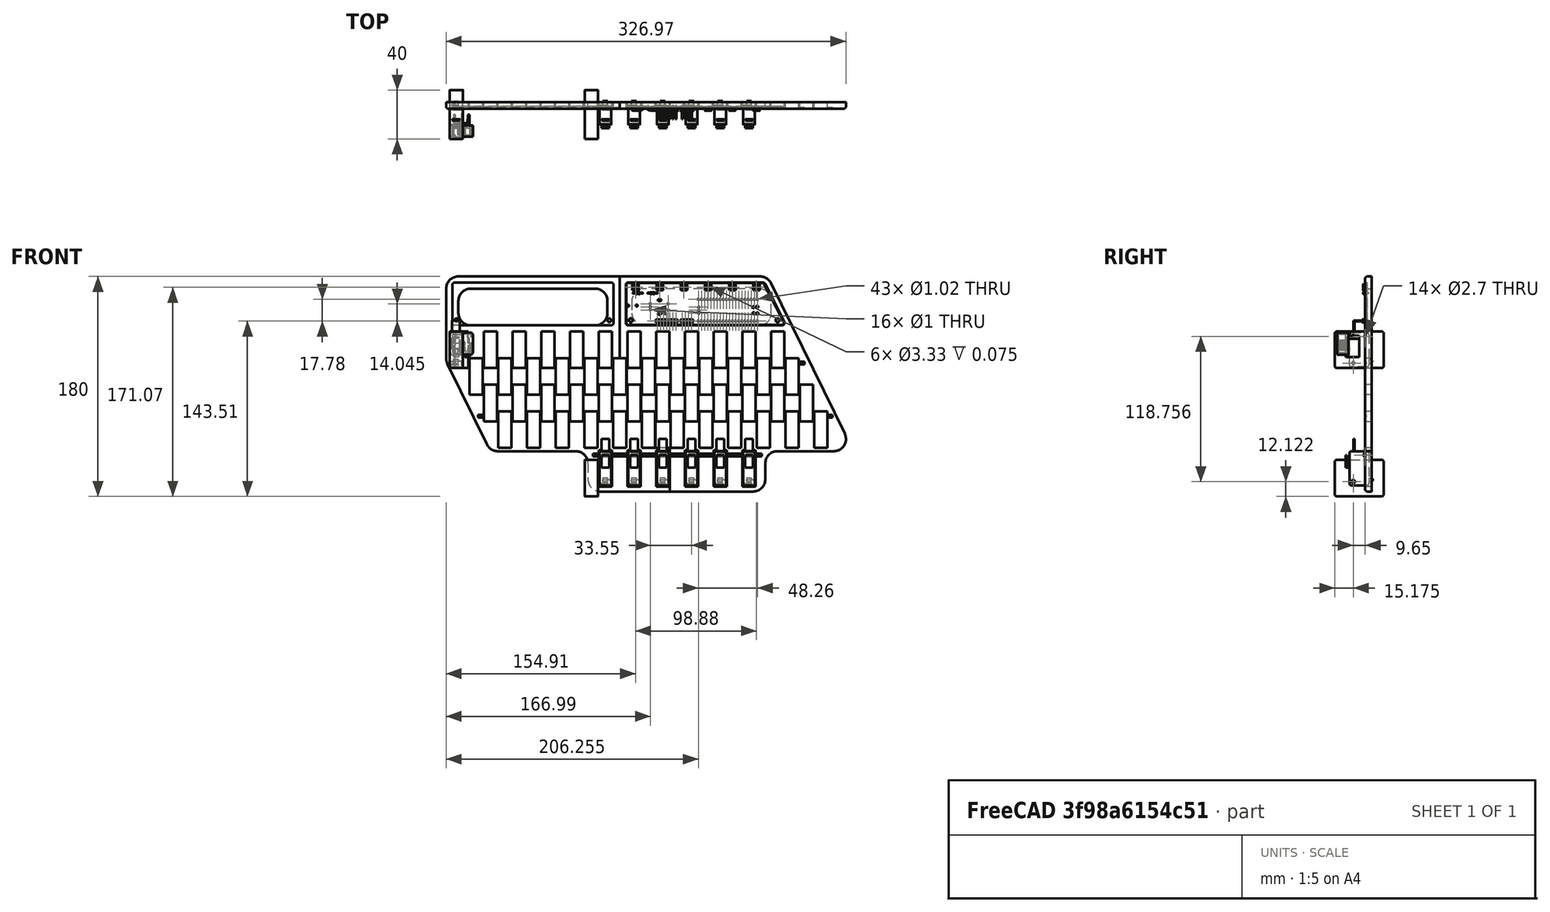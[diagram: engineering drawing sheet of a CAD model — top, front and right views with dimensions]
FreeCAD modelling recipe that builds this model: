
FCSTD DOCUMENT  (FreeCAD 0.20R29603 (Git))
Label: newKeyboard
License: All rights reserved
LicenseURL: http://en.wikipedia.org/wiki/All_rights_reserved
objects: Sketcher::SketchObject×88, PartDesign::Pad×83, PartDesign::Body×34, Part::FeaturePython×20, PartDesign::Fillet×12, Part::Cut×12, App::DocumentObjectGroup×8, PartDesign::FeatureBase×4, PartDesign::Revolution×2, PartDesign::Pocket×2, Mesh::Feature×1, PartDesign::ShapeBinder×1, Part::Extrusion×1, Part::Feature×1
note: 342 computed .brp shape members not serialized (recipe doc carries the construction recipe); baked Part::Feature solids carry a one-line shape summary decoded from their .brp

FEATURE [Sketcher::SketchObject] Sketch
  FullyConstrained = true
  MapMode = 5
  Support = -> [XY_Plane]
  sketch-geometry (12):
    g0: Circle CenterX=10.8779 CenterY=-4.825 CenterZ=0 NormalX=0 NormalY=0 NormalZ=1 AngleXU=0 Radius=1.35
    g1: Circle CenterX=-10.8779 CenterY=4.825 CenterZ=0 NormalX=0 NormalY=0 NormalZ=1 AngleXU=0 Radius=1.35
    g2: ArcOfCircle CenterX=-12.25 CenterY=6.25 CenterZ=0 NormalX=0 NormalY=0 NormalZ=1 AngleXU=0 Radius=1.75 StartAngle=1.5708 EndAngle=3.14159
    g3: LineSegment StartX=-12.25 StartY=8 StartZ=0 EndX=12.25 EndY=8 EndZ=0
    g4: ArcOfCircle CenterX=12.25 CenterY=6.25 CenterZ=0 NormalX=0 NormalY=0 NormalZ=1 AngleXU=0 Radius=1.75 StartAngle=3e-16 EndAngle=1.5708
    g5: LineSegment StartX=14 StartY=6.25 StartZ=0 EndX=14 EndY=-6.25 EndZ=0
    g6: ArcOfCircle CenterX=12.25 CenterY=-6.25 CenterZ=0 NormalX=0 NormalY=0 NormalZ=1 AngleXU=0 Radius=1.75 StartAngle=4.71239 EndAngle=6.28319
    g7: LineSegment StartX=12.25 StartY=-8 StartZ=0 EndX=-12.25 EndY=-8 EndZ=0
    g8: ArcOfCircle CenterX=-12.25 CenterY=-6.25 CenterZ=0 NormalX=0 NormalY=0 NormalZ=1 AngleXU=0 Radius=1.75 StartAngle=3.14159 EndAngle=4.71239
    g9: LineSegment StartX=-14 StartY=-6.25 StartZ=0 EndX=-14 EndY=6.25 EndZ=0
    g10: GeomPoint X=-14 Y=8 Z=0
    g11: GeomPoint X=14 Y=-8 Z=0
  constraints (28):
    c: Tangent(g2,g3) = 1.5708
    c: Tangent(g3,g4) = 1.5708
    c: Tangent(g4,g5) = 1.5708
    c: Tangent(g5,g6) = 1.5708
    c: Tangent(g6,g7) = 1.5708
    c: Tangent(g7,g8) = 1.5708
    c: Tangent(g8,g9) = 1.5708
    c: Tangent(g9,g2) = 1.5708
    c: Horizontal(g3)
    c: Horizontal(g7)
    c: Vertical(g5)
    c: Vertical(g9)
    c: Equal(g2,g4)
    c: Equal(g4,g6)
    c: Equal(g6,g8)
    c: PointOnObject(g10,g3)
    c: PointOnObject(g10,g9)
    c: PointOnObject(g11,g5)
    c: PointOnObject(g11,g7)
    c: DistanceX(g2,g4) = 28
    c: DistanceY(g7,g2) = 16
    c: Symmetric(g8,g4,g-1)
    c: Diameter(g2) = 3.5
    c: Symmetric(g0,g1,g-1)
    c: Diameter(g1) = 2.7
    c: Diameter(g0) = 2.7
    c: DistanceY(g0,g1) = 9.65
    c: Distance(g1,g0) = 23.8
FEATURE [PartDesign::Pad] Pad
  Direction = (0,0,1)
  Length = 9.7
  Length2 = 10
  Profile = -> Sketch
  ReferenceAxis = -> Sketch [N_Axis]
  Type = 0
FEATURE [Sketcher::SketchObject] Sketch001
  FullyConstrained = true
  MapMode = 5
  Placement = pos=(0,8,0) rot=(0,0.707107,0.707107;3.14159rad)
  Support = -> [Pad]
  sketch-geometry (4):
    g0: LineSegment StartX=-10.9 StartY=6.9 StartZ=0 EndX=-8 EndY=6.9 EndZ=0
    g1: LineSegment StartX=-8 StartY=6.9 StartZ=0 EndX=-8 EndY=2.8 EndZ=0
    g2: LineSegment StartX=-8 StartY=2.8 StartZ=0 EndX=-10.9 EndY=2.8 EndZ=0
    g3: LineSegment StartX=-10.9 StartY=2.8 StartZ=0 EndX=-10.9 EndY=6.9 EndZ=0
  constraints (12):
    c: Coincident(g0,g1)
    c: Coincident(g1,g2)
    c: Coincident(g2,g3)
    c: Coincident(g3,g0)
    c: Horizontal(g0)
    c: Horizontal(g2)
    c: Vertical(g1)
    c: Vertical(g3)
    c: DistanceX(g0,g0) = 2.9
    c: DistanceY(g3,g3) = 4.1
    c: DistanceY(g-1,g1) = 2.8
    c: DistanceX(g2,g-1) = 10.9
FEATURE [PartDesign::Pad] Pad001
  BaseFeature = -> Pad
  Direction = (0,1,-2e-16)
  Length = 3
  Length2 = 10
  Profile = -> Sketch001
  ReferenceAxis = -> Sketch001 [N_Axis]
  Type = 0
FEATURE [Sketcher::SketchObject] Sketch002
  FullyConstrained = true
  MapMode = 5
  Placement = pos=(-14,0,0) rot=(0.57735,-0.57735,-0.57735;2.0944rad)
  Support = -> [Pad001]
  sketch-geometry (4):
    g0: LineSegment StartX=3.9 StartY=1.65 StartZ=0 EndX=4.7 EndY=1.65 EndZ=0
    g1: LineSegment StartX=4.7 StartY=1.65 StartZ=0 EndX=4.7 EndY=8.05 EndZ=0
    g2: LineSegment StartX=4.7 StartY=8.05 StartZ=0 EndX=3.9 EndY=8.05 EndZ=0
    g3: LineSegment StartX=3.9 StartY=8.05 StartZ=0 EndX=3.9 EndY=1.65 EndZ=0
  constraints (12):
    c: Coincident(g0,g1)
    c: Coincident(g1,g2)
    c: Coincident(g2,g3)
    c: Coincident(g3,g0)
    c: Horizontal(g0)
    c: Horizontal(g2)
    c: Vertical(g1)
    c: Vertical(g3)
    c: DistanceX(g2,g2) = 0.8
    c: DistanceY(g3,g3) = 6.4
    c: DistanceY(g-1,g0) = 1.65
    c: DistanceX(g-1,g0) = 4.7
FEATURE [PartDesign::Pad] Pad002
  BaseFeature = -> Pad001
  Direction = (-1,0,0)
  Length = 10
  Length2 = 10
  Profile = -> Sketch002
  ReferenceAxis = -> Sketch002 [N_Axis]
  Type = 0
FEATURE [Sketcher::SketchObject] Sketch003
  FullyConstrained = true
  MapMode = 5
  Placement = pos=(0,-8,0) rot=(1,0,0;1.5708rad)
  Support = -> [Pad002]
  sketch-geometry (4):
    g0: LineSegment StartX=-1.3 StartY=8.05 StartZ=0 EndX=-0.5 EndY=8.05 EndZ=0
    g1: LineSegment StartX=-0.5 StartY=8.05 StartZ=0 EndX=-0.5 EndY=1.65 EndZ=0
    g2: LineSegment StartX=-0.5 StartY=1.65 StartZ=0 EndX=-1.3 EndY=1.65 EndZ=0
    g3: LineSegment StartX=-1.3 StartY=1.65 StartZ=0 EndX=-1.3 EndY=8.05 EndZ=0
  constraints (12):
    c: Coincident(g0,g1)
    c: Coincident(g1,g2)
    c: Coincident(g2,g3)
    c: Coincident(g3,g0)
    c: Horizontal(g0)
    c: Horizontal(g2)
    c: Vertical(g1)
    c: Vertical(g3)
    c: DistanceY(g1,g1) = 6.4
    c: DistanceX(g0,g0) = 0.8
    c: DistanceY(g-1,g1) = 1.65
    c: DistanceX(g1,g-1) = 0.5
FEATURE [PartDesign::Pad] Pad003
  BaseFeature = -> Pad002
  Direction = (0,-1,2e-16)
  Length = 3
  Length2 = 10
  Profile = -> Sketch003
  ReferenceAxis = -> Sketch003 [N_Axis]
  Type = 0
FEATURE [Sketcher::SketchObject] Sketch004
  FullyConstrained = true
  MapMode = 5
  Placement = pos=(-1.3,0,0) rot=(0.57735,-0.57735,-0.57735;2.0944rad)
  Support = -> [Pad003]
  sketch-geometry (4):
    g0: LineSegment StartX=10.2 StartY=8.05 StartZ=0 EndX=11 EndY=8.05 EndZ=0
    g1: LineSegment StartX=11 StartY=8.05 StartZ=0 EndX=11 EndY=1.65 EndZ=0
    g2: LineSegment StartX=11 StartY=1.65 StartZ=0 EndX=10.2 EndY=1.65 EndZ=0
    g3: LineSegment StartX=10.2 StartY=1.65 StartZ=0 EndX=10.2 EndY=8.05 EndZ=0
  constraints (12):
    c: Coincident(g0,g1)
    c: Coincident(g1,g2)
    c: Coincident(g2,g3)
    c: Coincident(g3,g0)
    c: Horizontal(g0)
    c: Horizontal(g2)
    c: Vertical(g1)
    c: Vertical(g3)
    c: DistanceX(g0,g0) = 0.8
    c: DistanceY(g1,g1) = 6.4
    c: DistanceY(g-1,g2) = 1.65
    c: DistanceX(g-1,g2) = 10.2
FEATURE [PartDesign::Pad] Pad004
  BaseFeature = -> Pad003
  Direction = (-1,0,0)
  Length = 9.3
  Length2 = 10
  Profile = -> Sketch004
  ReferenceAxis = -> Sketch004 [N_Axis]
  Type = 0
FEATURE [PartDesign::Fillet] Fillet
  Base = -> Pad004 [Edge36,Edge40]
  BaseFeature = -> Pad004
  Radius = 1.2
  SupportTransform = false
  UseAllEdges = false
FEATURE [PartDesign::Body] Body  label="switch"
  Group = -> [Sketch,Pad,Sketch001,Pad001,Sketch002,Pad002,Sketch003,Pad003,Sketch004,Pad004,Fillet]
  Origin = -> Origin
  Placement = pos=(0,0,0) rot=(0,1,0;1.5708rad)
  Tip = -> Fillet
FEATURE [Part::FeaturePython] Array  # Draft array (typed FeaturePython)
  AlwaysSyncPlacement = false
  Angle = 360
  ArrayType = 0
  Axis = (0,0,1)
  Base = -> Body
  Center = (0,0,0)
  Count = 12
  ExpandArray = false
  Fuse = false
  IntervalAxis = (0,0,0)
  IntervalX = (23.5,0,0)
  IntervalY = (0,100,0)
  IntervalZ = (0,0,40)
  NumberCircles = 3
  NumberPolar = 5
  NumberX = 12
  NumberY = 1
  NumberZ = 1
  Placement = pos=(273,0,0) rot=(0,1,0;3.14159rad)
  PlacementList = 12 placements: arithmetic series from (0,0,0) step (23.5,0,0) to (258.5,0,0)
  RadialDistance = 50
  ScaleList = (12) [(1,1,1),(1,1,1),(1,1,1),(1,1,1),(1,1,1),(1,1,1),(1,1,1),(1,1,1),(1,1,1),(1,1,1),(1,1,1),(1,1,1)]
  Symmetry = 1
  TangentialDistance = 25
FEATURE [Sketcher::SketchObject] Sketch021
  FullyConstrained = true
  MapMode = 5
  Support = -> [XY_Plane005]
  sketch-geometry (12):
    g0: Circle CenterX=10.8779 CenterY=-4.825 CenterZ=0 NormalX=0 NormalY=0 NormalZ=1 AngleXU=0 Radius=1.35
    g1: Circle CenterX=-10.8779 CenterY=4.825 CenterZ=0 NormalX=0 NormalY=0 NormalZ=1 AngleXU=0 Radius=1.35
    g2: ArcOfCircle CenterX=-12.25 CenterY=6.25 CenterZ=0 NormalX=0 NormalY=0 NormalZ=1 AngleXU=0 Radius=1.75 StartAngle=1.5708 EndAngle=3.14159
    g3: LineSegment StartX=-12.25 StartY=8 StartZ=0 EndX=12.25 EndY=8 EndZ=0
    g4: ArcOfCircle CenterX=12.25 CenterY=6.25 CenterZ=0 NormalX=0 NormalY=0 NormalZ=1 AngleXU=0 Radius=1.75 StartAngle=3e-16 EndAngle=1.5708
    g5: LineSegment StartX=14 StartY=6.25 StartZ=0 EndX=14 EndY=-6.25 EndZ=0
    g6: ArcOfCircle CenterX=12.25 CenterY=-6.25 CenterZ=0 NormalX=0 NormalY=0 NormalZ=1 AngleXU=0 Radius=1.75 StartAngle=4.71239 EndAngle=6.28319
    g7: LineSegment StartX=12.25 StartY=-8 StartZ=0 EndX=-12.25 EndY=-8 EndZ=0
    g8: ArcOfCircle CenterX=-12.25 CenterY=-6.25 CenterZ=0 NormalX=0 NormalY=0 NormalZ=1 AngleXU=0 Radius=1.75 StartAngle=3.14159 EndAngle=4.71239
    g9: LineSegment StartX=-14 StartY=-6.25 StartZ=0 EndX=-14 EndY=6.25 EndZ=0
    g10: GeomPoint X=-14 Y=8 Z=0
    g11: GeomPoint X=14 Y=-8 Z=0
  constraints (28):
    c: Tangent(g2,g3) = 1.5708
    c: Tangent(g3,g4) = 1.5708
    c: Tangent(g4,g5) = 1.5708
    c: Tangent(g5,g6) = 1.5708
    c: Tangent(g6,g7) = 1.5708
    c: Tangent(g7,g8) = 1.5708
    c: Tangent(g8,g9) = 1.5708
    c: Tangent(g9,g2) = 1.5708
    c: Horizontal(g3)
    c: Horizontal(g7)
    c: Vertical(g5)
    c: Vertical(g9)
    c: Equal(g2,g4)
    c: Equal(g4,g6)
    c: Equal(g6,g8)
    c: PointOnObject(g10,g3)
    c: PointOnObject(g10,g9)
    c: PointOnObject(g11,g5)
    c: PointOnObject(g11,g7)
    c: DistanceX(g2,g4) = 28
    c: DistanceY(g7,g2) = 16
    c: Symmetric(g8,g4,g-1)
    c: Diameter(g2) = 3.5
    c: Symmetric(g0,g1,g-1)
    c: Diameter(g1) = 2.7
    c: Diameter(g0) = 2.7
    c: DistanceY(g0,g1) = 9.65
    c: Distance(g1,g0) = 23.8
FEATURE [PartDesign::Pad] Pad021
  Direction = (0,0,1)
  Length = 9.7
  Length2 = 10
  Profile = -> Sketch021
  ReferenceAxis = -> Sketch021 [N_Axis]
  Type = 0
FEATURE [Sketcher::SketchObject] Sketch022
  FullyConstrained = true
  MapMode = 5
  Placement = pos=(0,8,0) rot=(0,0.707107,0.707107;3.14159rad)
  Support = -> [Pad021]
  sketch-geometry (4):
    g0: LineSegment StartX=-10.9 StartY=6.9 StartZ=0 EndX=-8 EndY=6.9 EndZ=0
    g1: LineSegment StartX=-8 StartY=6.9 StartZ=0 EndX=-8 EndY=2.8 EndZ=0
    g2: LineSegment StartX=-8 StartY=2.8 StartZ=0 EndX=-10.9 EndY=2.8 EndZ=0
    g3: LineSegment StartX=-10.9 StartY=2.8 StartZ=0 EndX=-10.9 EndY=6.9 EndZ=0
  constraints (12):
    c: Coincident(g0,g1)
    c: Coincident(g1,g2)
    c: Coincident(g2,g3)
    c: Coincident(g3,g0)
    c: Horizontal(g0)
    c: Horizontal(g2)
    c: Vertical(g1)
    c: Vertical(g3)
    c: DistanceX(g0,g0) = 2.9
    c: DistanceY(g3,g3) = 4.1
    c: DistanceY(g-1,g1) = 2.8
    c: DistanceX(g2,g-1) = 10.9
FEATURE [PartDesign::Pad] Pad022
  BaseFeature = -> Pad021
  Direction = (0,1,-2e-16)
  Length = 3
  Length2 = 10
  Profile = -> Sketch022
  ReferenceAxis = -> Sketch022 [N_Axis]
  Type = 0
FEATURE [Sketcher::SketchObject] Sketch023
  FullyConstrained = true
  MapMode = 5
  Placement = pos=(-14,0,0) rot=(0.57735,-0.57735,-0.57735;2.0944rad)
  Support = -> [Pad022]
  sketch-geometry (4):
    g0: LineSegment StartX=3.9 StartY=1.65 StartZ=0 EndX=4.7 EndY=1.65 EndZ=0
    g1: LineSegment StartX=4.7 StartY=1.65 StartZ=0 EndX=4.7 EndY=8.05 EndZ=0
    g2: LineSegment StartX=4.7 StartY=8.05 StartZ=0 EndX=3.9 EndY=8.05 EndZ=0
    g3: LineSegment StartX=3.9 StartY=8.05 StartZ=0 EndX=3.9 EndY=1.65 EndZ=0
  constraints (12):
    c: Coincident(g0,g1)
    c: Coincident(g1,g2)
    c: Coincident(g2,g3)
    c: Coincident(g3,g0)
    c: Horizontal(g0)
    c: Horizontal(g2)
    c: Vertical(g1)
    c: Vertical(g3)
    c: DistanceX(g2,g2) = 0.8
    c: DistanceY(g3,g3) = 6.4
    c: DistanceY(g-1,g0) = 1.65
    c: DistanceX(g-1,g0) = 4.7
FEATURE [PartDesign::Pad] Pad023
  BaseFeature = -> Pad022
  Direction = (-1,0,0)
  Length = 10
  Length2 = 10
  Profile = -> Sketch023
  ReferenceAxis = -> Sketch023 [N_Axis]
  Type = 0
FEATURE [Sketcher::SketchObject] Sketch024
  FullyConstrained = true
  MapMode = 5
  Placement = pos=(0,-8,0) rot=(1,0,0;1.5708rad)
  Support = -> [Pad023]
  sketch-geometry (4):
    g0: LineSegment StartX=-1.3 StartY=8.05 StartZ=0 EndX=-0.5 EndY=8.05 EndZ=0
    g1: LineSegment StartX=-0.5 StartY=8.05 StartZ=0 EndX=-0.5 EndY=1.65 EndZ=0
    g2: LineSegment StartX=-0.5 StartY=1.65 StartZ=0 EndX=-1.3 EndY=1.65 EndZ=0
    g3: LineSegment StartX=-1.3 StartY=1.65 StartZ=0 EndX=-1.3 EndY=8.05 EndZ=0
  constraints (12):
    c: Coincident(g0,g1)
    c: Coincident(g1,g2)
    c: Coincident(g2,g3)
    c: Coincident(g3,g0)
    c: Horizontal(g0)
    c: Horizontal(g2)
    c: Vertical(g1)
    c: Vertical(g3)
    c: DistanceY(g1,g1) = 6.4
    c: DistanceX(g0,g0) = 0.8
    c: DistanceY(g-1,g1) = 1.65
    c: DistanceX(g1,g-1) = 0.5
FEATURE [PartDesign::Pad] Pad024
  BaseFeature = -> Pad023
  Direction = (0,-1,2e-16)
  Length = 3
  Length2 = 10
  Profile = -> Sketch024
  ReferenceAxis = -> Sketch024 [N_Axis]
  Type = 0
FEATURE [Sketcher::SketchObject] Sketch025
  FullyConstrained = true
  MapMode = 5
  Placement = pos=(-1.3,0,0) rot=(0.57735,-0.57735,-0.57735;2.0944rad)
  Support = -> [Pad024]
  sketch-geometry (4):
    g0: LineSegment StartX=10.2 StartY=8.05 StartZ=0 EndX=11 EndY=8.05 EndZ=0
    g1: LineSegment StartX=11 StartY=8.05 StartZ=0 EndX=11 EndY=1.65 EndZ=0
    g2: LineSegment StartX=11 StartY=1.65 StartZ=0 EndX=10.2 EndY=1.65 EndZ=0
    g3: LineSegment StartX=10.2 StartY=1.65 StartZ=0 EndX=10.2 EndY=8.05 EndZ=0
  constraints (12):
    c: Coincident(g0,g1)
    c: Coincident(g1,g2)
    c: Coincident(g2,g3)
    c: Coincident(g3,g0)
    c: Horizontal(g0)
    c: Horizontal(g2)
    c: Vertical(g1)
    c: Vertical(g3)
    c: DistanceX(g0,g0) = 0.8
    c: DistanceY(g1,g1) = 6.4
    c: DistanceY(g-1,g2) = 1.65
    c: DistanceX(g-1,g2) = 10.2
FEATURE [PartDesign::Pad] Pad025
  BaseFeature = -> Pad024
  Direction = (-1,0,0)
  Length = 9.3
  Length2 = 10
  Profile = -> Sketch025
  ReferenceAxis = -> Sketch025 [N_Axis]
  Type = 0
FEATURE [PartDesign::Fillet] Fillet001
  Base = -> Pad025 [Edge36,Edge40]
  BaseFeature = -> Pad025
  Radius = 1.2
  SupportTransform = false
  UseAllEdges = false
FEATURE [PartDesign::Body] Body005  label="switch001"
  Group = -> [Sketch021,Pad021,Sketch022,Pad022,Sketch023,Pad023,Sketch024,Pad024,Sketch025,Pad025,Fillet001]
  Origin = -> Origin005
  Placement = pos=(0,0,0) rot=(0,1,0;1.5708rad)
  Tip = -> Fillet001
FEATURE [Part::FeaturePython] Array001  # Draft array (typed FeaturePython)
  AlwaysSyncPlacement = false
  Angle = 360
  ArrayType = 0
  Axis = (0,0,1)
  Base = -> Body005
  Center = (0,0,0)
  Count = 12
  ExpandArray = false
  Fuse = false
  IntervalAxis = (0,0,0)
  IntervalX = (23.5,0,0)
  IntervalY = (0,100,0)
  IntervalZ = (0,0,40)
  NumberCircles = 3
  NumberPolar = 5
  NumberX = 12
  NumberY = 1
  NumberZ = 1
  Placement = pos=(16.55,0,-21.76) rot=(0,1,0;0rad)
  PlacementList = 12 placements: arithmetic series from (0,0,0) step (23.5,0,0) to (258.5,0,0)
  RadialDistance = 50
  ScaleList = (12) [(1,1,1),(1,1,1),(1,1,1),(1,1,1),(1,1,1),(1,1,1),(1,1,1),(1,1,1),(1,1,1),(1,1,1),(1,1,1),(1,1,1)]
  Symmetry = 1
  TangentialDistance = 25
FEATURE [Sketcher::SketchObject] Sketch026
  FullyConstrained = true
  MapMode = 5
  Support = -> [XY_Plane006]
  sketch-geometry (12):
    g0: Circle CenterX=10.8779 CenterY=-4.825 CenterZ=0 NormalX=0 NormalY=0 NormalZ=1 AngleXU=0 Radius=1.35
    g1: Circle CenterX=-10.8779 CenterY=4.825 CenterZ=0 NormalX=0 NormalY=0 NormalZ=1 AngleXU=0 Radius=1.35
    g2: ArcOfCircle CenterX=-12.25 CenterY=6.25 CenterZ=0 NormalX=0 NormalY=0 NormalZ=1 AngleXU=0 Radius=1.75 StartAngle=1.5708 EndAngle=3.14159
    g3: LineSegment StartX=-12.25 StartY=8 StartZ=0 EndX=12.25 EndY=8 EndZ=0
    g4: ArcOfCircle CenterX=12.25 CenterY=6.25 CenterZ=0 NormalX=0 NormalY=0 NormalZ=1 AngleXU=0 Radius=1.75 StartAngle=3e-16 EndAngle=1.5708
    g5: LineSegment StartX=14 StartY=6.25 StartZ=0 EndX=14 EndY=-6.25 EndZ=0
    g6: ArcOfCircle CenterX=12.25 CenterY=-6.25 CenterZ=0 NormalX=0 NormalY=0 NormalZ=1 AngleXU=0 Radius=1.75 StartAngle=4.71239 EndAngle=6.28319
    g7: LineSegment StartX=12.25 StartY=-8 StartZ=0 EndX=-12.25 EndY=-8 EndZ=0
    g8: ArcOfCircle CenterX=-12.25 CenterY=-6.25 CenterZ=0 NormalX=0 NormalY=0 NormalZ=1 AngleXU=0 Radius=1.75 StartAngle=3.14159 EndAngle=4.71239
    g9: LineSegment StartX=-14 StartY=-6.25 StartZ=0 EndX=-14 EndY=6.25 EndZ=0
    g10: GeomPoint X=-14 Y=8 Z=0
    g11: GeomPoint X=14 Y=-8 Z=0
  constraints (28):
    c: Tangent(g2,g3) = 1.5708
    c: Tangent(g3,g4) = 1.5708
    c: Tangent(g4,g5) = 1.5708
    c: Tangent(g5,g6) = 1.5708
    c: Tangent(g6,g7) = 1.5708
    c: Tangent(g7,g8) = 1.5708
    c: Tangent(g8,g9) = 1.5708
    c: Tangent(g9,g2) = 1.5708
    c: Horizontal(g3)
    c: Horizontal(g7)
    c: Vertical(g5)
    c: Vertical(g9)
    c: Equal(g2,g4)
    c: Equal(g4,g6)
    c: Equal(g6,g8)
    c: PointOnObject(g10,g3)
    c: PointOnObject(g10,g9)
    c: PointOnObject(g11,g5)
    c: PointOnObject(g11,g7)
    c: DistanceX(g2,g4) = 28
    c: DistanceY(g7,g2) = 16
    c: Symmetric(g8,g4,g-1)
    c: Diameter(g2) = 3.5
    c: Symmetric(g0,g1,g-1)
    c: Diameter(g1) = 2.7
    c: Diameter(g0) = 2.7
    c: DistanceY(g0,g1) = 9.65
    c: Distance(g1,g0) = 23.8
FEATURE [PartDesign::Pad] Pad026
  Direction = (0,0,1)
  Length = 9.7
  Length2 = 10
  Profile = -> Sketch026
  ReferenceAxis = -> Sketch026 [N_Axis]
  Type = 0
FEATURE [Sketcher::SketchObject] Sketch027
  FullyConstrained = true
  MapMode = 5
  Placement = pos=(0,8,0) rot=(0,0.707107,0.707107;3.14159rad)
  Support = -> [Pad026]
  sketch-geometry (4):
    g0: LineSegment StartX=-10.9 StartY=6.9 StartZ=0 EndX=-8 EndY=6.9 EndZ=0
    g1: LineSegment StartX=-8 StartY=6.9 StartZ=0 EndX=-8 EndY=2.8 EndZ=0
    g2: LineSegment StartX=-8 StartY=2.8 StartZ=0 EndX=-10.9 EndY=2.8 EndZ=0
    g3: LineSegment StartX=-10.9 StartY=2.8 StartZ=0 EndX=-10.9 EndY=6.9 EndZ=0
  constraints (12):
    c: Coincident(g0,g1)
    c: Coincident(g1,g2)
    c: Coincident(g2,g3)
    c: Coincident(g3,g0)
    c: Horizontal(g0)
    c: Horizontal(g2)
    c: Vertical(g1)
    c: Vertical(g3)
    c: DistanceX(g0,g0) = 2.9
    c: DistanceY(g3,g3) = 4.1
    c: DistanceY(g-1,g1) = 2.8
    c: DistanceX(g2,g-1) = 10.9
FEATURE [PartDesign::Pad] Pad027
  BaseFeature = -> Pad026
  Direction = (0,1,-2e-16)
  Length = 3
  Length2 = 10
  Profile = -> Sketch027
  ReferenceAxis = -> Sketch027 [N_Axis]
  Type = 0
FEATURE [Sketcher::SketchObject] Sketch028
  FullyConstrained = true
  MapMode = 5
  Placement = pos=(-14,0,0) rot=(0.57735,-0.57735,-0.57735;2.0944rad)
  Support = -> [Pad027]
  sketch-geometry (4):
    g0: LineSegment StartX=3.9 StartY=1.65 StartZ=0 EndX=4.7 EndY=1.65 EndZ=0
    g1: LineSegment StartX=4.7 StartY=1.65 StartZ=0 EndX=4.7 EndY=8.05 EndZ=0
    g2: LineSegment StartX=4.7 StartY=8.05 StartZ=0 EndX=3.9 EndY=8.05 EndZ=0
    g3: LineSegment StartX=3.9 StartY=8.05 StartZ=0 EndX=3.9 EndY=1.65 EndZ=0
  constraints (12):
    c: Coincident(g0,g1)
    c: Coincident(g1,g2)
    c: Coincident(g2,g3)
    c: Coincident(g3,g0)
    c: Horizontal(g0)
    c: Horizontal(g2)
    c: Vertical(g1)
    c: Vertical(g3)
    c: DistanceX(g2,g2) = 0.8
    c: DistanceY(g3,g3) = 6.4
    c: DistanceY(g-1,g0) = 1.65
    c: DistanceX(g-1,g0) = 4.7
FEATURE [PartDesign::Pad] Pad028
  BaseFeature = -> Pad027
  Direction = (-1,0,0)
  Length = 10
  Length2 = 10
  Profile = -> Sketch028
  ReferenceAxis = -> Sketch028 [N_Axis]
  Type = 0
FEATURE [Sketcher::SketchObject] Sketch029
  FullyConstrained = true
  MapMode = 5
  Placement = pos=(0,-8,0) rot=(1,0,0;1.5708rad)
  Support = -> [Pad028]
  sketch-geometry (4):
    g0: LineSegment StartX=-1.3 StartY=8.05 StartZ=0 EndX=-0.5 EndY=8.05 EndZ=0
    g1: LineSegment StartX=-0.5 StartY=8.05 StartZ=0 EndX=-0.5 EndY=1.65 EndZ=0
    g2: LineSegment StartX=-0.5 StartY=1.65 StartZ=0 EndX=-1.3 EndY=1.65 EndZ=0
    g3: LineSegment StartX=-1.3 StartY=1.65 StartZ=0 EndX=-1.3 EndY=8.05 EndZ=0
  constraints (12):
    c: Coincident(g0,g1)
    c: Coincident(g1,g2)
    c: Coincident(g2,g3)
    c: Coincident(g3,g0)
    c: Horizontal(g0)
    c: Horizontal(g2)
    c: Vertical(g1)
    c: Vertical(g3)
    c: DistanceY(g1,g1) = 6.4
    c: DistanceX(g0,g0) = 0.8
    c: DistanceY(g-1,g1) = 1.65
    c: DistanceX(g1,g-1) = 0.5
FEATURE [PartDesign::Pad] Pad029
  BaseFeature = -> Pad028
  Direction = (0,-1,2e-16)
  Length = 3
  Length2 = 10
  Profile = -> Sketch029
  ReferenceAxis = -> Sketch029 [N_Axis]
  Type = 0
FEATURE [Sketcher::SketchObject] Sketch030
  FullyConstrained = true
  MapMode = 5
  Placement = pos=(-1.3,0,0) rot=(0.57735,-0.57735,-0.57735;2.0944rad)
  Support = -> [Pad029]
  sketch-geometry (4):
    g0: LineSegment StartX=10.2 StartY=8.05 StartZ=0 EndX=11 EndY=8.05 EndZ=0
    g1: LineSegment StartX=11 StartY=8.05 StartZ=0 EndX=11 EndY=1.65 EndZ=0
    g2: LineSegment StartX=11 StartY=1.65 StartZ=0 EndX=10.2 EndY=1.65 EndZ=0
    g3: LineSegment StartX=10.2 StartY=1.65 StartZ=0 EndX=10.2 EndY=8.05 EndZ=0
  constraints (12):
    c: Coincident(g0,g1)
    c: Coincident(g1,g2)
    c: Coincident(g2,g3)
    c: Coincident(g3,g0)
    c: Horizontal(g0)
    c: Horizontal(g2)
    c: Vertical(g1)
    c: Vertical(g3)
    c: DistanceX(g0,g0) = 0.8
    c: DistanceY(g1,g1) = 6.4
    c: DistanceY(g-1,g2) = 1.65
    c: DistanceX(g-1,g2) = 10.2
FEATURE [PartDesign::Pad] Pad030
  BaseFeature = -> Pad029
  Direction = (-1,0,0)
  Length = 9.3
  Length2 = 10
  Profile = -> Sketch030
  ReferenceAxis = -> Sketch030 [N_Axis]
  Type = 0
FEATURE [PartDesign::Fillet] Fillet002
  Base = -> Pad030 [Edge36,Edge40]
  BaseFeature = -> Pad030
  Radius = 1.2
  SupportTransform = false
  UseAllEdges = false
FEATURE [PartDesign::Body] Body006  label="switch002"
  Group = -> [Sketch026,Pad026,Sketch027,Pad027,Sketch028,Pad028,Sketch029,Pad029,Sketch030,Pad030,Fillet002]
  Origin = -> Origin006
  Placement = pos=(0,0,0) rot=(0,1,0;1.5708rad)
  Tip = -> Fillet002
FEATURE [Part::FeaturePython] Array002  # Draft array (typed FeaturePython)
  AlwaysSyncPlacement = false
  Angle = 360
  ArrayType = 0
  Axis = (0,0,1)
  Base = -> Body006
  Center = (0,0,0)
  Count = 12
  ExpandArray = false
  Fuse = false
  IntervalAxis = (0,0,0)
  IntervalX = (23.5,0,0)
  IntervalY = (0,100,0)
  IntervalZ = (0,0,40)
  NumberCircles = 3
  NumberPolar = 5
  NumberX = 12
  NumberY = 1
  NumberZ = 1
  Placement = pos=(296.5,0,-43.52) rot=(0,1,0;3.14159rad)
  PlacementList = 12 placements: arithmetic series from (0,0,0) step (23.5,0,0) to (258.5,0,0)
  RadialDistance = 50
  ScaleList = (12) [(1,1,1),(1,1,1),(1,1,1),(1,1,1),(1,1,1),(1,1,1),(1,1,1),(1,1,1),(1,1,1),(1,1,1),(1,1,1),(1,1,1)]
  Symmetry = 1
  TangentialDistance = 25
FEATURE [Sketcher::SketchObject] Sketch031
  FullyConstrained = true
  MapMode = 5
  Support = -> [XY_Plane007]
  sketch-geometry (12):
    g0: Circle CenterX=10.8779 CenterY=-4.825 CenterZ=0 NormalX=0 NormalY=0 NormalZ=1 AngleXU=0 Radius=1.35
    g1: Circle CenterX=-10.8779 CenterY=4.825 CenterZ=0 NormalX=0 NormalY=0 NormalZ=1 AngleXU=0 Radius=1.35
    g2: ArcOfCircle CenterX=-12.25 CenterY=6.25 CenterZ=0 NormalX=0 NormalY=0 NormalZ=1 AngleXU=0 Radius=1.75 StartAngle=1.5708 EndAngle=3.14159
    g3: LineSegment StartX=-12.25 StartY=8 StartZ=0 EndX=12.25 EndY=8 EndZ=0
    g4: ArcOfCircle CenterX=12.25 CenterY=6.25 CenterZ=0 NormalX=0 NormalY=0 NormalZ=1 AngleXU=0 Radius=1.75 StartAngle=3e-16 EndAngle=1.5708
    g5: LineSegment StartX=14 StartY=6.25 StartZ=0 EndX=14 EndY=-6.25 EndZ=0
    g6: ArcOfCircle CenterX=12.25 CenterY=-6.25 CenterZ=0 NormalX=0 NormalY=0 NormalZ=1 AngleXU=0 Radius=1.75 StartAngle=4.71239 EndAngle=6.28319
    g7: LineSegment StartX=12.25 StartY=-8 StartZ=0 EndX=-12.25 EndY=-8 EndZ=0
    g8: ArcOfCircle CenterX=-12.25 CenterY=-6.25 CenterZ=0 NormalX=0 NormalY=0 NormalZ=1 AngleXU=0 Radius=1.75 StartAngle=3.14159 EndAngle=4.71239
    g9: LineSegment StartX=-14 StartY=-6.25 StartZ=0 EndX=-14 EndY=6.25 EndZ=0
    g10: GeomPoint X=-14 Y=8 Z=0
    g11: GeomPoint X=14 Y=-8 Z=0
  constraints (28):
    c: Tangent(g2,g3) = 1.5708
    c: Tangent(g3,g4) = 1.5708
    c: Tangent(g4,g5) = 1.5708
    c: Tangent(g5,g6) = 1.5708
    c: Tangent(g6,g7) = 1.5708
    c: Tangent(g7,g8) = 1.5708
    c: Tangent(g8,g9) = 1.5708
    c: Tangent(g9,g2) = 1.5708
    c: Horizontal(g3)
    c: Horizontal(g7)
    c: Vertical(g5)
    c: Vertical(g9)
    c: Equal(g2,g4)
    c: Equal(g4,g6)
    c: Equal(g6,g8)
    c: PointOnObject(g10,g3)
    c: PointOnObject(g10,g9)
    c: PointOnObject(g11,g5)
    c: PointOnObject(g11,g7)
    c: DistanceX(g2,g4) = 28
    c: DistanceY(g7,g2) = 16
    c: Symmetric(g8,g4,g-1)
    c: Diameter(g2) = 3.5
    c: Symmetric(g0,g1,g-1)
    c: Diameter(g1) = 2.7
    c: Diameter(g0) = 2.7
    c: DistanceY(g0,g1) = 9.65
    c: Distance(g1,g0) = 23.8
FEATURE [PartDesign::Pad] Pad031
  Direction = (0,0,1)
  Length = 9.7
  Length2 = 10
  Profile = -> Sketch031
  ReferenceAxis = -> Sketch031 [N_Axis]
  Type = 0
FEATURE [Sketcher::SketchObject] Sketch032
  FullyConstrained = true
  MapMode = 5
  Placement = pos=(0,8,0) rot=(0,0.707107,0.707107;3.14159rad)
  Support = -> [Pad031]
  sketch-geometry (4):
    g0: LineSegment StartX=-10.9 StartY=6.9 StartZ=0 EndX=-8 EndY=6.9 EndZ=0
    g1: LineSegment StartX=-8 StartY=6.9 StartZ=0 EndX=-8 EndY=2.8 EndZ=0
    g2: LineSegment StartX=-8 StartY=2.8 StartZ=0 EndX=-10.9 EndY=2.8 EndZ=0
    g3: LineSegment StartX=-10.9 StartY=2.8 StartZ=0 EndX=-10.9 EndY=6.9 EndZ=0
  constraints (12):
    c: Coincident(g0,g1)
    c: Coincident(g1,g2)
    c: Coincident(g2,g3)
    c: Coincident(g3,g0)
    c: Horizontal(g0)
    c: Horizontal(g2)
    c: Vertical(g1)
    c: Vertical(g3)
    c: DistanceX(g0,g0) = 2.9
    c: DistanceY(g3,g3) = 4.1
    c: DistanceY(g-1,g1) = 2.8
    c: DistanceX(g2,g-1) = 10.9
FEATURE [PartDesign::Pad] Pad032
  BaseFeature = -> Pad031
  Direction = (0,1,-2e-16)
  Length = 3
  Length2 = 10
  Profile = -> Sketch032
  ReferenceAxis = -> Sketch032 [N_Axis]
  Type = 0
FEATURE [Sketcher::SketchObject] Sketch033
  FullyConstrained = true
  MapMode = 5
  Placement = pos=(-14,0,0) rot=(0.57735,-0.57735,-0.57735;2.0944rad)
  Support = -> [Pad032]
  sketch-geometry (4):
    g0: LineSegment StartX=3.9 StartY=1.65 StartZ=0 EndX=4.7 EndY=1.65 EndZ=0
    g1: LineSegment StartX=4.7 StartY=1.65 StartZ=0 EndX=4.7 EndY=8.05 EndZ=0
    g2: LineSegment StartX=4.7 StartY=8.05 StartZ=0 EndX=3.9 EndY=8.05 EndZ=0
    g3: LineSegment StartX=3.9 StartY=8.05 StartZ=0 EndX=3.9 EndY=1.65 EndZ=0
  constraints (12):
    c: Coincident(g0,g1)
    c: Coincident(g1,g2)
    c: Coincident(g2,g3)
    c: Coincident(g3,g0)
    c: Horizontal(g0)
    c: Horizontal(g2)
    c: Vertical(g1)
    c: Vertical(g3)
    c: DistanceX(g2,g2) = 0.8
    c: DistanceY(g3,g3) = 6.4
    c: DistanceY(g-1,g0) = 1.65
    c: DistanceX(g-1,g0) = 4.7
FEATURE [PartDesign::Pad] Pad033
  BaseFeature = -> Pad032
  Direction = (-1,0,0)
  Length = 10
  Length2 = 10
  Profile = -> Sketch033
  ReferenceAxis = -> Sketch033 [N_Axis]
  Type = 0
FEATURE [Sketcher::SketchObject] Sketch034
  FullyConstrained = true
  MapMode = 5
  Placement = pos=(0,-8,0) rot=(1,0,0;1.5708rad)
  Support = -> [Pad033]
  sketch-geometry (4):
    g0: LineSegment StartX=-1.3 StartY=8.05 StartZ=0 EndX=-0.5 EndY=8.05 EndZ=0
    g1: LineSegment StartX=-0.5 StartY=8.05 StartZ=0 EndX=-0.5 EndY=1.65 EndZ=0
    g2: LineSegment StartX=-0.5 StartY=1.65 StartZ=0 EndX=-1.3 EndY=1.65 EndZ=0
    g3: LineSegment StartX=-1.3 StartY=1.65 StartZ=0 EndX=-1.3 EndY=8.05 EndZ=0
  constraints (12):
    c: Coincident(g0,g1)
    c: Coincident(g1,g2)
    c: Coincident(g2,g3)
    c: Coincident(g3,g0)
    c: Horizontal(g0)
    c: Horizontal(g2)
    c: Vertical(g1)
    c: Vertical(g3)
    c: DistanceY(g1,g1) = 6.4
    c: DistanceX(g0,g0) = 0.8
    c: DistanceY(g-1,g1) = 1.65
    c: DistanceX(g1,g-1) = 0.5
FEATURE [PartDesign::Pad] Pad034
  BaseFeature = -> Pad033
  Direction = (0,-1,2e-16)
  Length = 3
  Length2 = 10
  Profile = -> Sketch034
  ReferenceAxis = -> Sketch034 [N_Axis]
  Type = 0
FEATURE [Sketcher::SketchObject] Sketch035
  FullyConstrained = true
  MapMode = 5
  Placement = pos=(-1.3,0,0) rot=(0.57735,-0.57735,-0.57735;2.0944rad)
  Support = -> [Pad034]
  sketch-geometry (4):
    g0: LineSegment StartX=10.2 StartY=8.05 StartZ=0 EndX=11 EndY=8.05 EndZ=0
    g1: LineSegment StartX=11 StartY=8.05 StartZ=0 EndX=11 EndY=1.65 EndZ=0
    g2: LineSegment StartX=11 StartY=1.65 StartZ=0 EndX=10.2 EndY=1.65 EndZ=0
    g3: LineSegment StartX=10.2 StartY=1.65 StartZ=0 EndX=10.2 EndY=8.05 EndZ=0
  constraints (12):
    c: Coincident(g0,g1)
    c: Coincident(g1,g2)
    c: Coincident(g2,g3)
    c: Coincident(g3,g0)
    c: Horizontal(g0)
    c: Horizontal(g2)
    c: Vertical(g1)
    c: Vertical(g3)
    c: DistanceX(g0,g0) = 0.8
    c: DistanceY(g1,g1) = 6.4
    c: DistanceY(g-1,g2) = 1.65
    c: DistanceX(g-1,g2) = 10.2
FEATURE [PartDesign::Pad] Pad035
  BaseFeature = -> Pad034
  Direction = (-1,0,0)
  Length = 9.3
  Length2 = 10
  Profile = -> Sketch035
  ReferenceAxis = -> Sketch035 [N_Axis]
  Type = 0
FEATURE [PartDesign::Fillet] Fillet003
  Base = -> Pad035 [Edge36,Edge40]
  BaseFeature = -> Pad035
  Radius = 1.2
  SupportTransform = false
  UseAllEdges = false
FEATURE [PartDesign::Body] Body007  label="switch003"
  Group = -> [Sketch031,Pad031,Sketch032,Pad032,Sketch033,Pad033,Sketch034,Pad034,Sketch035,Pad035,Fillet003]
  Origin = -> Origin007
  Placement = pos=(0,0,0) rot=(0,1,0;1.5708rad)
  Tip = -> Fillet003
FEATURE [Part::FeaturePython] Array003  # Draft array (typed FeaturePython)
  AlwaysSyncPlacement = false
  Angle = 360
  ArrayType = 0
  Axis = (0,0,1)
  Base = -> Body007
  Center = (0,0,0)
  Count = 12
  ExpandArray = false
  Fuse = false
  IntervalAxis = (0,0,0)
  IntervalX = (23.5,0,0)
  IntervalY = (0,100,0)
  IntervalZ = (0,0,40)
  NumberCircles = 3
  NumberPolar = 5
  NumberX = 12
  NumberY = 1
  NumberZ = 1
  Placement = pos=(40.05,0,-65.28) rot=(0,1,0;0rad)
  PlacementList = 12 placements: arithmetic series from (0,0,0) step (23.5,0,0) to (258.5,0,0)
  RadialDistance = 50
  ScaleList = (12) [(1,1,1),(1,1,1),(1,1,1),(1,1,1),(1,1,1),(1,1,1),(1,1,1),(1,1,1),(1,1,1),(1,1,1),(1,1,1),(1,1,1)]
  Symmetry = 1
  TangentialDistance = 25
FEATURE [Mesh::Feature] keyboard
  Placement = pos=(168,0,-43) rot=(1,0,0;1.5708rad)
FEATURE [Sketcher::SketchObject] Sketch036
  FullyConstrained = true
  MapMode = 5
  Support = -> [XY_Plane008]
  sketch-geometry (12):
    g0: Circle CenterX=10.8779 CenterY=-4.825 CenterZ=0 NormalX=0 NormalY=0 NormalZ=1 AngleXU=0 Radius=1.35
    g1: Circle CenterX=-10.8779 CenterY=4.825 CenterZ=0 NormalX=0 NormalY=0 NormalZ=1 AngleXU=0 Radius=1.35
    g2: ArcOfCircle CenterX=-12.25 CenterY=6.25 CenterZ=0 NormalX=0 NormalY=0 NormalZ=1 AngleXU=0 Radius=1.75 StartAngle=1.5708 EndAngle=3.14159
    g3: LineSegment StartX=-12.25 StartY=8 StartZ=0 EndX=12.25 EndY=8 EndZ=0
    g4: ArcOfCircle CenterX=12.25 CenterY=6.25 CenterZ=0 NormalX=0 NormalY=0 NormalZ=1 AngleXU=0 Radius=1.75 StartAngle=3e-16 EndAngle=1.5708
    g5: LineSegment StartX=14 StartY=6.25 StartZ=0 EndX=14 EndY=-6.25 EndZ=0
    g6: ArcOfCircle CenterX=12.25 CenterY=-6.25 CenterZ=0 NormalX=0 NormalY=0 NormalZ=1 AngleXU=0 Radius=1.75 StartAngle=4.71239 EndAngle=6.28319
    g7: LineSegment StartX=12.25 StartY=-8 StartZ=0 EndX=-12.25 EndY=-8 EndZ=0
    g8: ArcOfCircle CenterX=-12.25 CenterY=-6.25 CenterZ=0 NormalX=0 NormalY=0 NormalZ=1 AngleXU=0 Radius=1.75 StartAngle=3.14159 EndAngle=4.71239
    g9: LineSegment StartX=-14 StartY=-6.25 StartZ=0 EndX=-14 EndY=6.25 EndZ=0
    g10: GeomPoint X=-14 Y=8 Z=0
    g11: GeomPoint X=14 Y=-8 Z=0
  constraints (28):
    c: Tangent(g2,g3) = 1.5708
    c: Tangent(g3,g4) = 1.5708
    c: Tangent(g4,g5) = 1.5708
    c: Tangent(g5,g6) = 1.5708
    c: Tangent(g6,g7) = 1.5708
    c: Tangent(g7,g8) = 1.5708
    c: Tangent(g8,g9) = 1.5708
    c: Tangent(g9,g2) = 1.5708
    c: Horizontal(g3)
    c: Horizontal(g7)
    c: Vertical(g5)
    c: Vertical(g9)
    c: Equal(g2,g4)
    c: Equal(g4,g6)
    c: Equal(g6,g8)
    c: PointOnObject(g10,g3)
    c: PointOnObject(g10,g9)
    c: PointOnObject(g11,g5)
    c: PointOnObject(g11,g7)
    c: DistanceX(g2,g4) = 28
    c: DistanceY(g7,g2) = 16
    c: Symmetric(g8,g4,g-1)
    c: Diameter(g2) = 3.5
    c: Symmetric(g0,g1,g-1)
    c: Diameter(g1) = 2.7
    c: Diameter(g0) = 2.7
    c: DistanceY(g0,g1) = 9.65
    c: Distance(g1,g0) = 23.8
FEATURE [PartDesign::Pad] Pad036
  Direction = (0,0,1)
  Length = 9.7
  Length2 = 10
  Profile = -> Sketch036
  ReferenceAxis = -> Sketch036 [N_Axis]
  Type = 0
FEATURE [Sketcher::SketchObject] Sketch037
  FullyConstrained = true
  MapMode = 5
  Placement = pos=(0,8,0) rot=(0,0.707107,0.707107;3.14159rad)
  Support = -> [Pad036]
  sketch-geometry (4):
    g0: LineSegment StartX=-10.9 StartY=6.9 StartZ=0 EndX=-8 EndY=6.9 EndZ=0
    g1: LineSegment StartX=-8 StartY=6.9 StartZ=0 EndX=-8 EndY=2.8 EndZ=0
    g2: LineSegment StartX=-8 StartY=2.8 StartZ=0 EndX=-10.9 EndY=2.8 EndZ=0
    g3: LineSegment StartX=-10.9 StartY=2.8 StartZ=0 EndX=-10.9 EndY=6.9 EndZ=0
  constraints (12):
    c: Coincident(g0,g1)
    c: Coincident(g1,g2)
    c: Coincident(g2,g3)
    c: Coincident(g3,g0)
    c: Horizontal(g0)
    c: Horizontal(g2)
    c: Vertical(g1)
    c: Vertical(g3)
    c: DistanceX(g0,g0) = 2.9
    c: DistanceY(g3,g3) = 4.1
    c: DistanceY(g-1,g1) = 2.8
    c: DistanceX(g2,g-1) = 10.9
FEATURE [PartDesign::Pad] Pad037
  BaseFeature = -> Pad036
  Direction = (0,1,-2e-16)
  Length = 3
  Length2 = 10
  Profile = -> Sketch037
  ReferenceAxis = -> Sketch037 [N_Axis]
  Type = 0
FEATURE [Sketcher::SketchObject] Sketch038
  FullyConstrained = true
  MapMode = 5
  Placement = pos=(-14,0,0) rot=(0.57735,-0.57735,-0.57735;2.0944rad)
  Support = -> [Pad037]
  sketch-geometry (4):
    g0: LineSegment StartX=3.9 StartY=1.65 StartZ=0 EndX=4.7 EndY=1.65 EndZ=0
    g1: LineSegment StartX=4.7 StartY=1.65 StartZ=0 EndX=4.7 EndY=8.05 EndZ=0
    g2: LineSegment StartX=4.7 StartY=8.05 StartZ=0 EndX=3.9 EndY=8.05 EndZ=0
    g3: LineSegment StartX=3.9 StartY=8.05 StartZ=0 EndX=3.9 EndY=1.65 EndZ=0
  constraints (12):
    c: Coincident(g0,g1)
    c: Coincident(g1,g2)
    c: Coincident(g2,g3)
    c: Coincident(g3,g0)
    c: Horizontal(g0)
    c: Horizontal(g2)
    c: Vertical(g1)
    c: Vertical(g3)
    c: DistanceX(g2,g2) = 0.8
    c: DistanceY(g3,g3) = 6.4
    c: DistanceY(g-1,g0) = 1.65
    c: DistanceX(g-1,g0) = 4.7
FEATURE [PartDesign::Pad] Pad038
  BaseFeature = -> Pad037
  Direction = (-1,0,0)
  Length = 10
  Length2 = 10
  Profile = -> Sketch038
  ReferenceAxis = -> Sketch038 [N_Axis]
  Type = 0
FEATURE [Sketcher::SketchObject] Sketch039
  FullyConstrained = true
  MapMode = 5
  Placement = pos=(0,-8,0) rot=(1,0,0;1.5708rad)
  Support = -> [Pad038]
  sketch-geometry (4):
    g0: LineSegment StartX=-1.3 StartY=8.05 StartZ=0 EndX=-0.5 EndY=8.05 EndZ=0
    g1: LineSegment StartX=-0.5 StartY=8.05 StartZ=0 EndX=-0.5 EndY=1.65 EndZ=0
    g2: LineSegment StartX=-0.5 StartY=1.65 StartZ=0 EndX=-1.3 EndY=1.65 EndZ=0
    g3: LineSegment StartX=-1.3 StartY=1.65 StartZ=0 EndX=-1.3 EndY=8.05 EndZ=0
  constraints (12):
    c: Coincident(g0,g1)
    c: Coincident(g1,g2)
    c: Coincident(g2,g3)
    c: Coincident(g3,g0)
    c: Horizontal(g0)
    c: Horizontal(g2)
    c: Vertical(g1)
    c: Vertical(g3)
    c: DistanceY(g1,g1) = 6.4
    c: DistanceX(g0,g0) = 0.8
    c: DistanceY(g-1,g1) = 1.65
    c: DistanceX(g1,g-1) = 0.5
FEATURE [PartDesign::Pad] Pad039
  BaseFeature = -> Pad038
  Direction = (0,-1,2e-16)
  Length = 3
  Length2 = 10
  Profile = -> Sketch039
  ReferenceAxis = -> Sketch039 [N_Axis]
  Type = 0
FEATURE [Sketcher::SketchObject] Sketch040
  FullyConstrained = true
  MapMode = 5
  Placement = pos=(-1.3,0,0) rot=(0.57735,-0.57735,-0.57735;2.0944rad)
  Support = -> [Pad039]
  sketch-geometry (4):
    g0: LineSegment StartX=10.2 StartY=8.05 StartZ=0 EndX=11 EndY=8.05 EndZ=0
    g1: LineSegment StartX=11 StartY=8.05 StartZ=0 EndX=11 EndY=1.65 EndZ=0
    g2: LineSegment StartX=11 StartY=1.65 StartZ=0 EndX=10.2 EndY=1.65 EndZ=0
    g3: LineSegment StartX=10.2 StartY=1.65 StartZ=0 EndX=10.2 EndY=8.05 EndZ=0
  constraints (12):
    c: Coincident(g0,g1)
    c: Coincident(g1,g2)
    c: Coincident(g2,g3)
    c: Coincident(g3,g0)
    c: Horizontal(g0)
    c: Horizontal(g2)
    c: Vertical(g1)
    c: Vertical(g3)
    c: DistanceX(g0,g0) = 0.8
    c: DistanceY(g1,g1) = 6.4
    c: DistanceY(g-1,g2) = 1.65
    c: DistanceX(g-1,g2) = 10.2
FEATURE [PartDesign::Pad] Pad040
  BaseFeature = -> Pad039
  Direction = (-1,0,0)
  Length = 9.3
  Length2 = 10
  Profile = -> Sketch040
  ReferenceAxis = -> Sketch040 [N_Axis]
  Type = 0
FEATURE [PartDesign::Fillet] Fillet004
  Base = -> Pad040 [Edge36,Edge40]
  BaseFeature = -> Pad040
  Radius = 1.2
  SupportTransform = false
  UseAllEdges = false
FEATURE [PartDesign::Body] Body008  label="switch004"
  Group = -> [Sketch036,Pad036,Sketch037,Pad037,Sketch038,Pad038,Sketch039,Pad039,Sketch040,Pad040,Fillet004]
  Origin = -> Origin008
  Placement = pos=(122.3,0,-97) rot=(0,1,0;1.5708rad)
  Tip = -> Fillet004
FEATURE [Sketcher::SketchObject] Sketch041
  FullyConstrained = true
  MapMode = 5
  Support = -> [XY_Plane009]
  sketch-geometry (12):
    g0: Circle CenterX=10.8779 CenterY=-4.825 CenterZ=0 NormalX=0 NormalY=0 NormalZ=1 AngleXU=0 Radius=1.35
    g1: Circle CenterX=-10.8779 CenterY=4.825 CenterZ=0 NormalX=0 NormalY=0 NormalZ=1 AngleXU=0 Radius=1.35
    g2: ArcOfCircle CenterX=-12.25 CenterY=6.25 CenterZ=0 NormalX=0 NormalY=0 NormalZ=1 AngleXU=0 Radius=1.75 StartAngle=1.5708 EndAngle=3.14159
    g3: LineSegment StartX=-12.25 StartY=8 StartZ=0 EndX=12.25 EndY=8 EndZ=0
    g4: ArcOfCircle CenterX=12.25 CenterY=6.25 CenterZ=0 NormalX=0 NormalY=0 NormalZ=1 AngleXU=0 Radius=1.75 StartAngle=3e-16 EndAngle=1.5708
    g5: LineSegment StartX=14 StartY=6.25 StartZ=0 EndX=14 EndY=-6.25 EndZ=0
    g6: ArcOfCircle CenterX=12.25 CenterY=-6.25 CenterZ=0 NormalX=0 NormalY=0 NormalZ=1 AngleXU=0 Radius=1.75 StartAngle=4.71239 EndAngle=6.28319
    g7: LineSegment StartX=12.25 StartY=-8 StartZ=0 EndX=-12.25 EndY=-8 EndZ=0
    g8: ArcOfCircle CenterX=-12.25 CenterY=-6.25 CenterZ=0 NormalX=0 NormalY=0 NormalZ=1 AngleXU=0 Radius=1.75 StartAngle=3.14159 EndAngle=4.71239
    g9: LineSegment StartX=-14 StartY=-6.25 StartZ=0 EndX=-14 EndY=6.25 EndZ=0
    g10: GeomPoint X=-14 Y=8 Z=0
    g11: GeomPoint X=14 Y=-8 Z=0
  constraints (28):
    c: Tangent(g2,g3) = 1.5708
    c: Tangent(g3,g4) = 1.5708
    c: Tangent(g4,g5) = 1.5708
    c: Tangent(g5,g6) = 1.5708
    c: Tangent(g6,g7) = 1.5708
    c: Tangent(g7,g8) = 1.5708
    c: Tangent(g8,g9) = 1.5708
    c: Tangent(g9,g2) = 1.5708
    c: Horizontal(g3)
    c: Horizontal(g7)
    c: Vertical(g5)
    c: Vertical(g9)
    c: Equal(g2,g4)
    c: Equal(g4,g6)
    c: Equal(g6,g8)
    c: PointOnObject(g10,g3)
    c: PointOnObject(g10,g9)
    c: PointOnObject(g11,g5)
    c: PointOnObject(g11,g7)
    c: DistanceX(g2,g4) = 28
    c: DistanceY(g7,g2) = 16
    c: Symmetric(g8,g4,g-1)
    c: Diameter(g2) = 3.5
    c: Symmetric(g0,g1,g-1)
    c: Diameter(g1) = 2.7
    c: Diameter(g0) = 2.7
    c: DistanceY(g0,g1) = 9.65
    c: Distance(g1,g0) = 23.8
FEATURE [PartDesign::Pad] Pad041
  Direction = (0,0,1)
  Length = 9.7
  Length2 = 10
  Profile = -> Sketch041
  ReferenceAxis = -> Sketch041 [N_Axis]
  Type = 0
FEATURE [Sketcher::SketchObject] Sketch042
  FullyConstrained = true
  MapMode = 5
  Placement = pos=(0,8,0) rot=(0,0.707107,0.707107;3.14159rad)
  Support = -> [Pad041]
  sketch-geometry (4):
    g0: LineSegment StartX=-10.9 StartY=6.9 StartZ=0 EndX=-8 EndY=6.9 EndZ=0
    g1: LineSegment StartX=-8 StartY=6.9 StartZ=0 EndX=-8 EndY=2.8 EndZ=0
    g2: LineSegment StartX=-8 StartY=2.8 StartZ=0 EndX=-10.9 EndY=2.8 EndZ=0
    g3: LineSegment StartX=-10.9 StartY=2.8 StartZ=0 EndX=-10.9 EndY=6.9 EndZ=0
  constraints (12):
    c: Coincident(g0,g1)
    c: Coincident(g1,g2)
    c: Coincident(g2,g3)
    c: Coincident(g3,g0)
    c: Horizontal(g0)
    c: Horizontal(g2)
    c: Vertical(g1)
    c: Vertical(g3)
    c: DistanceX(g0,g0) = 2.9
    c: DistanceY(g3,g3) = 4.1
    c: DistanceY(g-1,g1) = 2.8
    c: DistanceX(g2,g-1) = 10.9
FEATURE [PartDesign::Pad] Pad042
  BaseFeature = -> Pad041
  Direction = (0,1,-2e-16)
  Length = 3
  Length2 = 10
  Profile = -> Sketch042
  ReferenceAxis = -> Sketch042 [N_Axis]
  Type = 0
FEATURE [Sketcher::SketchObject] Sketch043
  FullyConstrained = true
  MapMode = 5
  Placement = pos=(-14,0,0) rot=(0.57735,-0.57735,-0.57735;2.0944rad)
  Support = -> [Pad042]
  sketch-geometry (4):
    g0: LineSegment StartX=3.9 StartY=1.65 StartZ=0 EndX=4.7 EndY=1.65 EndZ=0
    g1: LineSegment StartX=4.7 StartY=1.65 StartZ=0 EndX=4.7 EndY=8.05 EndZ=0
    g2: LineSegment StartX=4.7 StartY=8.05 StartZ=0 EndX=3.9 EndY=8.05 EndZ=0
    g3: LineSegment StartX=3.9 StartY=8.05 StartZ=0 EndX=3.9 EndY=1.65 EndZ=0
  constraints (12):
    c: Coincident(g0,g1)
    c: Coincident(g1,g2)
    c: Coincident(g2,g3)
    c: Coincident(g3,g0)
    c: Horizontal(g0)
    c: Horizontal(g2)
    c: Vertical(g1)
    c: Vertical(g3)
    c: DistanceX(g2,g2) = 0.8
    c: DistanceY(g3,g3) = 6.4
    c: DistanceY(g-1,g0) = 1.65
    c: DistanceX(g-1,g0) = 4.7
FEATURE [PartDesign::Pad] Pad043
  BaseFeature = -> Pad042
  Direction = (-1,0,0)
  Length = 10
  Length2 = 10
  Profile = -> Sketch043
  ReferenceAxis = -> Sketch043 [N_Axis]
  Type = 0
FEATURE [Sketcher::SketchObject] Sketch044
  FullyConstrained = true
  MapMode = 5
  Placement = pos=(0,-8,0) rot=(1,0,0;1.5708rad)
  Support = -> [Pad043]
  sketch-geometry (4):
    g0: LineSegment StartX=-1.3 StartY=8.05 StartZ=0 EndX=-0.5 EndY=8.05 EndZ=0
    g1: LineSegment StartX=-0.5 StartY=8.05 StartZ=0 EndX=-0.5 EndY=1.65 EndZ=0
    g2: LineSegment StartX=-0.5 StartY=1.65 StartZ=0 EndX=-1.3 EndY=1.65 EndZ=0
    g3: LineSegment StartX=-1.3 StartY=1.65 StartZ=0 EndX=-1.3 EndY=8.05 EndZ=0
  constraints (12):
    c: Coincident(g0,g1)
    c: Coincident(g1,g2)
    c: Coincident(g2,g3)
    c: Coincident(g3,g0)
    c: Horizontal(g0)
    c: Horizontal(g2)
    c: Vertical(g1)
    c: Vertical(g3)
    c: DistanceY(g1,g1) = 6.4
    c: DistanceX(g0,g0) = 0.8
    c: DistanceY(g-1,g1) = 1.65
    c: DistanceX(g1,g-1) = 0.5
FEATURE [PartDesign::Pad] Pad044
  BaseFeature = -> Pad043
  Direction = (0,-1,2e-16)
  Length = 3
  Length2 = 10
  Profile = -> Sketch044
  ReferenceAxis = -> Sketch044 [N_Axis]
  Type = 0
FEATURE [Sketcher::SketchObject] Sketch045
  FullyConstrained = true
  MapMode = 5
  Placement = pos=(-1.3,0,0) rot=(0.57735,-0.57735,-0.57735;2.0944rad)
  Support = -> [Pad044]
  sketch-geometry (4):
    g0: LineSegment StartX=10.2 StartY=8.05 StartZ=0 EndX=11 EndY=8.05 EndZ=0
    g1: LineSegment StartX=11 StartY=8.05 StartZ=0 EndX=11 EndY=1.65 EndZ=0
    g2: LineSegment StartX=11 StartY=1.65 StartZ=0 EndX=10.2 EndY=1.65 EndZ=0
    g3: LineSegment StartX=10.2 StartY=1.65 StartZ=0 EndX=10.2 EndY=8.05 EndZ=0
  constraints (12):
    c: Coincident(g0,g1)
    c: Coincident(g1,g2)
    c: Coincident(g2,g3)
    c: Coincident(g3,g0)
    c: Horizontal(g0)
    c: Horizontal(g2)
    c: Vertical(g1)
    c: Vertical(g3)
    c: DistanceX(g0,g0) = 0.8
    c: DistanceY(g1,g1) = 6.4
    c: DistanceY(g-1,g2) = 1.65
    c: DistanceX(g-1,g2) = 10.2
FEATURE [PartDesign::Pad] Pad045
  BaseFeature = -> Pad044
  Direction = (-1,0,0)
  Length = 9.3
  Length2 = 10
  Profile = -> Sketch045
  ReferenceAxis = -> Sketch045 [N_Axis]
  Type = 0
FEATURE [PartDesign::Fillet] Fillet005
  Base = -> Pad045 [Edge36,Edge40]
  BaseFeature = -> Pad045
  Radius = 1.2
  SupportTransform = false
  UseAllEdges = false
FEATURE [PartDesign::Body] Body009  label="switch005"
  Group = -> [Sketch041,Pad041,Sketch042,Pad042,Sketch043,Pad043,Sketch044,Pad044,Sketch045,Pad045,Fillet005]
  Origin = -> Origin009
  Placement = pos=(145.8,0,-97) rot=(0,1,0;1.5708rad)
  Tip = -> Fillet005
FEATURE [Sketcher::SketchObject] Sketch046
  FullyConstrained = true
  MapMode = 5
  Support = -> [XY_Plane010]
  sketch-geometry (12):
    g0: Circle CenterX=10.8779 CenterY=-4.825 CenterZ=0 NormalX=0 NormalY=0 NormalZ=1 AngleXU=0 Radius=1.35
    g1: Circle CenterX=-10.8779 CenterY=4.825 CenterZ=0 NormalX=0 NormalY=0 NormalZ=1 AngleXU=0 Radius=1.35
    g2: ArcOfCircle CenterX=-12.25 CenterY=6.25 CenterZ=0 NormalX=0 NormalY=0 NormalZ=1 AngleXU=0 Radius=1.75 StartAngle=1.5708 EndAngle=3.14159
    g3: LineSegment StartX=-12.25 StartY=8 StartZ=0 EndX=12.25 EndY=8 EndZ=0
    g4: ArcOfCircle CenterX=12.25 CenterY=6.25 CenterZ=0 NormalX=0 NormalY=0 NormalZ=1 AngleXU=0 Radius=1.75 StartAngle=3e-16 EndAngle=1.5708
    g5: LineSegment StartX=14 StartY=6.25 StartZ=0 EndX=14 EndY=-6.25 EndZ=0
    g6: ArcOfCircle CenterX=12.25 CenterY=-6.25 CenterZ=0 NormalX=0 NormalY=0 NormalZ=1 AngleXU=0 Radius=1.75 StartAngle=4.71239 EndAngle=6.28319
    g7: LineSegment StartX=12.25 StartY=-8 StartZ=0 EndX=-12.25 EndY=-8 EndZ=0
    g8: ArcOfCircle CenterX=-12.25 CenterY=-6.25 CenterZ=0 NormalX=0 NormalY=0 NormalZ=1 AngleXU=0 Radius=1.75 StartAngle=3.14159 EndAngle=4.71239
    g9: LineSegment StartX=-14 StartY=-6.25 StartZ=0 EndX=-14 EndY=6.25 EndZ=0
    g10: GeomPoint X=-14 Y=8 Z=0
    g11: GeomPoint X=14 Y=-8 Z=0
  constraints (28):
    c: Tangent(g2,g3) = 1.5708
    c: Tangent(g3,g4) = 1.5708
    c: Tangent(g4,g5) = 1.5708
    c: Tangent(g5,g6) = 1.5708
    c: Tangent(g6,g7) = 1.5708
    c: Tangent(g7,g8) = 1.5708
    c: Tangent(g8,g9) = 1.5708
    c: Tangent(g9,g2) = 1.5708
    c: Horizontal(g3)
    c: Horizontal(g7)
    c: Vertical(g5)
    c: Vertical(g9)
    c: Equal(g2,g4)
    c: Equal(g4,g6)
    c: Equal(g6,g8)
    c: PointOnObject(g10,g3)
    c: PointOnObject(g10,g9)
    c: PointOnObject(g11,g5)
    c: PointOnObject(g11,g7)
    c: DistanceX(g2,g4) = 28
    c: DistanceY(g7,g2) = 16
    c: Symmetric(g8,g4,g-1)
    c: Diameter(g2) = 3.5
    c: Symmetric(g0,g1,g-1)
    c: Diameter(g1) = 2.7
    c: Diameter(g0) = 2.7
    c: DistanceY(g0,g1) = 9.65
    c: Distance(g1,g0) = 23.8
FEATURE [PartDesign::Pad] Pad046
  Direction = (0,0,1)
  Length = 9.7
  Length2 = 10
  Profile = -> Sketch046
  ReferenceAxis = -> Sketch046 [N_Axis]
  Type = 0
FEATURE [Sketcher::SketchObject] Sketch047
  FullyConstrained = true
  MapMode = 5
  Placement = pos=(0,8,0) rot=(0,0.707107,0.707107;3.14159rad)
  Support = -> [Pad046]
  sketch-geometry (4):
    g0: LineSegment StartX=-10.9 StartY=6.9 StartZ=0 EndX=-8 EndY=6.9 EndZ=0
    g1: LineSegment StartX=-8 StartY=6.9 StartZ=0 EndX=-8 EndY=2.8 EndZ=0
    g2: LineSegment StartX=-8 StartY=2.8 StartZ=0 EndX=-10.9 EndY=2.8 EndZ=0
    g3: LineSegment StartX=-10.9 StartY=2.8 StartZ=0 EndX=-10.9 EndY=6.9 EndZ=0
  constraints (12):
    c: Coincident(g0,g1)
    c: Coincident(g1,g2)
    c: Coincident(g2,g3)
    c: Coincident(g3,g0)
    c: Horizontal(g0)
    c: Horizontal(g2)
    c: Vertical(g1)
    c: Vertical(g3)
    c: DistanceX(g0,g0) = 2.9
    c: DistanceY(g3,g3) = 4.1
    c: DistanceY(g-1,g1) = 2.8
    c: DistanceX(g2,g-1) = 10.9
FEATURE [PartDesign::Pad] Pad047
  BaseFeature = -> Pad046
  Direction = (0,1,-2e-16)
  Length = 3
  Length2 = 10
  Profile = -> Sketch047
  ReferenceAxis = -> Sketch047 [N_Axis]
  Type = 0
FEATURE [Sketcher::SketchObject] Sketch048
  FullyConstrained = true
  MapMode = 5
  Placement = pos=(-14,0,0) rot=(0.57735,-0.57735,-0.57735;2.0944rad)
  Support = -> [Pad047]
  sketch-geometry (4):
    g0: LineSegment StartX=3.9 StartY=1.65 StartZ=0 EndX=4.7 EndY=1.65 EndZ=0
    g1: LineSegment StartX=4.7 StartY=1.65 StartZ=0 EndX=4.7 EndY=8.05 EndZ=0
    g2: LineSegment StartX=4.7 StartY=8.05 StartZ=0 EndX=3.9 EndY=8.05 EndZ=0
    g3: LineSegment StartX=3.9 StartY=8.05 StartZ=0 EndX=3.9 EndY=1.65 EndZ=0
  constraints (12):
    c: Coincident(g0,g1)
    c: Coincident(g1,g2)
    c: Coincident(g2,g3)
    c: Coincident(g3,g0)
    c: Horizontal(g0)
    c: Horizontal(g2)
    c: Vertical(g1)
    c: Vertical(g3)
    c: DistanceX(g2,g2) = 0.8
    c: DistanceY(g3,g3) = 6.4
    c: DistanceY(g-1,g0) = 1.65
    c: DistanceX(g-1,g0) = 4.7
FEATURE [PartDesign::Pad] Pad048
  BaseFeature = -> Pad047
  Direction = (-1,0,0)
  Length = 10
  Length2 = 10
  Profile = -> Sketch048
  ReferenceAxis = -> Sketch048 [N_Axis]
  Type = 0
FEATURE [Sketcher::SketchObject] Sketch049
  FullyConstrained = true
  MapMode = 5
  Placement = pos=(0,-8,0) rot=(1,0,0;1.5708rad)
  Support = -> [Pad048]
  sketch-geometry (4):
    g0: LineSegment StartX=-1.3 StartY=8.05 StartZ=0 EndX=-0.5 EndY=8.05 EndZ=0
    g1: LineSegment StartX=-0.5 StartY=8.05 StartZ=0 EndX=-0.5 EndY=1.65 EndZ=0
    g2: LineSegment StartX=-0.5 StartY=1.65 StartZ=0 EndX=-1.3 EndY=1.65 EndZ=0
    g3: LineSegment StartX=-1.3 StartY=1.65 StartZ=0 EndX=-1.3 EndY=8.05 EndZ=0
  constraints (12):
    c: Coincident(g0,g1)
    c: Coincident(g1,g2)
    c: Coincident(g2,g3)
    c: Coincident(g3,g0)
    c: Horizontal(g0)
    c: Horizontal(g2)
    c: Vertical(g1)
    c: Vertical(g3)
    c: DistanceY(g1,g1) = 6.4
    c: DistanceX(g0,g0) = 0.8
    c: DistanceY(g-1,g1) = 1.65
    c: DistanceX(g1,g-1) = 0.5
FEATURE [PartDesign::Pad] Pad049
  BaseFeature = -> Pad048
  Direction = (0,-1,2e-16)
  Length = 3
  Length2 = 10
  Profile = -> Sketch049
  ReferenceAxis = -> Sketch049 [N_Axis]
  Type = 0
FEATURE [Sketcher::SketchObject] Sketch050
  FullyConstrained = true
  MapMode = 5
  Placement = pos=(-1.3,0,0) rot=(0.57735,-0.57735,-0.57735;2.0944rad)
  Support = -> [Pad049]
  sketch-geometry (4):
    g0: LineSegment StartX=10.2 StartY=8.05 StartZ=0 EndX=11 EndY=8.05 EndZ=0
    g1: LineSegment StartX=11 StartY=8.05 StartZ=0 EndX=11 EndY=1.65 EndZ=0
    g2: LineSegment StartX=11 StartY=1.65 StartZ=0 EndX=10.2 EndY=1.65 EndZ=0
    g3: LineSegment StartX=10.2 StartY=1.65 StartZ=0 EndX=10.2 EndY=8.05 EndZ=0
  constraints (12):
    c: Coincident(g0,g1)
    c: Coincident(g1,g2)
    c: Coincident(g2,g3)
    c: Coincident(g3,g0)
    c: Horizontal(g0)
    c: Horizontal(g2)
    c: Vertical(g1)
    c: Vertical(g3)
    c: DistanceX(g0,g0) = 0.8
    c: DistanceY(g1,g1) = 6.4
    c: DistanceY(g-1,g2) = 1.65
    c: DistanceX(g-1,g2) = 10.2
FEATURE [PartDesign::Pad] Pad050
  BaseFeature = -> Pad049
  Direction = (-1,0,0)
  Length = 9.3
  Length2 = 10
  Profile = -> Sketch050
  ReferenceAxis = -> Sketch050 [N_Axis]
  Type = 0
FEATURE [PartDesign::Fillet] Fillet006
  Base = -> Pad050 [Edge36,Edge40]
  BaseFeature = -> Pad050
  Radius = 1.2
  SupportTransform = false
  UseAllEdges = false
FEATURE [PartDesign::Body] Body010  label="switch006"
  Group = -> [Sketch046,Pad046,Sketch047,Pad047,Sketch048,Pad048,Sketch049,Pad049,Sketch050,Pad050,Fillet006]
  Origin = -> Origin010
  Placement = pos=(169.3,0,-97) rot=(0,1,0;1.5708rad)
  Tip = -> Fillet006
FEATURE [Sketcher::SketchObject] Sketch051
  FullyConstrained = true
  MapMode = 5
  Support = -> [XY_Plane011]
  sketch-geometry (12):
    g0: Circle CenterX=10.8779 CenterY=-4.825 CenterZ=0 NormalX=0 NormalY=0 NormalZ=1 AngleXU=0 Radius=1.35
    g1: Circle CenterX=-10.8779 CenterY=4.825 CenterZ=0 NormalX=0 NormalY=0 NormalZ=1 AngleXU=0 Radius=1.35
    g2: ArcOfCircle CenterX=-12.25 CenterY=6.25 CenterZ=0 NormalX=0 NormalY=0 NormalZ=1 AngleXU=0 Radius=1.75 StartAngle=1.5708 EndAngle=3.14159
    g3: LineSegment StartX=-12.25 StartY=8 StartZ=0 EndX=12.25 EndY=8 EndZ=0
    g4: ArcOfCircle CenterX=12.25 CenterY=6.25 CenterZ=0 NormalX=0 NormalY=0 NormalZ=1 AngleXU=0 Radius=1.75 StartAngle=3e-16 EndAngle=1.5708
    g5: LineSegment StartX=14 StartY=6.25 StartZ=0 EndX=14 EndY=-6.25 EndZ=0
    g6: ArcOfCircle CenterX=12.25 CenterY=-6.25 CenterZ=0 NormalX=0 NormalY=0 NormalZ=1 AngleXU=0 Radius=1.75 StartAngle=4.71239 EndAngle=6.28319
    g7: LineSegment StartX=12.25 StartY=-8 StartZ=0 EndX=-12.25 EndY=-8 EndZ=0
    g8: ArcOfCircle CenterX=-12.25 CenterY=-6.25 CenterZ=0 NormalX=0 NormalY=0 NormalZ=1 AngleXU=0 Radius=1.75 StartAngle=3.14159 EndAngle=4.71239
    g9: LineSegment StartX=-14 StartY=-6.25 StartZ=0 EndX=-14 EndY=6.25 EndZ=0
    g10: GeomPoint X=-14 Y=8 Z=0
    g11: GeomPoint X=14 Y=-8 Z=0
  constraints (28):
    c: Tangent(g2,g3) = 1.5708
    c: Tangent(g3,g4) = 1.5708
    c: Tangent(g4,g5) = 1.5708
    c: Tangent(g5,g6) = 1.5708
    c: Tangent(g6,g7) = 1.5708
    c: Tangent(g7,g8) = 1.5708
    c: Tangent(g8,g9) = 1.5708
    c: Tangent(g9,g2) = 1.5708
    c: Horizontal(g3)
    c: Horizontal(g7)
    c: Vertical(g5)
    c: Vertical(g9)
    c: Equal(g2,g4)
    c: Equal(g4,g6)
    c: Equal(g6,g8)
    c: PointOnObject(g10,g3)
    c: PointOnObject(g10,g9)
    c: PointOnObject(g11,g5)
    c: PointOnObject(g11,g7)
    c: DistanceX(g2,g4) = 28
    c: DistanceY(g7,g2) = 16
    c: Symmetric(g8,g4,g-1)
    c: Diameter(g2) = 3.5
    c: Symmetric(g0,g1,g-1)
    c: Diameter(g1) = 2.7
    c: Diameter(g0) = 2.7
    c: DistanceY(g0,g1) = 9.65
    c: Distance(g1,g0) = 23.8
FEATURE [PartDesign::Pad] Pad051
  Direction = (0,0,1)
  Length = 9.7
  Length2 = 10
  Profile = -> Sketch051
  ReferenceAxis = -> Sketch051 [N_Axis]
  Type = 0
FEATURE [Sketcher::SketchObject] Sketch052
  FullyConstrained = true
  MapMode = 5
  Placement = pos=(0,8,0) rot=(0,0.707107,0.707107;3.14159rad)
  Support = -> [Pad051]
  sketch-geometry (4):
    g0: LineSegment StartX=-10.9 StartY=6.9 StartZ=0 EndX=-8 EndY=6.9 EndZ=0
    g1: LineSegment StartX=-8 StartY=6.9 StartZ=0 EndX=-8 EndY=2.8 EndZ=0
    g2: LineSegment StartX=-8 StartY=2.8 StartZ=0 EndX=-10.9 EndY=2.8 EndZ=0
    g3: LineSegment StartX=-10.9 StartY=2.8 StartZ=0 EndX=-10.9 EndY=6.9 EndZ=0
  constraints (12):
    c: Coincident(g0,g1)
    c: Coincident(g1,g2)
    c: Coincident(g2,g3)
    c: Coincident(g3,g0)
    c: Horizontal(g0)
    c: Horizontal(g2)
    c: Vertical(g1)
    c: Vertical(g3)
    c: DistanceX(g0,g0) = 2.9
    c: DistanceY(g3,g3) = 4.1
    c: DistanceY(g-1,g1) = 2.8
    c: DistanceX(g2,g-1) = 10.9
FEATURE [PartDesign::Pad] Pad052
  BaseFeature = -> Pad051
  Direction = (0,1,-2e-16)
  Length = 3
  Length2 = 10
  Profile = -> Sketch052
  ReferenceAxis = -> Sketch052 [N_Axis]
  Type = 0
FEATURE [Sketcher::SketchObject] Sketch053
  FullyConstrained = true
  MapMode = 5
  Placement = pos=(-14,0,0) rot=(0.57735,-0.57735,-0.57735;2.0944rad)
  Support = -> [Pad052]
  sketch-geometry (4):
    g0: LineSegment StartX=3.9 StartY=1.65 StartZ=0 EndX=4.7 EndY=1.65 EndZ=0
    g1: LineSegment StartX=4.7 StartY=1.65 StartZ=0 EndX=4.7 EndY=8.05 EndZ=0
    g2: LineSegment StartX=4.7 StartY=8.05 StartZ=0 EndX=3.9 EndY=8.05 EndZ=0
    g3: LineSegment StartX=3.9 StartY=8.05 StartZ=0 EndX=3.9 EndY=1.65 EndZ=0
  constraints (12):
    c: Coincident(g0,g1)
    c: Coincident(g1,g2)
    c: Coincident(g2,g3)
    c: Coincident(g3,g0)
    c: Horizontal(g0)
    c: Horizontal(g2)
    c: Vertical(g1)
    c: Vertical(g3)
    c: DistanceX(g2,g2) = 0.8
    c: DistanceY(g3,g3) = 6.4
    c: DistanceY(g-1,g0) = 1.65
    c: DistanceX(g-1,g0) = 4.7
FEATURE [PartDesign::Pad] Pad053
  BaseFeature = -> Pad052
  Direction = (-1,0,0)
  Length = 10
  Length2 = 10
  Profile = -> Sketch053
  ReferenceAxis = -> Sketch053 [N_Axis]
  Type = 0
FEATURE [Sketcher::SketchObject] Sketch054
  FullyConstrained = true
  MapMode = 5
  Placement = pos=(0,-8,0) rot=(1,0,0;1.5708rad)
  Support = -> [Pad053]
  sketch-geometry (4):
    g0: LineSegment StartX=-1.3 StartY=8.05 StartZ=0 EndX=-0.5 EndY=8.05 EndZ=0
    g1: LineSegment StartX=-0.5 StartY=8.05 StartZ=0 EndX=-0.5 EndY=1.65 EndZ=0
    g2: LineSegment StartX=-0.5 StartY=1.65 StartZ=0 EndX=-1.3 EndY=1.65 EndZ=0
    g3: LineSegment StartX=-1.3 StartY=1.65 StartZ=0 EndX=-1.3 EndY=8.05 EndZ=0
  constraints (12):
    c: Coincident(g0,g1)
    c: Coincident(g1,g2)
    c: Coincident(g2,g3)
    c: Coincident(g3,g0)
    c: Horizontal(g0)
    c: Horizontal(g2)
    c: Vertical(g1)
    c: Vertical(g3)
    c: DistanceY(g1,g1) = 6.4
    c: DistanceX(g0,g0) = 0.8
    c: DistanceY(g-1,g1) = 1.65
    c: DistanceX(g1,g-1) = 0.5
FEATURE [PartDesign::Pad] Pad054
  BaseFeature = -> Pad053
  Direction = (0,-1,2e-16)
  Length = 3
  Length2 = 10
  Profile = -> Sketch054
  ReferenceAxis = -> Sketch054 [N_Axis]
  Type = 0
FEATURE [Sketcher::SketchObject] Sketch055
  FullyConstrained = true
  MapMode = 5
  Placement = pos=(-1.3,0,0) rot=(0.57735,-0.57735,-0.57735;2.0944rad)
  Support = -> [Pad054]
  sketch-geometry (4):
    g0: LineSegment StartX=10.2 StartY=8.05 StartZ=0 EndX=11 EndY=8.05 EndZ=0
    g1: LineSegment StartX=11 StartY=8.05 StartZ=0 EndX=11 EndY=1.65 EndZ=0
    g2: LineSegment StartX=11 StartY=1.65 StartZ=0 EndX=10.2 EndY=1.65 EndZ=0
    g3: LineSegment StartX=10.2 StartY=1.65 StartZ=0 EndX=10.2 EndY=8.05 EndZ=0
  constraints (12):
    c: Coincident(g0,g1)
    c: Coincident(g1,g2)
    c: Coincident(g2,g3)
    c: Coincident(g3,g0)
    c: Horizontal(g0)
    c: Horizontal(g2)
    c: Vertical(g1)
    c: Vertical(g3)
    c: DistanceX(g0,g0) = 0.8
    c: DistanceY(g1,g1) = 6.4
    c: DistanceY(g-1,g2) = 1.65
    c: DistanceX(g-1,g2) = 10.2
FEATURE [PartDesign::Pad] Pad055
  BaseFeature = -> Pad054
  Direction = (-1,0,0)
  Length = 9.3
  Length2 = 10
  Profile = -> Sketch055
  ReferenceAxis = -> Sketch055 [N_Axis]
  Type = 0
FEATURE [PartDesign::Fillet] Fillet007
  Base = -> Pad055 [Edge36,Edge40]
  BaseFeature = -> Pad055
  Radius = 1.2
  SupportTransform = false
  UseAllEdges = false
FEATURE [PartDesign::Body] Body011  label="switch007"
  Group = -> [Sketch051,Pad051,Sketch052,Pad052,Sketch053,Pad053,Sketch054,Pad054,Sketch055,Pad055,Fillet007]
  Origin = -> Origin011
  Placement = pos=(192.8,0,-97) rot=(0,1,0;1.5708rad)
  Tip = -> Fillet007
FEATURE [Sketcher::SketchObject] Sketch056
  FullyConstrained = true
  MapMode = 5
  Support = -> [XY_Plane012]
  sketch-geometry (12):
    g0: Circle CenterX=10.8779 CenterY=-4.825 CenterZ=0 NormalX=0 NormalY=0 NormalZ=1 AngleXU=0 Radius=1.35
    g1: Circle CenterX=-10.8779 CenterY=4.825 CenterZ=0 NormalX=0 NormalY=0 NormalZ=1 AngleXU=0 Radius=1.35
    g2: ArcOfCircle CenterX=-12.25 CenterY=6.25 CenterZ=0 NormalX=0 NormalY=0 NormalZ=1 AngleXU=0 Radius=1.75 StartAngle=1.5708 EndAngle=3.14159
    g3: LineSegment StartX=-12.25 StartY=8 StartZ=0 EndX=12.25 EndY=8 EndZ=0
    g4: ArcOfCircle CenterX=12.25 CenterY=6.25 CenterZ=0 NormalX=0 NormalY=0 NormalZ=1 AngleXU=0 Radius=1.75 StartAngle=3e-16 EndAngle=1.5708
    g5: LineSegment StartX=14 StartY=6.25 StartZ=0 EndX=14 EndY=-6.25 EndZ=0
    g6: ArcOfCircle CenterX=12.25 CenterY=-6.25 CenterZ=0 NormalX=0 NormalY=0 NormalZ=1 AngleXU=0 Radius=1.75 StartAngle=4.71239 EndAngle=6.28319
    g7: LineSegment StartX=12.25 StartY=-8 StartZ=0 EndX=-12.25 EndY=-8 EndZ=0
    g8: ArcOfCircle CenterX=-12.25 CenterY=-6.25 CenterZ=0 NormalX=0 NormalY=0 NormalZ=1 AngleXU=0 Radius=1.75 StartAngle=3.14159 EndAngle=4.71239
    g9: LineSegment StartX=-14 StartY=-6.25 StartZ=0 EndX=-14 EndY=6.25 EndZ=0
    g10: GeomPoint X=-14 Y=8 Z=0
    g11: GeomPoint X=14 Y=-8 Z=0
  constraints (28):
    c: Tangent(g2,g3) = 1.5708
    c: Tangent(g3,g4) = 1.5708
    c: Tangent(g4,g5) = 1.5708
    c: Tangent(g5,g6) = 1.5708
    c: Tangent(g6,g7) = 1.5708
    c: Tangent(g7,g8) = 1.5708
    c: Tangent(g8,g9) = 1.5708
    c: Tangent(g9,g2) = 1.5708
    c: Horizontal(g3)
    c: Horizontal(g7)
    c: Vertical(g5)
    c: Vertical(g9)
    c: Equal(g2,g4)
    c: Equal(g4,g6)
    c: Equal(g6,g8)
    c: PointOnObject(g10,g3)
    c: PointOnObject(g10,g9)
    c: PointOnObject(g11,g5)
    c: PointOnObject(g11,g7)
    c: DistanceX(g2,g4) = 28
    c: DistanceY(g7,g2) = 16
    c: Symmetric(g8,g4,g-1)
    c: Diameter(g2) = 3.5
    c: Symmetric(g0,g1,g-1)
    c: Diameter(g1) = 2.7
    c: Diameter(g0) = 2.7
    c: DistanceY(g0,g1) = 9.65
    c: Distance(g1,g0) = 23.8
FEATURE [PartDesign::Pad] Pad056
  Direction = (0,0,1)
  Length = 9.7
  Length2 = 10
  Profile = -> Sketch056
  ReferenceAxis = -> Sketch056 [N_Axis]
  Type = 0
FEATURE [Sketcher::SketchObject] Sketch057
  FullyConstrained = true
  MapMode = 5
  Placement = pos=(0,8,0) rot=(0,0.707107,0.707107;3.14159rad)
  Support = -> [Pad056]
  sketch-geometry (4):
    g0: LineSegment StartX=-10.9 StartY=6.9 StartZ=0 EndX=-8 EndY=6.9 EndZ=0
    g1: LineSegment StartX=-8 StartY=6.9 StartZ=0 EndX=-8 EndY=2.8 EndZ=0
    g2: LineSegment StartX=-8 StartY=2.8 StartZ=0 EndX=-10.9 EndY=2.8 EndZ=0
    g3: LineSegment StartX=-10.9 StartY=2.8 StartZ=0 EndX=-10.9 EndY=6.9 EndZ=0
  constraints (12):
    c: Coincident(g0,g1)
    c: Coincident(g1,g2)
    c: Coincident(g2,g3)
    c: Coincident(g3,g0)
    c: Horizontal(g0)
    c: Horizontal(g2)
    c: Vertical(g1)
    c: Vertical(g3)
    c: DistanceX(g0,g0) = 2.9
    c: DistanceY(g3,g3) = 4.1
    c: DistanceY(g-1,g1) = 2.8
    c: DistanceX(g2,g-1) = 10.9
FEATURE [PartDesign::Pad] Pad057
  BaseFeature = -> Pad056
  Direction = (0,1,-2e-16)
  Length = 3
  Length2 = 10
  Profile = -> Sketch057
  ReferenceAxis = -> Sketch057 [N_Axis]
  Type = 0
FEATURE [Sketcher::SketchObject] Sketch058
  FullyConstrained = true
  MapMode = 5
  Placement = pos=(-14,0,0) rot=(0.57735,-0.57735,-0.57735;2.0944rad)
  Support = -> [Pad057]
  sketch-geometry (4):
    g0: LineSegment StartX=3.9 StartY=1.65 StartZ=0 EndX=4.7 EndY=1.65 EndZ=0
    g1: LineSegment StartX=4.7 StartY=1.65 StartZ=0 EndX=4.7 EndY=8.05 EndZ=0
    g2: LineSegment StartX=4.7 StartY=8.05 StartZ=0 EndX=3.9 EndY=8.05 EndZ=0
    g3: LineSegment StartX=3.9 StartY=8.05 StartZ=0 EndX=3.9 EndY=1.65 EndZ=0
  constraints (12):
    c: Coincident(g0,g1)
    c: Coincident(g1,g2)
    c: Coincident(g2,g3)
    c: Coincident(g3,g0)
    c: Horizontal(g0)
    c: Horizontal(g2)
    c: Vertical(g1)
    c: Vertical(g3)
    c: DistanceX(g2,g2) = 0.8
    c: DistanceY(g3,g3) = 6.4
    c: DistanceY(g-1,g0) = 1.65
    c: DistanceX(g-1,g0) = 4.7
FEATURE [PartDesign::Pad] Pad058
  BaseFeature = -> Pad057
  Direction = (-1,0,0)
  Length = 10
  Length2 = 10
  Profile = -> Sketch058
  ReferenceAxis = -> Sketch058 [N_Axis]
  Type = 0
FEATURE [Sketcher::SketchObject] Sketch059
  FullyConstrained = true
  MapMode = 5
  Placement = pos=(0,-8,0) rot=(1,0,0;1.5708rad)
  Support = -> [Pad058]
  sketch-geometry (4):
    g0: LineSegment StartX=-1.3 StartY=8.05 StartZ=0 EndX=-0.5 EndY=8.05 EndZ=0
    g1: LineSegment StartX=-0.5 StartY=8.05 StartZ=0 EndX=-0.5 EndY=1.65 EndZ=0
    g2: LineSegment StartX=-0.5 StartY=1.65 StartZ=0 EndX=-1.3 EndY=1.65 EndZ=0
    g3: LineSegment StartX=-1.3 StartY=1.65 StartZ=0 EndX=-1.3 EndY=8.05 EndZ=0
  constraints (12):
    c: Coincident(g0,g1)
    c: Coincident(g1,g2)
    c: Coincident(g2,g3)
    c: Coincident(g3,g0)
    c: Horizontal(g0)
    c: Horizontal(g2)
    c: Vertical(g1)
    c: Vertical(g3)
    c: DistanceY(g1,g1) = 6.4
    c: DistanceX(g0,g0) = 0.8
    c: DistanceY(g-1,g1) = 1.65
    c: DistanceX(g1,g-1) = 0.5
FEATURE [PartDesign::Pad] Pad059
  BaseFeature = -> Pad058
  Direction = (0,-1,2e-16)
  Length = 3
  Length2 = 10
  Profile = -> Sketch059
  ReferenceAxis = -> Sketch059 [N_Axis]
  Type = 0
FEATURE [Sketcher::SketchObject] Sketch060
  FullyConstrained = true
  MapMode = 5
  Placement = pos=(-1.3,0,0) rot=(0.57735,-0.57735,-0.57735;2.0944rad)
  Support = -> [Pad059]
  sketch-geometry (4):
    g0: LineSegment StartX=10.2 StartY=8.05 StartZ=0 EndX=11 EndY=8.05 EndZ=0
    g1: LineSegment StartX=11 StartY=8.05 StartZ=0 EndX=11 EndY=1.65 EndZ=0
    g2: LineSegment StartX=11 StartY=1.65 StartZ=0 EndX=10.2 EndY=1.65 EndZ=0
    g3: LineSegment StartX=10.2 StartY=1.65 StartZ=0 EndX=10.2 EndY=8.05 EndZ=0
  constraints (12):
    c: Coincident(g0,g1)
    c: Coincident(g1,g2)
    c: Coincident(g2,g3)
    c: Coincident(g3,g0)
    c: Horizontal(g0)
    c: Horizontal(g2)
    c: Vertical(g1)
    c: Vertical(g3)
    c: DistanceX(g0,g0) = 0.8
    c: DistanceY(g1,g1) = 6.4
    c: DistanceY(g-1,g2) = 1.65
    c: DistanceX(g-1,g2) = 10.2
FEATURE [PartDesign::Pad] Pad060
  BaseFeature = -> Pad059
  Direction = (-1,0,0)
  Length = 9.3
  Length2 = 10
  Profile = -> Sketch060
  ReferenceAxis = -> Sketch060 [N_Axis]
  Type = 0
FEATURE [PartDesign::Fillet] Fillet008
  Base = -> Pad060 [Edge36,Edge40]
  BaseFeature = -> Pad060
  Radius = 1.2
  SupportTransform = false
  UseAllEdges = false
FEATURE [PartDesign::Body] Body012  label="switch008"
  Group = -> [Sketch056,Pad056,Sketch057,Pad057,Sketch058,Pad058,Sketch059,Pad059,Sketch060,Pad060,Fillet008]
  Origin = -> Origin012
  Placement = pos=(216.3,0,-97) rot=(0,1,0;1.5708rad)
  Tip = -> Fillet008
FEATURE [Sketcher::SketchObject] Sketch061
  FullyConstrained = true
  MapMode = 5
  Support = -> [XY_Plane013]
  sketch-geometry (12):
    g0: Circle CenterX=10.8779 CenterY=-4.825 CenterZ=0 NormalX=0 NormalY=0 NormalZ=1 AngleXU=0 Radius=1.35
    g1: Circle CenterX=-10.8779 CenterY=4.825 CenterZ=0 NormalX=0 NormalY=0 NormalZ=1 AngleXU=0 Radius=1.35
    g2: ArcOfCircle CenterX=-12.25 CenterY=6.25 CenterZ=0 NormalX=0 NormalY=0 NormalZ=1 AngleXU=0 Radius=1.75 StartAngle=1.5708 EndAngle=3.14159
    g3: LineSegment StartX=-12.25 StartY=8 StartZ=0 EndX=12.25 EndY=8 EndZ=0
    g4: ArcOfCircle CenterX=12.25 CenterY=6.25 CenterZ=0 NormalX=0 NormalY=0 NormalZ=1 AngleXU=0 Radius=1.75 StartAngle=3e-16 EndAngle=1.5708
    g5: LineSegment StartX=14 StartY=6.25 StartZ=0 EndX=14 EndY=-6.25 EndZ=0
    g6: ArcOfCircle CenterX=12.25 CenterY=-6.25 CenterZ=0 NormalX=0 NormalY=0 NormalZ=1 AngleXU=0 Radius=1.75 StartAngle=4.71239 EndAngle=6.28319
    g7: LineSegment StartX=12.25 StartY=-8 StartZ=0 EndX=-12.25 EndY=-8 EndZ=0
    g8: ArcOfCircle CenterX=-12.25 CenterY=-6.25 CenterZ=0 NormalX=0 NormalY=0 NormalZ=1 AngleXU=0 Radius=1.75 StartAngle=3.14159 EndAngle=4.71239
    g9: LineSegment StartX=-14 StartY=-6.25 StartZ=0 EndX=-14 EndY=6.25 EndZ=0
    g10: GeomPoint X=-14 Y=8 Z=0
    g11: GeomPoint X=14 Y=-8 Z=0
  constraints (28):
    c: Tangent(g2,g3) = 1.5708
    c: Tangent(g3,g4) = 1.5708
    c: Tangent(g4,g5) = 1.5708
    c: Tangent(g5,g6) = 1.5708
    c: Tangent(g6,g7) = 1.5708
    c: Tangent(g7,g8) = 1.5708
    c: Tangent(g8,g9) = 1.5708
    c: Tangent(g9,g2) = 1.5708
    c: Horizontal(g3)
    c: Horizontal(g7)
    c: Vertical(g5)
    c: Vertical(g9)
    c: Equal(g2,g4)
    c: Equal(g4,g6)
    c: Equal(g6,g8)
    c: PointOnObject(g10,g3)
    c: PointOnObject(g10,g9)
    c: PointOnObject(g11,g5)
    c: PointOnObject(g11,g7)
    c: DistanceX(g2,g4) = 28
    c: DistanceY(g7,g2) = 16
    c: Symmetric(g8,g4,g-1)
    c: Diameter(g2) = 3.5
    c: Symmetric(g0,g1,g-1)
    c: Diameter(g1) = 2.7
    c: Diameter(g0) = 2.7
    c: DistanceY(g0,g1) = 9.65
    c: Distance(g1,g0) = 23.8
FEATURE [PartDesign::Pad] Pad061
  Direction = (0,0,1)
  Length = 9.7
  Length2 = 10
  Profile = -> Sketch061
  ReferenceAxis = -> Sketch061 [N_Axis]
  Type = 0
FEATURE [Sketcher::SketchObject] Sketch062
  FullyConstrained = true
  MapMode = 5
  Placement = pos=(0,8,0) rot=(0,0.707107,0.707107;3.14159rad)
  Support = -> [Pad061]
  sketch-geometry (4):
    g0: LineSegment StartX=-10.9 StartY=6.9 StartZ=0 EndX=-8 EndY=6.9 EndZ=0
    g1: LineSegment StartX=-8 StartY=6.9 StartZ=0 EndX=-8 EndY=2.8 EndZ=0
    g2: LineSegment StartX=-8 StartY=2.8 StartZ=0 EndX=-10.9 EndY=2.8 EndZ=0
    g3: LineSegment StartX=-10.9 StartY=2.8 StartZ=0 EndX=-10.9 EndY=6.9 EndZ=0
  constraints (12):
    c: Coincident(g0,g1)
    c: Coincident(g1,g2)
    c: Coincident(g2,g3)
    c: Coincident(g3,g0)
    c: Horizontal(g0)
    c: Horizontal(g2)
    c: Vertical(g1)
    c: Vertical(g3)
    c: DistanceX(g0,g0) = 2.9
    c: DistanceY(g3,g3) = 4.1
    c: DistanceY(g-1,g1) = 2.8
    c: DistanceX(g2,g-1) = 10.9
FEATURE [PartDesign::Pad] Pad062
  BaseFeature = -> Pad061
  Direction = (0,1,-2e-16)
  Length = 3
  Length2 = 10
  Profile = -> Sketch062
  ReferenceAxis = -> Sketch062 [N_Axis]
  Type = 0
FEATURE [Sketcher::SketchObject] Sketch063
  FullyConstrained = true
  MapMode = 5
  Placement = pos=(-14,0,0) rot=(0.57735,-0.57735,-0.57735;2.0944rad)
  Support = -> [Pad062]
  sketch-geometry (4):
    g0: LineSegment StartX=3.9 StartY=1.65 StartZ=0 EndX=4.7 EndY=1.65 EndZ=0
    g1: LineSegment StartX=4.7 StartY=1.65 StartZ=0 EndX=4.7 EndY=8.05 EndZ=0
    g2: LineSegment StartX=4.7 StartY=8.05 StartZ=0 EndX=3.9 EndY=8.05 EndZ=0
    g3: LineSegment StartX=3.9 StartY=8.05 StartZ=0 EndX=3.9 EndY=1.65 EndZ=0
  constraints (12):
    c: Coincident(g0,g1)
    c: Coincident(g1,g2)
    c: Coincident(g2,g3)
    c: Coincident(g3,g0)
    c: Horizontal(g0)
    c: Horizontal(g2)
    c: Vertical(g1)
    c: Vertical(g3)
    c: DistanceX(g2,g2) = 0.8
    c: DistanceY(g3,g3) = 6.4
    c: DistanceY(g-1,g0) = 1.65
    c: DistanceX(g-1,g0) = 4.7
FEATURE [PartDesign::Pad] Pad063
  BaseFeature = -> Pad062
  Direction = (-1,0,0)
  Length = 10
  Length2 = 10
  Profile = -> Sketch063
  ReferenceAxis = -> Sketch063 [N_Axis]
  Type = 0
FEATURE [Sketcher::SketchObject] Sketch064
  FullyConstrained = true
  MapMode = 5
  Placement = pos=(0,-8,0) rot=(1,0,0;1.5708rad)
  Support = -> [Pad063]
  sketch-geometry (4):
    g0: LineSegment StartX=-1.3 StartY=8.05 StartZ=0 EndX=-0.5 EndY=8.05 EndZ=0
    g1: LineSegment StartX=-0.5 StartY=8.05 StartZ=0 EndX=-0.5 EndY=1.65 EndZ=0
    g2: LineSegment StartX=-0.5 StartY=1.65 StartZ=0 EndX=-1.3 EndY=1.65 EndZ=0
    g3: LineSegment StartX=-1.3 StartY=1.65 StartZ=0 EndX=-1.3 EndY=8.05 EndZ=0
  constraints (12):
    c: Coincident(g0,g1)
    c: Coincident(g1,g2)
    c: Coincident(g2,g3)
    c: Coincident(g3,g0)
    c: Horizontal(g0)
    c: Horizontal(g2)
    c: Vertical(g1)
    c: Vertical(g3)
    c: DistanceY(g1,g1) = 6.4
    c: DistanceX(g0,g0) = 0.8
    c: DistanceY(g-1,g1) = 1.65
    c: DistanceX(g1,g-1) = 0.5
FEATURE [PartDesign::Pad] Pad064
  BaseFeature = -> Pad063
  Direction = (0,-1,2e-16)
  Length = 3
  Length2 = 10
  Profile = -> Sketch064
  ReferenceAxis = -> Sketch064 [N_Axis]
  Type = 0
FEATURE [Sketcher::SketchObject] Sketch065
  FullyConstrained = true
  MapMode = 5
  Placement = pos=(-1.3,0,0) rot=(0.57735,-0.57735,-0.57735;2.0944rad)
  Support = -> [Pad064]
  sketch-geometry (4):
    g0: LineSegment StartX=10.2 StartY=8.05 StartZ=0 EndX=11 EndY=8.05 EndZ=0
    g1: LineSegment StartX=11 StartY=8.05 StartZ=0 EndX=11 EndY=1.65 EndZ=0
    g2: LineSegment StartX=11 StartY=1.65 StartZ=0 EndX=10.2 EndY=1.65 EndZ=0
    g3: LineSegment StartX=10.2 StartY=1.65 StartZ=0 EndX=10.2 EndY=8.05 EndZ=0
  constraints (12):
    c: Coincident(g0,g1)
    c: Coincident(g1,g2)
    c: Coincident(g2,g3)
    c: Coincident(g3,g0)
    c: Horizontal(g0)
    c: Horizontal(g2)
    c: Vertical(g1)
    c: Vertical(g3)
    c: DistanceX(g0,g0) = 0.8
    c: DistanceY(g1,g1) = 6.4
    c: DistanceY(g-1,g2) = 1.65
    c: DistanceX(g-1,g2) = 10.2
FEATURE [PartDesign::Pad] Pad065
  BaseFeature = -> Pad064
  Direction = (-1,0,0)
  Length = 9.3
  Length2 = 10
  Profile = -> Sketch065
  ReferenceAxis = -> Sketch065 [N_Axis]
  Type = 0
FEATURE [PartDesign::Fillet] Fillet009
  Base = -> Pad065 [Edge36,Edge40]
  BaseFeature = -> Pad065
  Radius = 1.2
  SupportTransform = false
  UseAllEdges = false
FEATURE [PartDesign::Body] Body013  label="switch009"
  Group = -> [Sketch061,Pad061,Sketch062,Pad062,Sketch063,Pad063,Sketch064,Pad064,Sketch065,Pad065,Fillet009]
  Origin = -> Origin013
  Placement = pos=(239.8,0,-97) rot=(0,1,0;1.5708rad)
  Tip = -> Fillet009
FEATURE [App::DocumentObjectGroup] Group  label="thumbCluster"
  Group = -> [Body008,Body009,Body010,Body011,Body012,Body013]
FEATURE [App::DocumentObjectGroup] Group001  label="keySwitches"
  Group = -> [Group,Array003,Array002,Array001,Array]
FEATURE [Sketcher::SketchObject] Sketch066
  FullyConstrained = true
  MapMode = 5
  Placement = pos=(0,0,0) rot=(0.57735,0.57735,0.57735;2.0944rad)
  Support = -> [YZ_Plane014]
  sketch-geometry (1):
    g0: Circle CenterX=4.83 CenterY=-10.89 CenterZ=0 NormalX=0 NormalY=0 NormalZ=1 AngleXU=0 Radius=1.15
  constraints (3):
    c: Diameter(g0) = 2.3
    c: DistanceX(g-1,g0) = 4.83
    c: DistanceY(g0,g-1) = 10.89
FEATURE [PartDesign::Pad] Pad066
  Direction = (1,-2e-16,3e-16)
  Length = 290
  Length2 = 10
  Placement = pos=(0,0,0) rot=(0.57735,0.57735,0.57735;2.0944rad)
  Profile = -> Sketch066
  ReferenceAxis = -> Sketch066 [N_Axis]
  Type = 0
FEATURE [PartDesign::Body] Body014  label="stick1"
  Group = -> [Sketch066,Pad066]
  Origin = -> Origin014
  Tip = -> Pad066
FEATURE [Sketcher::SketchObject] Sketch067
  FullyConstrained = true
  MapMode = 5
  Placement = pos=(0,0,0) rot=(0.57735,0.57735,0.57735;2.0944rad)
  Support = -> [YZ_Plane015]
  sketch-geometry (1):
    g0: Circle CenterX=4.83 CenterY=-10.89 CenterZ=0 NormalX=0 NormalY=0 NormalZ=1 AngleXU=0 Radius=1.15
  constraints (3):
    c: Diameter(g0) = 2.3
    c: DistanceX(g-1,g0) = 4.83
    c: DistanceY(g0,g-1) = 10.89
FEATURE [PartDesign::Pad] Pad067
  Direction = (1,-2e-16,3e-16)
  Length = 290
  Length2 = 10
  Placement = pos=(0,0,0) rot=(0.57735,0.57735,0.57735;2.0944rad)
  Profile = -> Sketch067
  ReferenceAxis = -> Sketch067 [N_Axis]
  Type = 0
FEATURE [PartDesign::Body] Body015  label="stick2"
  Group = -> [Sketch067,Pad067]
  Origin = -> Origin015
  Placement = pos=(23,0,-43.5) rot=(0,0,1;0rad)
  Tip = -> Pad067
FEATURE [Sketcher::SketchObject] Sketch068
  FullyConstrained = true
  MapMode = 5
  Placement = pos=(0,0,0) rot=(1,0,0;1.5708rad)
  Support = -> [XZ_Plane016]
  sketch-geometry (9):
    g0: LineSegment StartX=33 StartY=-83 StartZ=0 EndX=113 EndY=-83 EndZ=0
    g1: LineSegment StartX=113 StartY=-83 StartZ=0 EndX=113 EndY=-116 EndZ=0
    g2: LineSegment StartX=-3 StartY=60 StartZ=0 EndX=260 EndY=60 EndZ=0
    g3: LineSegment StartX=260 StartY=60 StartZ=0 EndX=330 EndY=-83 EndZ=0
    g4: LineSegment StartX=330 StartY=-83 StartZ=0 EndX=258 EndY=-83 EndZ=0
    g5: LineSegment StartX=258 StartY=-83 StartZ=0 EndX=258 EndY=-116 EndZ=0
    g6: LineSegment StartX=258 StartY=-116 StartZ=0 EndX=113 EndY=-116 EndZ=0
    g7: LineSegment StartX=33 StartY=-83 StartZ=0 EndX=-3 EndY=-9.45714 EndZ=0
    g8: LineSegment StartX=-3 StartY=-9.45714 StartZ=0 EndX=-3 EndY=60 EndZ=0
  constraints (27):
    c: Horizontal(g0)
    c: Coincident(g0,g1)
    c: Vertical(g1)
    c: Horizontal(g2)
    c: Coincident(g2,g3)
    c: Coincident(g3,g4)
    c: Horizontal(g4)
    c: Coincident(g4,g5)
    c: Vertical(g5)
    c: Coincident(g5,g6)
    c: Coincident(g6,g1)
    c: Horizontal(g6)
    c: Horizontal(g0,g4)
    c: DistanceX(g-1,g2) = 260
    c: DistanceX(g-1,g0) = 33
    c: DistanceY(g0,g-1) = 83
    c: DistanceX(g6,g6) = 145
    c: DistanceY(g1,g1) = 33
    c: DistanceY(g-1,g2) = 60
    c: DistanceX(g0,g0) = 80
    c: Coincident(g0,g7)
    c: Coincident(g7,g8)
    c: Coincident(g8,g2)
    c: Parallel(g7,g3)
    c: Vertical(g8)
    c: DistanceX(g4,g4) = 72
    c: DistanceX(g7,g-1) = 3
FEATURE [PartDesign::Pad] Pad068
  Direction = (0,-1,-2e-16)
  Length = 5.5
  Length2 = 10
  Placement = pos=(0,0,0) rot=(1,0,0;1.5708rad)
  Profile = -> Sketch068
  ReferenceAxis = -> Sketch068 [N_Axis]
  Reversed = true
  Type = 0
FEATURE [Sketcher::SketchObject] Sketch069
  FullyConstrained = true
  MapMode = 5
  Placement = pos=(0,0,0) rot=(0.57735,0.57735,0.57735;2.0944rad)
  Support = -> [YZ_Plane017]
  sketch-geometry (1):
    g0: Circle CenterX=4.83 CenterY=-10.89 CenterZ=0 NormalX=0 NormalY=0 NormalZ=1 AngleXU=0 Radius=1.15
  constraints (3):
    c: Diameter(g0) = 2.3
    c: DistanceX(g-1,g0) = 4.83
    c: DistanceY(g0,g-1) = 10.89
FEATURE [PartDesign::Pad] Pad069
  Direction = (1,-2e-16,3e-16)
  Length = 138
  Length2 = 10
  Placement = pos=(0,0,0) rot=(0.57735,0.57735,0.57735;2.0944rad)
  Profile = -> Sketch069
  ReferenceAxis = -> Sketch069 [N_Axis]
  Type = 0
FEATURE [PartDesign::Body] Body017  label="stick003"
  Group = -> [Sketch069,Pad069]
  Origin = -> Origin017
  Placement = pos=(117,0,-75.2) rot=(0,0,1;0rad)
  Tip = -> Pad069
FEATURE [Sketcher::SketchObject] Sketch085
  FullyConstrained = true
  MapMode = 5
  Support = -> [XY_Plane021]
  sketch-geometry (10):
    g0: ArcOfCircle CenterX=-13.25 CenterY=18.25 CenterZ=0 NormalX=0 NormalY=0 NormalZ=1 AngleXU=0 Radius=1.75 StartAngle=1.5708 EndAngle=3.14159
    g1: LineSegment StartX=-13.25 StartY=20 StartZ=0 EndX=13.25 EndY=20 EndZ=0
    g2: ArcOfCircle CenterX=13.25 CenterY=18.25 CenterZ=0 NormalX=0 NormalY=0 NormalZ=1 AngleXU=0 Radius=1.75 StartAngle=-1.8e-15 EndAngle=1.5708
    g3: LineSegment StartX=15 StartY=18.25 StartZ=0 EndX=15 EndY=-18.25 EndZ=0
    g4: ArcOfCircle CenterX=13.25 CenterY=-18.25 CenterZ=0 NormalX=0 NormalY=0 NormalZ=1 AngleXU=0 Radius=1.75 StartAngle=4.71239 EndAngle=6.28319
    g5: LineSegment StartX=13.25 StartY=-20 StartZ=0 EndX=-13.25 EndY=-20 EndZ=0
    g6: ArcOfCircle CenterX=-13.25 CenterY=-18.25 CenterZ=0 NormalX=0 NormalY=0 NormalZ=1 AngleXU=0 Radius=1.75 StartAngle=3.14159 EndAngle=4.71239
    g7: LineSegment StartX=-15 StartY=-18.25 StartZ=0 EndX=-15 EndY=18.25 EndZ=0
    g8: GeomPoint X=-15 Y=20 Z=0
    g9: GeomPoint X=15 Y=-20 Z=0
  constraints (23):
    c: Tangent(g0,g1) = 1.5708
    c: Tangent(g1,g2) = 1.5708
    c: Tangent(g2,g3) = 1.5708
    c: Tangent(g3,g4) = 1.5708
    c: Tangent(g4,g5) = 1.5708
    c: Tangent(g5,g6) = 1.5708
    c: Tangent(g6,g7) = 1.5708
    c: Tangent(g7,g0) = 1.5708
    c: Horizontal(g1)
    c: Horizontal(g5)
    c: Vertical(g3)
    c: Vertical(g7)
    c: Equal(g0,g2)
    c: Equal(g2,g4)
    c: Equal(g4,g6)
    c: PointOnObject(g8,g1)
    c: PointOnObject(g8,g7)
    c: PointOnObject(g9,g3)
    c: PointOnObject(g9,g5)
    c: DistanceX(g0,g2) = 30
    c: DistanceY(g5,g0) = 40
    c: Symmetric(g6,g2,g-1)
    c: Diameter(g0) = 3.5
FEATURE [PartDesign::Pad] Pad085
  Direction = (0,0,1)
  Length = 10.7
  Length2 = 10
  Profile = -> Sketch085
  ReferenceAxis = -> Sketch085 [N_Axis]
  Type = 0
FEATURE [PartDesign::Body] Body021  label="switch013"
  Group = -> [Sketch085,Pad085]
  Origin = -> Origin021
  Placement = pos=(0,0,0) rot=(0,1,0;1.5708rad)
  Tip = -> Pad085
FEATURE [Part::FeaturePython] Array007  # Draft array (typed FeaturePython)
  AlwaysSyncPlacement = false
  Angle = 360
  ArrayType = 0
  Axis = (0,0,1)
  Base = -> Body021
  Center = (0,0,0)
  Count = 12
  ExpandArray = false
  Fuse = false
  IntervalAxis = (0,0,0)
  IntervalX = (23.5,0,0)
  IntervalY = (0,100,0)
  IntervalZ = (0,0,40)
  NumberCircles = 3
  NumberPolar = 5
  NumberX = 12
  NumberY = 1
  NumberZ = 1
  Placement = pos=(39.55,0,-65.28) rot=(0,1,0;0rad)
  PlacementList = 12 placements: arithmetic series from (0,0,0) step (23.5,0,0) to (258.5,0,0)
  RadialDistance = 50
  ScaleList = (12) [(1,1,1),(1,1,1),(1,1,1),(1,1,1),(1,1,1),(1,1,1),(1,1,1),(1,1,1),(1,1,1),(1,1,1),(1,1,1),(1,1,1)]
  Symmetry = 1
  TangentialDistance = 25
FEATURE [Sketcher::SketchObject] Sketch120
  FullyConstrained = true
  MapMode = 5
  Support = -> [XY_Plane028]
  sketch-geometry (10):
    g0: ArcOfCircle CenterX=-13.25 CenterY=18.25 CenterZ=0 NormalX=0 NormalY=0 NormalZ=1 AngleXU=0 Radius=1.75 StartAngle=1.5708 EndAngle=3.14159
    g1: LineSegment StartX=-13.25 StartY=20 StartZ=0 EndX=13.25 EndY=20 EndZ=0
    g2: ArcOfCircle CenterX=13.25 CenterY=18.25 CenterZ=0 NormalX=0 NormalY=0 NormalZ=1 AngleXU=0 Radius=1.75 StartAngle=-1.8e-15 EndAngle=1.5708
    g3: LineSegment StartX=15 StartY=18.25 StartZ=0 EndX=15 EndY=-18.25 EndZ=0
    g4: ArcOfCircle CenterX=13.25 CenterY=-18.25 CenterZ=0 NormalX=0 NormalY=0 NormalZ=1 AngleXU=0 Radius=1.75 StartAngle=4.71239 EndAngle=6.28319
    g5: LineSegment StartX=13.25 StartY=-20 StartZ=0 EndX=-13.25 EndY=-20 EndZ=0
    g6: ArcOfCircle CenterX=-13.25 CenterY=-18.25 CenterZ=0 NormalX=0 NormalY=0 NormalZ=1 AngleXU=0 Radius=1.75 StartAngle=3.14159 EndAngle=4.71239
    g7: LineSegment StartX=-15 StartY=-18.25 StartZ=0 EndX=-15 EndY=18.25 EndZ=0
    g8: GeomPoint X=-15 Y=20 Z=0
    g9: GeomPoint X=15 Y=-20 Z=0
  constraints (23):
    c: Tangent(g0,g1) = 1.5708
    c: Tangent(g1,g2) = 1.5708
    c: Tangent(g2,g3) = 1.5708
    c: Tangent(g3,g4) = 1.5708
    c: Tangent(g4,g5) = 1.5708
    c: Tangent(g5,g6) = 1.5708
    c: Tangent(g6,g7) = 1.5708
    c: Tangent(g7,g0) = 1.5708
    c: Horizontal(g1)
    c: Horizontal(g5)
    c: Vertical(g3)
    c: Vertical(g7)
    c: Equal(g0,g2)
    c: Equal(g2,g4)
    c: Equal(g4,g6)
    c: PointOnObject(g8,g1)
    c: PointOnObject(g8,g7)
    c: PointOnObject(g9,g3)
    c: PointOnObject(g9,g5)
    c: DistanceX(g0,g2) = 30
    c: DistanceY(g5,g0) = 40
    c: Symmetric(g6,g2,g-1)
    c: Diameter(g0) = 3.5
FEATURE [PartDesign::Pad] Pad120
  Direction = (0,0,1)
  Length = 10.7
  Length2 = 10
  Profile = -> Sketch120
  ReferenceAxis = -> Sketch120 [N_Axis]
  Type = 0
FEATURE [PartDesign::Body] Body028  label="switch020"
  Group = -> [Sketch120,Pad120]
  Origin = -> Origin028
  Placement = pos=(0,0,0) rot=(0,1,0;1.5708rad)
  Tip = -> Pad120
FEATURE [Part::FeaturePython] Array006  # Draft array (typed FeaturePython)
  AlwaysSyncPlacement = false
  Angle = 360
  ArrayType = 0
  Axis = (0,0,1)
  Base = -> Body028
  Center = (0,0,0)
  Count = 12
  ExpandArray = false
  Fuse = false
  IntervalAxis = (0,0,0)
  IntervalX = (23.5,0,0)
  IntervalY = (0,100,0)
  IntervalZ = (0,0,40)
  NumberCircles = 3
  NumberPolar = 5
  NumberX = 12
  NumberY = 1
  NumberZ = 1
  Placement = pos=(297,0,-43.52) rot=(0,1,0;3.14159rad)
  PlacementList = 12 placements: arithmetic series from (0,0,0) step (23.5,0,0) to (258.5,0,0)
  RadialDistance = 50
  ScaleList = (12) [(1,1,1),(1,1,1),(1,1,1),(1,1,1),(1,1,1),(1,1,1),(1,1,1),(1,1,1),(1,1,1),(1,1,1),(1,1,1),(1,1,1)]
  Symmetry = 1
  TangentialDistance = 25
FEATURE [Sketcher::SketchObject] Sketch121
  FullyConstrained = true
  MapMode = 5
  Support = -> [XY_Plane029]
  sketch-geometry (10):
    g0: ArcOfCircle CenterX=-13.25 CenterY=18.25 CenterZ=0 NormalX=0 NormalY=0 NormalZ=1 AngleXU=0 Radius=1.75 StartAngle=1.5708 EndAngle=3.14159
    g1: LineSegment StartX=-13.25 StartY=20 StartZ=0 EndX=13.25 EndY=20 EndZ=0
    g2: ArcOfCircle CenterX=13.25 CenterY=18.25 CenterZ=0 NormalX=0 NormalY=0 NormalZ=1 AngleXU=0 Radius=1.75 StartAngle=-1.8e-15 EndAngle=1.5708
    g3: LineSegment StartX=15 StartY=18.25 StartZ=0 EndX=15 EndY=-18.25 EndZ=0
    g4: ArcOfCircle CenterX=13.25 CenterY=-18.25 CenterZ=0 NormalX=0 NormalY=0 NormalZ=1 AngleXU=0 Radius=1.75 StartAngle=4.71239 EndAngle=6.28319
    g5: LineSegment StartX=13.25 StartY=-20 StartZ=0 EndX=-13.25 EndY=-20 EndZ=0
    g6: ArcOfCircle CenterX=-13.25 CenterY=-18.25 CenterZ=0 NormalX=0 NormalY=0 NormalZ=1 AngleXU=0 Radius=1.75 StartAngle=3.14159 EndAngle=4.71239
    g7: LineSegment StartX=-15 StartY=-18.25 StartZ=0 EndX=-15 EndY=18.25 EndZ=0
    g8: GeomPoint X=-15 Y=20 Z=0
    g9: GeomPoint X=15 Y=-20 Z=0
  constraints (23):
    c: Tangent(g0,g1) = 1.5708
    c: Tangent(g1,g2) = 1.5708
    c: Tangent(g2,g3) = 1.5708
    c: Tangent(g3,g4) = 1.5708
    c: Tangent(g4,g5) = 1.5708
    c: Tangent(g5,g6) = 1.5708
    c: Tangent(g6,g7) = 1.5708
    c: Tangent(g7,g0) = 1.5708
    c: Horizontal(g1)
    c: Horizontal(g5)
    c: Vertical(g3)
    c: Vertical(g7)
    c: Equal(g0,g2)
    c: Equal(g2,g4)
    c: Equal(g4,g6)
    c: PointOnObject(g8,g1)
    c: PointOnObject(g8,g7)
    c: PointOnObject(g9,g3)
    c: PointOnObject(g9,g5)
    c: DistanceX(g0,g2) = 30
    c: DistanceY(g5,g0) = 40
    c: Symmetric(g6,g2,g-1)
    c: Diameter(g0) = 3.5
FEATURE [PartDesign::Pad] Pad121
  Direction = (0,0,1)
  Length = 10.7
  Length2 = 10
  Profile = -> Sketch121
  ReferenceAxis = -> Sketch121 [N_Axis]
  Type = 0
FEATURE [PartDesign::Body] Body029  label="switch021"
  Group = -> [Sketch121,Pad121]
  Origin = -> Origin029
  Placement = pos=(0,0,0) rot=(0,1,0;1.5708rad)
  Tip = -> Pad121
FEATURE [Part::FeaturePython] Array005  # Draft array (typed FeaturePython)
  AlwaysSyncPlacement = false
  Angle = 360
  ArrayType = 0
  Axis = (0,0,1)
  Base = -> Body029
  Center = (0,0,0)
  Count = 12
  ExpandArray = false
  Fuse = false
  IntervalAxis = (0,0,0)
  IntervalX = (23.5,0,0)
  IntervalY = (0,100,0)
  IntervalZ = (0,0,40)
  NumberCircles = 3
  NumberPolar = 5
  NumberX = 12
  NumberY = 1
  NumberZ = 1
  Placement = pos=(16.05,0,-21.76) rot=(0,1,0;0rad)
  PlacementList = 12 placements: arithmetic series from (0,0,0) step (23.5,0,0) to (258.5,0,0)
  RadialDistance = 50
  ScaleList = (12) [(1,1,1),(1,1,1),(1,1,1),(1,1,1),(1,1,1),(1,1,1),(1,1,1),(1,1,1),(1,1,1),(1,1,1),(1,1,1),(1,1,1)]
  Symmetry = 1
  TangentialDistance = 25
FEATURE [Sketcher::SketchObject] Sketch122
  FullyConstrained = true
  MapMode = 5
  Support = -> [XY_Plane030]
  sketch-geometry (10):
    g0: ArcOfCircle CenterX=-13.25 CenterY=18.25 CenterZ=0 NormalX=0 NormalY=0 NormalZ=1 AngleXU=0 Radius=1.75 StartAngle=1.5708 EndAngle=3.14159
    g1: LineSegment StartX=-13.25 StartY=20 StartZ=0 EndX=13.25 EndY=20 EndZ=0
    g2: ArcOfCircle CenterX=13.25 CenterY=18.25 CenterZ=0 NormalX=0 NormalY=0 NormalZ=1 AngleXU=0 Radius=1.75 StartAngle=-1.8e-15 EndAngle=1.5708
    g3: LineSegment StartX=15 StartY=18.25 StartZ=0 EndX=15 EndY=-18.25 EndZ=0
    g4: ArcOfCircle CenterX=13.25 CenterY=-18.25 CenterZ=0 NormalX=0 NormalY=0 NormalZ=1 AngleXU=0 Radius=1.75 StartAngle=4.71239 EndAngle=6.28319
    g5: LineSegment StartX=13.25 StartY=-20 StartZ=0 EndX=-13.25 EndY=-20 EndZ=0
    g6: ArcOfCircle CenterX=-13.25 CenterY=-18.25 CenterZ=0 NormalX=0 NormalY=0 NormalZ=1 AngleXU=0 Radius=1.75 StartAngle=3.14159 EndAngle=4.71239
    g7: LineSegment StartX=-15 StartY=-18.25 StartZ=0 EndX=-15 EndY=18.25 EndZ=0
    g8: GeomPoint X=-15 Y=20 Z=0
    g9: GeomPoint X=15 Y=-20 Z=0
  constraints (23):
    c: Tangent(g0,g1) = 1.5708
    c: Tangent(g1,g2) = 1.5708
    c: Tangent(g2,g3) = 1.5708
    c: Tangent(g3,g4) = 1.5708
    c: Tangent(g4,g5) = 1.5708
    c: Tangent(g5,g6) = 1.5708
    c: Tangent(g6,g7) = 1.5708
    c: Tangent(g7,g0) = 1.5708
    c: Horizontal(g1)
    c: Horizontal(g5)
    c: Vertical(g3)
    c: Vertical(g7)
    c: Equal(g0,g2)
    c: Equal(g2,g4)
    c: Equal(g4,g6)
    c: PointOnObject(g8,g1)
    c: PointOnObject(g8,g7)
    c: PointOnObject(g9,g3)
    c: PointOnObject(g9,g5)
    c: DistanceX(g0,g2) = 30
    c: DistanceY(g5,g0) = 40
    c: Symmetric(g6,g2,g-1)
    c: Diameter(g0) = 3.5
FEATURE [PartDesign::Pad] Pad122
  Direction = (0,0,1)
  Length = 10.7
  Length2 = 10
  Profile = -> Sketch122
  ReferenceAxis = -> Sketch122 [N_Axis]
  Type = 0
FEATURE [PartDesign::Body] Body030  label="switch022"
  Group = -> [Sketch122,Pad122]
  Origin = -> Origin030
  Placement = pos=(0,0,0) rot=(0,1,0;1.5708rad)
  Tip = -> Pad122
FEATURE [Part::FeaturePython] Array004  # Draft array (typed FeaturePython)
  AlwaysSyncPlacement = false
  Angle = 360
  ArrayType = 0
  Axis = (0,0,1)
  Base = -> Body030
  Center = (0,0,0)
  Count = 12
  ExpandArray = false
  Fuse = false
  IntervalAxis = (0,0,0)
  IntervalX = (23.5,0,0)
  IntervalY = (0,100,0)
  IntervalZ = (0,0,40)
  NumberCircles = 3
  NumberPolar = 5
  NumberX = 12
  NumberY = 1
  NumberZ = 1
  Placement = pos=(273.5,0,0) rot=(0,1,0;3.14159rad)
  PlacementList = 12 placements: arithmetic series from (0,0,0) step (23.5,0,0) to (258.5,0,0)
  RadialDistance = 50
  ScaleList = (12) [(1,1,1),(1,1,1),(1,1,1),(1,1,1),(1,1,1),(1,1,1),(1,1,1),(1,1,1),(1,1,1),(1,1,1),(1,1,1),(1,1,1)]
  Symmetry = 1
  TangentialDistance = 25
FEATURE [Sketcher::SketchObject] Sketch128
  FullyConstrained = true
  MapMode = 5
  Support = -> [XY_Plane036]
  sketch-geometry (10):
    g0: ArcOfCircle CenterX=-13.25 CenterY=18.25 CenterZ=0 NormalX=0 NormalY=0 NormalZ=1 AngleXU=0 Radius=1.75 StartAngle=1.5708 EndAngle=3.14159
    g1: LineSegment StartX=-13.25 StartY=20 StartZ=0 EndX=13.25 EndY=20 EndZ=0
    g2: ArcOfCircle CenterX=13.25 CenterY=18.25 CenterZ=0 NormalX=0 NormalY=0 NormalZ=1 AngleXU=0 Radius=1.75 StartAngle=-1.8e-15 EndAngle=1.5708
    g3: LineSegment StartX=15 StartY=18.25 StartZ=0 EndX=15 EndY=-18.25 EndZ=0
    g4: ArcOfCircle CenterX=13.25 CenterY=-18.25 CenterZ=0 NormalX=0 NormalY=0 NormalZ=1 AngleXU=0 Radius=1.75 StartAngle=4.71239 EndAngle=6.28319
    g5: LineSegment StartX=13.25 StartY=-20 StartZ=0 EndX=-13.25 EndY=-20 EndZ=0
    g6: ArcOfCircle CenterX=-13.25 CenterY=-18.25 CenterZ=0 NormalX=0 NormalY=0 NormalZ=1 AngleXU=0 Radius=1.75 StartAngle=3.14159 EndAngle=4.71239
    g7: LineSegment StartX=-15 StartY=-18.25 StartZ=0 EndX=-15 EndY=18.25 EndZ=0
    g8: GeomPoint X=-15 Y=20 Z=0
    g9: GeomPoint X=15 Y=-20 Z=0
  constraints (23):
    c: Tangent(g0,g1) = 1.5708
    c: Tangent(g1,g2) = 1.5708
    c: Tangent(g2,g3) = 1.5708
    c: Tangent(g3,g4) = 1.5708
    c: Tangent(g4,g5) = 1.5708
    c: Tangent(g5,g6) = 1.5708
    c: Tangent(g6,g7) = 1.5708
    c: Tangent(g7,g0) = 1.5708
    c: Horizontal(g1)
    c: Horizontal(g5)
    c: Vertical(g3)
    c: Vertical(g7)
    c: Equal(g0,g2)
    c: Equal(g2,g4)
    c: Equal(g4,g6)
    c: PointOnObject(g8,g1)
    c: PointOnObject(g8,g7)
    c: PointOnObject(g9,g3)
    c: PointOnObject(g9,g5)
    c: DistanceX(g0,g2) = 30
    c: DistanceY(g5,g0) = 40
    c: Symmetric(g6,g2,g-1)
    c: Diameter(g0) = 3.5
FEATURE [PartDesign::Pad] Pad128
  Direction = (0,0,1)
  Length = 10.7
  Length2 = 10
  Profile = -> Sketch128
  ReferenceAxis = -> Sketch128 [N_Axis]
  Type = 0
FEATURE [PartDesign::Body] Body036  label="switch028"
  Group = -> [Sketch128,Pad128]
  Origin = -> Origin036
  Placement = pos=(110.4,0,-105) rot=(0,1,0;1.5708rad)
  Tip = -> Pad128
FEATURE [Part::FeaturePython] Array008  label="thumbCluster001"  # Draft array (typed FeaturePython)
  AlwaysSyncPlacement = false
  Angle = 360
  ArrayType = 0
  Axis = (0,0,1)
  Base = -> Body036
  Center = (0,0,0)
  Count = 6
  ExpandArray = false
  Fuse = false
  IntervalAxis = (0,0,0)
  IntervalX = (23.5,0,0)
  IntervalY = (0,100,0)
  IntervalZ = (0,0,100)
  NumberCircles = 3
  NumberPolar = 5
  NumberX = 6
  NumberY = 1
  NumberZ = 1
  Placement = pos=(11.4,0,8) rot=(0,0,1;0rad)
  PlacementList = 6 placements: arithmetic series from (110.4,0,-105) step (23.5,0,0) to (227.9,0,-105)
  RadialDistance = 50
  ScaleList = (6) [(1,1,1),(1,1,1),(1,1,1),(1,1,1),(1,1,1),(1,1,1)]
  Symmetry = 1
  TangentialDistance = 25
FEATURE [App::DocumentObjectGroup] Group002  label="thumbCluster002"
FEATURE [Sketcher::SketchObject] Sketch188
  FullyConstrained = true
  MapMode = 5
  Placement = pos=(0,0,0) rot=(1,0,0;1.5708rad)
  Support = -> [XZ_Plane051]
  sketch-geometry (13):
    g0: Circle CenterX=0 CenterY=0 CenterZ=0 NormalX=0 NormalY=0 NormalZ=1 AngleXU=0 Radius=2.9
    g1: LineSegment StartX=-0.5 StartY=1.75 StartZ=0 EndX=-0.5 EndY=0.5 EndZ=0
    g2: LineSegment StartX=-0.5 StartY=0.5 StartZ=0 EndX=-1.75 EndY=0.5 EndZ=0
    g3: LineSegment StartX=-1.75 StartY=0.5 StartZ=0 EndX=-1.75 EndY=-0.5 EndZ=0
    g4: LineSegment StartX=-1.75 StartY=-0.5 StartZ=0 EndX=-0.5 EndY=-0.5 EndZ=0
    g5: LineSegment StartX=-0.5 StartY=-0.5 StartZ=0 EndX=-0.5 EndY=-1.75 EndZ=0
    g6: LineSegment StartX=-0.5 StartY=-1.75 StartZ=0 EndX=0.5 EndY=-1.75 EndZ=0
    g7: LineSegment StartX=0.5 StartY=-1.75 StartZ=0 EndX=0.5 EndY=-0.5 EndZ=0
    g8: LineSegment StartX=0.5 StartY=-0.5 StartZ=0 EndX=1.75 EndY=-0.5 EndZ=0
    g9: LineSegment StartX=1.75 StartY=-0.5 StartZ=0 EndX=1.75 EndY=0.5 EndZ=0
    g10: LineSegment StartX=1.75 StartY=0.5 StartZ=0 EndX=0.5 EndY=0.5 EndZ=0
    g11: LineSegment StartX=0.5 StartY=0.5 StartZ=0 EndX=0.5 EndY=1.75 EndZ=0
    g12: LineSegment StartX=0.5 StartY=1.75 StartZ=0 EndX=-0.5 EndY=1.75 EndZ=0
  constraints (37):
    c: Coincident(g0,g-1)
    c: Diameter(g0) = 5.8
    c: Coincident(g1,g2)
    c: Coincident(g2,g3)
    c: Vertical(g3)
    c: Coincident(g3,g4)
    c: Horizontal(g4)
    c: Coincident(g4,g5)
    c: Vertical(g5)
    c: Coincident(g5,g6)
    c: Horizontal(g6)
    c: Coincident(g6,g7)
    c: Coincident(g7,g8)
    c: Horizontal(g8)
    c: Coincident(g8,g9)
    c: Vertical(g9)
    c: Coincident(g9,g10)
    c: Coincident(g10,g11)
    c: Coincident(g11,g12)
    c: Coincident(g12,g1)
    c: Horizontal(g12)
    c: Horizontal(g10)
    c: Horizontal(g2)
    c: Vertical(g11)
    c: Vertical(g1)
    c: Vertical(g7)
    c: Vertical(g1,g4)
    c: Vertical(g10,g7)
    c: Horizontal(g1,g10)
    c: Horizontal(g4,g7)
    c: Symmetric(g4,g10,g0)
    c: DistanceY(g6,g11) = 3.5
    c: DistanceY(g9,g9) = 1
    c: Equal(g11,g10)
    c: Equal(g7,g8)
    c: Equal(g2,g1)
    c: Equal(g12,g3)
FEATURE [PartDesign::Pad] Pad184
  Direction = (0,-1,2e-16)
  Length = 8
  Length2 = 10
  Placement = pos=(0,0,0) rot=(1,0,0;1.5708rad)
  Profile = -> Sketch188
  ReferenceAxis = -> Sketch188 [N_Axis]
  Type = 0
FEATURE [Sketcher::SketchObject] Sketch189
  FullyConstrained = true
  MapMode = 5
  Placement = pos=(0,-8,3.5e-15) rot=(1,0,0;1.5708rad)
  Support = -> [Pad184]
  sketch-geometry (10):
    g0: ArcOfCircle CenterX=-7.15 CenterY=7.15 CenterZ=0 NormalX=0 NormalY=0 NormalZ=1 AngleXU=0 Radius=2 StartAngle=1.5708 EndAngle=3.14159
    g1: LineSegment StartX=-7.15 StartY=9.15 StartZ=0 EndX=7.15 EndY=9.15 EndZ=0
    g2: ArcOfCircle CenterX=7.15 CenterY=7.15 CenterZ=0 NormalX=0 NormalY=0 NormalZ=1 AngleXU=0 Radius=2 StartAngle=3e-16 EndAngle=1.5708
    g3: LineSegment StartX=9.15 StartY=7.15 StartZ=0 EndX=9.15 EndY=-7.15 EndZ=0
    g4: ArcOfCircle CenterX=7.15 CenterY=-7.15 CenterZ=0 NormalX=0 NormalY=0 NormalZ=1 AngleXU=0 Radius=2 StartAngle=4.71239 EndAngle=6.28319
    g5: LineSegment StartX=7.15 StartY=-9.15 StartZ=0 EndX=-7.15 EndY=-9.15 EndZ=0
    g6: ArcOfCircle CenterX=-7.15 CenterY=-7.15 CenterZ=0 NormalX=0 NormalY=0 NormalZ=1 AngleXU=0 Radius=2 StartAngle=3.14159 EndAngle=4.71239
    g7: LineSegment StartX=-9.15 StartY=-7.15 StartZ=0 EndX=-9.15 EndY=7.15 EndZ=0
    g8: GeomPoint X=-9.15 Y=9.15 Z=0
    g9: GeomPoint X=9.15 Y=-9.15 Z=0
  constraints (23):
    c: Tangent(g0,g1) = 1.5708
    c: Tangent(g1,g2) = 1.5708
    c: Tangent(g2,g3) = 1.5708
    c: Tangent(g3,g4) = 1.5708
    c: Tangent(g4,g5) = 1.5708
    c: Tangent(g5,g6) = 1.5708
    c: Tangent(g6,g7) = 1.5708
    c: Tangent(g7,g0) = 1.5708
    c: Horizontal(g1)
    c: Horizontal(g5)
    c: Vertical(g3)
    c: Vertical(g7)
    c: Equal(g0,g2)
    c: Equal(g2,g4)
    c: Equal(g4,g6)
    c: PointOnObject(g8,g1)
    c: PointOnObject(g8,g7)
    c: PointOnObject(g9,g3)
    c: PointOnObject(g9,g5)
    c: Symmetric(g6,g2,g-1)
    c: DistanceY(g5,g0) = 18.3
    c: DistanceX(g0,g2) = 18.3
    c: Diameter(g0) = 4
FEATURE [PartDesign::Pad] Pad185
  BaseFeature = -> Pad184
  Direction = (0,-1,2e-16)
  Length = 1.2
  Length2 = 10
  Placement = pos=(0,0,0) rot=(1,0,0;1.5708rad)
  Profile = -> Sketch189
  ReferenceAxis = -> Sketch189 [N_Axis]
  Type = 0
FEATURE [Sketcher::SketchObject] Sketch190
  FullyConstrained = true
  MapMode = 5
  Placement = pos=(0,-8,3.5e-15) rot=(-1,0,0;1.5708rad)
  Support = -> [Pad185]
  sketch-geometry (20):
    g0: ArcOfCircle CenterX=-7.15 CenterY=7.15 CenterZ=0 NormalX=0 NormalY=0 NormalZ=1 AngleXU=0 Radius=2 StartAngle=1.5708 EndAngle=3.14159
    g1: LineSegment StartX=-7.15 StartY=9.15 StartZ=0 EndX=7.15 EndY=9.15 EndZ=0
    g2: ArcOfCircle CenterX=7.15 CenterY=7.15 CenterZ=0 NormalX=0 NormalY=0 NormalZ=1 AngleXU=0 Radius=2 StartAngle=2e-16 EndAngle=1.5708
    g3: LineSegment StartX=9.15 StartY=7.15 StartZ=0 EndX=9.15 EndY=-7.15 EndZ=0
    g4: ArcOfCircle CenterX=7.15 CenterY=-7.15 CenterZ=0 NormalX=0 NormalY=0 NormalZ=1 AngleXU=0 Radius=2 StartAngle=4.71239 EndAngle=6.28319
    g5: LineSegment StartX=7.15 StartY=-9.15 StartZ=0 EndX=-7.15 EndY=-9.15 EndZ=0
    g6: ArcOfCircle CenterX=-7.15 CenterY=-7.15 CenterZ=0 NormalX=0 NormalY=0 NormalZ=1 AngleXU=0 Radius=2 StartAngle=3.14159 EndAngle=4.71239
    g7: LineSegment StartX=-9.15 StartY=-7.15 StartZ=0 EndX=-9.15 EndY=7.15 EndZ=0
    g8: GeomPoint X=-9.15 Y=9.15 Z=0
    g9: GeomPoint X=9.15 Y=-9.15 Z=0
    g10: ArcOfCircle CenterX=-6.4 CenterY=6.4 CenterZ=0 NormalX=0 NormalY=0 NormalZ=1 AngleXU=0 Radius=1.25 StartAngle=1.5708 EndAngle=3.14159
    g11: LineSegment StartX=-6.4 StartY=7.65 StartZ=0 EndX=6.4 EndY=7.65 EndZ=0
    g12: ArcOfCircle CenterX=6.4 CenterY=6.4 CenterZ=0 NormalX=0 NormalY=0 NormalZ=1 AngleXU=0 Radius=1.25 StartAngle=2e-16 EndAngle=1.5708
    g13: LineSegment StartX=7.65 StartY=6.4 StartZ=0 EndX=7.65 EndY=-6.4 EndZ=0
    g14: ArcOfCircle CenterX=6.4 CenterY=-6.4 CenterZ=0 NormalX=0 NormalY=0 NormalZ=1 AngleXU=0 Radius=1.25 StartAngle=4.71239 EndAngle=6.28319
    g15: LineSegment StartX=6.4 StartY=-7.65 StartZ=0 EndX=-6.4 EndY=-7.65 EndZ=0
    g16: ArcOfCircle CenterX=-6.4 CenterY=-6.4 CenterZ=0 NormalX=0 NormalY=0 NormalZ=1 AngleXU=0 Radius=1.25 StartAngle=3.14159 EndAngle=4.71239
    g17: LineSegment StartX=-7.65 StartY=-6.4 StartZ=0 EndX=-7.65 EndY=6.4 EndZ=0
    g18: GeomPoint X=-7.65 Y=7.65 Z=0
    g19: GeomPoint X=7.65 Y=-7.65 Z=0
  constraints (46):
    c: Tangent(g0,g1) = 1.5708
    c: Tangent(g1,g2) = 1.5708
    c: Tangent(g2,g3) = 1.5708
    c: Tangent(g3,g4) = 1.5708
    c: Tangent(g4,g5) = 1.5708
    c: Tangent(g5,g6) = 1.5708
    c: Tangent(g6,g7) = 1.5708
    c: Tangent(g7,g0) = 1.5708
    c: Horizontal(g1)
    c: Horizontal(g5)
    c: Vertical(g3)
    c: Vertical(g7)
    c: Equal(g0,g2)
    c: Equal(g2,g4)
    c: Equal(g4,g6)
    c: PointOnObject(g8,g1)
    c: PointOnObject(g8,g7)
    c: PointOnObject(g9,g3)
    c: PointOnObject(g9,g5)
    c: DistanceY(g4,g1) = 18.3
    c: DistanceX(g0,g2) = 18.3
    c: Symmetric(g6,g2,g-1)
    c: Diameter(g0) = 4
    c: Tangent(g10,g11) = 1.5708
    c: Tangent(g11,g12) = 1.5708
    c: Tangent(g12,g13) = 1.5708
    c: Tangent(g13,g14) = 1.5708
    c: Tangent(g14,g15) = 1.5708
    c: Tangent(g15,g16) = 1.5708
    c: Tangent(g16,g17) = 1.5708
    c: Tangent(g17,g10) = 1.5708
    c: Horizontal(g11)
    c: Horizontal(g15)
    c: Vertical(g13)
    c: Vertical(g17)
    c: Equal(g10,g12)
    c: Equal(g12,g14)
    c: Equal(g14,g16)
    c: PointOnObject(g18,g11)
    c: PointOnObject(g18,g17)
    c: PointOnObject(g19,g13)
    c: PointOnObject(g19,g15)
    c: Symmetric(g10,g14,g-1)
    c: Diameter(g10) = 2.5
    c: DistanceY(g10,g0) = 1.5
    c: Equal(g11,g13)
FEATURE [PartDesign::Pad] Pad186
  BaseFeature = -> Pad185
  Direction = (0,1,-2e-16)
  Length = 8
  Length2 = 10
  Placement = pos=(0,0,0) rot=(1,0,0;1.5708rad)
  Profile = -> Sketch190
  ReferenceAxis = -> Sketch190 [N_Axis]
  Type = 0
FEATURE [PartDesign::Body] Body051  label="standardKeyCap"
  Group = -> [Sketch188,Pad184,Sketch189,Pad185,Sketch190,Pad186]
  Origin = -> Origin051
  Placement = pos=(9.65,-9,5) rot=(0,0,1;0rad)
  Tip = -> Pad186
FEATURE [Sketcher::SketchObject] Sketch191
  FullyConstrained = true
  MapMode = 5
  Placement = pos=(0,0,0) rot=(1,0,0;1.5708rad)
  Support = -> [XZ_Plane052]
  sketch-geometry (13):
    g0: Circle CenterX=0 CenterY=0 CenterZ=0 NormalX=0 NormalY=0 NormalZ=1 AngleXU=0 Radius=2.9
    g1: LineSegment StartX=-0.5 StartY=1.75 StartZ=0 EndX=-0.5 EndY=0.5 EndZ=0
    g2: LineSegment StartX=-0.5 StartY=0.5 StartZ=0 EndX=-1.75 EndY=0.5 EndZ=0
    g3: LineSegment StartX=-1.75 StartY=0.5 StartZ=0 EndX=-1.75 EndY=-0.5 EndZ=0
    g4: LineSegment StartX=-1.75 StartY=-0.5 StartZ=0 EndX=-0.5 EndY=-0.5 EndZ=0
    g5: LineSegment StartX=-0.5 StartY=-0.5 StartZ=0 EndX=-0.5 EndY=-1.75 EndZ=0
    g6: LineSegment StartX=-0.5 StartY=-1.75 StartZ=0 EndX=0.5 EndY=-1.75 EndZ=0
    g7: LineSegment StartX=0.5 StartY=-1.75 StartZ=0 EndX=0.5 EndY=-0.5 EndZ=0
    g8: LineSegment StartX=0.5 StartY=-0.5 StartZ=0 EndX=1.75 EndY=-0.5 EndZ=0
    g9: LineSegment StartX=1.75 StartY=-0.5 StartZ=0 EndX=1.75 EndY=0.5 EndZ=0
    g10: LineSegment StartX=1.75 StartY=0.5 StartZ=0 EndX=0.5 EndY=0.5 EndZ=0
    g11: LineSegment StartX=0.5 StartY=0.5 StartZ=0 EndX=0.5 EndY=1.75 EndZ=0
    g12: LineSegment StartX=0.5 StartY=1.75 StartZ=0 EndX=-0.5 EndY=1.75 EndZ=0
  constraints (37):
    c: Coincident(g0,g-1)
    c: Diameter(g0) = 5.8
    c: Coincident(g1,g2)
    c: Coincident(g2,g3)
    c: Vertical(g3)
    c: Coincident(g3,g4)
    c: Horizontal(g4)
    c: Coincident(g4,g5)
    c: Vertical(g5)
    c: Coincident(g5,g6)
    c: Horizontal(g6)
    c: Coincident(g6,g7)
    c: Coincident(g7,g8)
    c: Horizontal(g8)
    c: Coincident(g8,g9)
    c: Vertical(g9)
    c: Coincident(g9,g10)
    c: Coincident(g10,g11)
    c: Coincident(g11,g12)
    c: Coincident(g12,g1)
    c: Horizontal(g12)
    c: Horizontal(g10)
    c: Horizontal(g2)
    c: Vertical(g11)
    c: Vertical(g1)
    c: Vertical(g7)
    c: Vertical(g1,g4)
    c: Vertical(g10,g7)
    c: Horizontal(g1,g10)
    c: Horizontal(g4,g7)
    c: Symmetric(g4,g10,g0)
    c: DistanceY(g6,g11) = 3.5
    c: DistanceY(g9,g9) = 1
    c: Equal(g11,g10)
    c: Equal(g7,g8)
    c: Equal(g2,g1)
    c: Equal(g12,g3)
FEATURE [PartDesign::Pad] Pad187
  Direction = (0,-1,2e-16)
  Length = 8
  Length2 = 10
  Placement = pos=(0,0,0) rot=(1,0,0;1.5708rad)
  Profile = -> Sketch191
  ReferenceAxis = -> Sketch191 [N_Axis]
  Type = 0
FEATURE [Sketcher::SketchObject] Sketch192
  FullyConstrained = true
  MapMode = 5
  Placement = pos=(0,-8,3.5e-15) rot=(1,0,0;1.5708rad)
  Support = -> [Pad187]
  sketch-geometry (10):
    g0: ArcOfCircle CenterX=-7.15 CenterY=7.15 CenterZ=0 NormalX=0 NormalY=0 NormalZ=1 AngleXU=0 Radius=2 StartAngle=1.5708 EndAngle=3.14159
    g1: LineSegment StartX=-7.15 StartY=9.15 StartZ=0 EndX=7.15 EndY=9.15 EndZ=0
    g2: ArcOfCircle CenterX=7.15 CenterY=7.15 CenterZ=0 NormalX=0 NormalY=0 NormalZ=1 AngleXU=0 Radius=2 StartAngle=3e-16 EndAngle=1.5708
    g3: LineSegment StartX=9.15 StartY=7.15 StartZ=0 EndX=9.15 EndY=-7.15 EndZ=0
    g4: ArcOfCircle CenterX=7.15 CenterY=-7.15 CenterZ=0 NormalX=0 NormalY=0 NormalZ=1 AngleXU=0 Radius=2 StartAngle=4.71239 EndAngle=6.28319
    g5: LineSegment StartX=7.15 StartY=-9.15 StartZ=0 EndX=-7.15 EndY=-9.15 EndZ=0
    g6: ArcOfCircle CenterX=-7.15 CenterY=-7.15 CenterZ=0 NormalX=0 NormalY=0 NormalZ=1 AngleXU=0 Radius=2 StartAngle=3.14159 EndAngle=4.71239
    g7: LineSegment StartX=-9.15 StartY=-7.15 StartZ=0 EndX=-9.15 EndY=7.15 EndZ=0
    g8: GeomPoint X=-9.15 Y=9.15 Z=0
    g9: GeomPoint X=9.15 Y=-9.15 Z=0
  constraints (23):
    c: Tangent(g0,g1) = 1.5708
    c: Tangent(g1,g2) = 1.5708
    c: Tangent(g2,g3) = 1.5708
    c: Tangent(g3,g4) = 1.5708
    c: Tangent(g4,g5) = 1.5708
    c: Tangent(g5,g6) = 1.5708
    c: Tangent(g6,g7) = 1.5708
    c: Tangent(g7,g0) = 1.5708
    c: Horizontal(g1)
    c: Horizontal(g5)
    c: Vertical(g3)
    c: Vertical(g7)
    c: Equal(g0,g2)
    c: Equal(g2,g4)
    c: Equal(g4,g6)
    c: PointOnObject(g8,g1)
    c: PointOnObject(g8,g7)
    c: PointOnObject(g9,g3)
    c: PointOnObject(g9,g5)
    c: Symmetric(g6,g2,g-1)
    c: DistanceY(g5,g0) = 18.3
    c: DistanceX(g0,g2) = 18.3
    c: Diameter(g0) = 4
FEATURE [PartDesign::Pad] Pad188
  BaseFeature = -> Pad187
  Direction = (0,-1,2e-16)
  Length = 1.2
  Length2 = 10
  Placement = pos=(0,0,0) rot=(1,0,0;1.5708rad)
  Profile = -> Sketch192
  ReferenceAxis = -> Sketch192 [N_Axis]
  Type = 0
FEATURE [Sketcher::SketchObject] Sketch193
  FullyConstrained = true
  MapMode = 5
  Placement = pos=(0,-8,3.5e-15) rot=(-1,0,0;1.5708rad)
  Support = -> [Pad188]
  sketch-geometry (20):
    g0: ArcOfCircle CenterX=-7.15 CenterY=7.15 CenterZ=0 NormalX=0 NormalY=0 NormalZ=1 AngleXU=0 Radius=2 StartAngle=1.5708 EndAngle=3.14159
    g1: LineSegment StartX=-7.15 StartY=9.15 StartZ=0 EndX=7.15 EndY=9.15 EndZ=0
    g2: ArcOfCircle CenterX=7.15 CenterY=7.15 CenterZ=0 NormalX=0 NormalY=0 NormalZ=1 AngleXU=0 Radius=2 StartAngle=2e-16 EndAngle=1.5708
    g3: LineSegment StartX=9.15 StartY=7.15 StartZ=0 EndX=9.15 EndY=-7.15 EndZ=0
    g4: ArcOfCircle CenterX=7.15 CenterY=-7.15 CenterZ=0 NormalX=0 NormalY=0 NormalZ=1 AngleXU=0 Radius=2 StartAngle=4.71239 EndAngle=6.28319
    g5: LineSegment StartX=7.15 StartY=-9.15 StartZ=0 EndX=-7.15 EndY=-9.15 EndZ=0
    g6: ArcOfCircle CenterX=-7.15 CenterY=-7.15 CenterZ=0 NormalX=0 NormalY=0 NormalZ=1 AngleXU=0 Radius=2 StartAngle=3.14159 EndAngle=4.71239
    g7: LineSegment StartX=-9.15 StartY=-7.15 StartZ=0 EndX=-9.15 EndY=7.15 EndZ=0
    g8: GeomPoint X=-9.15 Y=9.15 Z=0
    g9: GeomPoint X=9.15 Y=-9.15 Z=0
    g10: ArcOfCircle CenterX=-6.4 CenterY=6.4 CenterZ=0 NormalX=0 NormalY=0 NormalZ=1 AngleXU=0 Radius=1.25 StartAngle=1.5708 EndAngle=3.14159
    g11: LineSegment StartX=-6.4 StartY=7.65 StartZ=0 EndX=6.4 EndY=7.65 EndZ=0
    g12: ArcOfCircle CenterX=6.4 CenterY=6.4 CenterZ=0 NormalX=0 NormalY=0 NormalZ=1 AngleXU=0 Radius=1.25 StartAngle=2e-16 EndAngle=1.5708
    g13: LineSegment StartX=7.65 StartY=6.4 StartZ=0 EndX=7.65 EndY=-6.4 EndZ=0
    g14: ArcOfCircle CenterX=6.4 CenterY=-6.4 CenterZ=0 NormalX=0 NormalY=0 NormalZ=1 AngleXU=0 Radius=1.25 StartAngle=4.71239 EndAngle=6.28319
    g15: LineSegment StartX=6.4 StartY=-7.65 StartZ=0 EndX=-6.4 EndY=-7.65 EndZ=0
    g16: ArcOfCircle CenterX=-6.4 CenterY=-6.4 CenterZ=0 NormalX=0 NormalY=0 NormalZ=1 AngleXU=0 Radius=1.25 StartAngle=3.14159 EndAngle=4.71239
    g17: LineSegment StartX=-7.65 StartY=-6.4 StartZ=0 EndX=-7.65 EndY=6.4 EndZ=0
    g18: GeomPoint X=-7.65 Y=7.65 Z=0
    g19: GeomPoint X=7.65 Y=-7.65 Z=0
  constraints (46):
    c: Tangent(g0,g1) = 1.5708
    c: Tangent(g1,g2) = 1.5708
    c: Tangent(g2,g3) = 1.5708
    c: Tangent(g3,g4) = 1.5708
    c: Tangent(g4,g5) = 1.5708
    c: Tangent(g5,g6) = 1.5708
    c: Tangent(g6,g7) = 1.5708
    c: Tangent(g7,g0) = 1.5708
    c: Horizontal(g1)
    c: Horizontal(g5)
    c: Vertical(g3)
    c: Vertical(g7)
    c: Equal(g0,g2)
    c: Equal(g2,g4)
    c: Equal(g4,g6)
    c: PointOnObject(g8,g1)
    c: PointOnObject(g8,g7)
    c: PointOnObject(g9,g3)
    c: PointOnObject(g9,g5)
    c: DistanceY(g4,g1) = 18.3
    c: DistanceX(g0,g2) = 18.3
    c: Symmetric(g6,g2,g-1)
    c: Diameter(g0) = 4
    c: Tangent(g10,g11) = 1.5708
    c: Tangent(g11,g12) = 1.5708
    c: Tangent(g12,g13) = 1.5708
    c: Tangent(g13,g14) = 1.5708
    c: Tangent(g14,g15) = 1.5708
    c: Tangent(g15,g16) = 1.5708
    c: Tangent(g16,g17) = 1.5708
    c: Tangent(g17,g10) = 1.5708
    c: Horizontal(g11)
    c: Horizontal(g15)
    c: Vertical(g13)
    c: Vertical(g17)
    c: Equal(g10,g12)
    c: Equal(g12,g14)
    c: Equal(g14,g16)
    c: PointOnObject(g18,g11)
    c: PointOnObject(g18,g17)
    c: PointOnObject(g19,g13)
    c: PointOnObject(g19,g15)
    c: Symmetric(g10,g14,g-1)
    c: Diameter(g10) = 2.5
    c: DistanceY(g10,g0) = 1.5
    c: Equal(g11,g13)
FEATURE [PartDesign::Pad] Pad189
  BaseFeature = -> Pad188
  Direction = (0,1,-2e-16)
  Length = 8
  Length2 = 10
  Placement = pos=(0,0,0) rot=(1,0,0;1.5708rad)
  Profile = -> Sketch193
  ReferenceAxis = -> Sketch193 [N_Axis]
  Type = 0
FEATURE [PartDesign::Body] Body052  label="standardKeyCap001"
  Group = -> [Sketch191,Pad187,Sketch192,Pad188,Sketch193,Pad189]
  Origin = -> Origin052
  Placement = pos=(9.65,-9,5) rot=(0,0,1;0rad)
  Tip = -> Pad189
FEATURE [Sketcher::SketchObject] Sketch194
  FullyConstrained = true
  MapMode = 5
  Placement = pos=(0,0,0) rot=(1,0,0;1.5708rad)
  Support = -> [XZ_Plane053]
  sketch-geometry (13):
    g0: Circle CenterX=0 CenterY=0 CenterZ=0 NormalX=0 NormalY=0 NormalZ=1 AngleXU=0 Radius=2.9
    g1: LineSegment StartX=-0.5 StartY=1.75 StartZ=0 EndX=-0.5 EndY=0.5 EndZ=0
    g2: LineSegment StartX=-0.5 StartY=0.5 StartZ=0 EndX=-1.75 EndY=0.5 EndZ=0
    g3: LineSegment StartX=-1.75 StartY=0.5 StartZ=0 EndX=-1.75 EndY=-0.5 EndZ=0
    g4: LineSegment StartX=-1.75 StartY=-0.5 StartZ=0 EndX=-0.5 EndY=-0.5 EndZ=0
    g5: LineSegment StartX=-0.5 StartY=-0.5 StartZ=0 EndX=-0.5 EndY=-1.75 EndZ=0
    g6: LineSegment StartX=-0.5 StartY=-1.75 StartZ=0 EndX=0.5 EndY=-1.75 EndZ=0
    g7: LineSegment StartX=0.5 StartY=-1.75 StartZ=0 EndX=0.5 EndY=-0.5 EndZ=0
    g8: LineSegment StartX=0.5 StartY=-0.5 StartZ=0 EndX=1.75 EndY=-0.5 EndZ=0
    g9: LineSegment StartX=1.75 StartY=-0.5 StartZ=0 EndX=1.75 EndY=0.5 EndZ=0
    g10: LineSegment StartX=1.75 StartY=0.5 StartZ=0 EndX=0.5 EndY=0.5 EndZ=0
    g11: LineSegment StartX=0.5 StartY=0.5 StartZ=0 EndX=0.5 EndY=1.75 EndZ=0
    g12: LineSegment StartX=0.5 StartY=1.75 StartZ=0 EndX=-0.5 EndY=1.75 EndZ=0
  constraints (37):
    c: Coincident(g0,g-1)
    c: Diameter(g0) = 5.8
    c: Coincident(g1,g2)
    c: Coincident(g2,g3)
    c: Vertical(g3)
    c: Coincident(g3,g4)
    c: Horizontal(g4)
    c: Coincident(g4,g5)
    c: Vertical(g5)
    c: Coincident(g5,g6)
    c: Horizontal(g6)
    c: Coincident(g6,g7)
    c: Coincident(g7,g8)
    c: Horizontal(g8)
    c: Coincident(g8,g9)
    c: Vertical(g9)
    c: Coincident(g9,g10)
    c: Coincident(g10,g11)
    c: Coincident(g11,g12)
    c: Coincident(g12,g1)
    c: Horizontal(g12)
    c: Horizontal(g10)
    c: Horizontal(g2)
    c: Vertical(g11)
    c: Vertical(g1)
    c: Vertical(g7)
    c: Vertical(g1,g4)
    c: Vertical(g10,g7)
    c: Horizontal(g1,g10)
    c: Horizontal(g4,g7)
    c: Symmetric(g4,g10,g0)
    c: DistanceY(g6,g11) = 3.5
    c: DistanceY(g9,g9) = 1
    c: Equal(g11,g10)
    c: Equal(g7,g8)
    c: Equal(g2,g1)
    c: Equal(g12,g3)
FEATURE [PartDesign::Pad] Pad190
  Direction = (0,-1,2e-16)
  Length = 8
  Length2 = 10
  Placement = pos=(0,0,0) rot=(1,0,0;1.5708rad)
  Profile = -> Sketch194
  ReferenceAxis = -> Sketch194 [N_Axis]
  Type = 0
FEATURE [Sketcher::SketchObject] Sketch195
  FullyConstrained = true
  MapMode = 5
  Placement = pos=(0,-8,3.5e-15) rot=(1,0,0;1.5708rad)
  Support = -> [Pad190]
  sketch-geometry (10):
    g0: ArcOfCircle CenterX=-7.15 CenterY=7.15 CenterZ=0 NormalX=0 NormalY=0 NormalZ=1 AngleXU=0 Radius=2 StartAngle=1.5708 EndAngle=3.14159
    g1: LineSegment StartX=-7.15 StartY=9.15 StartZ=0 EndX=7.15 EndY=9.15 EndZ=0
    g2: ArcOfCircle CenterX=7.15 CenterY=7.15 CenterZ=0 NormalX=0 NormalY=0 NormalZ=1 AngleXU=0 Radius=2 StartAngle=3e-16 EndAngle=1.5708
    g3: LineSegment StartX=9.15 StartY=7.15 StartZ=0 EndX=9.15 EndY=-7.15 EndZ=0
    g4: ArcOfCircle CenterX=7.15 CenterY=-7.15 CenterZ=0 NormalX=0 NormalY=0 NormalZ=1 AngleXU=0 Radius=2 StartAngle=4.71239 EndAngle=6.28319
    g5: LineSegment StartX=7.15 StartY=-9.15 StartZ=0 EndX=-7.15 EndY=-9.15 EndZ=0
    g6: ArcOfCircle CenterX=-7.15 CenterY=-7.15 CenterZ=0 NormalX=0 NormalY=0 NormalZ=1 AngleXU=0 Radius=2 StartAngle=3.14159 EndAngle=4.71239
    g7: LineSegment StartX=-9.15 StartY=-7.15 StartZ=0 EndX=-9.15 EndY=7.15 EndZ=0
    g8: GeomPoint X=-9.15 Y=9.15 Z=0
    g9: GeomPoint X=9.15 Y=-9.15 Z=0
  constraints (23):
    c: Tangent(g0,g1) = 1.5708
    c: Tangent(g1,g2) = 1.5708
    c: Tangent(g2,g3) = 1.5708
    c: Tangent(g3,g4) = 1.5708
    c: Tangent(g4,g5) = 1.5708
    c: Tangent(g5,g6) = 1.5708
    c: Tangent(g6,g7) = 1.5708
    c: Tangent(g7,g0) = 1.5708
    c: Horizontal(g1)
    c: Horizontal(g5)
    c: Vertical(g3)
    c: Vertical(g7)
    c: Equal(g0,g2)
    c: Equal(g2,g4)
    c: Equal(g4,g6)
    c: PointOnObject(g8,g1)
    c: PointOnObject(g8,g7)
    c: PointOnObject(g9,g3)
    c: PointOnObject(g9,g5)
    c: Symmetric(g6,g2,g-1)
    c: DistanceY(g5,g0) = 18.3
    c: DistanceX(g0,g2) = 18.3
    c: Diameter(g0) = 4
FEATURE [PartDesign::Pad] Pad191
  BaseFeature = -> Pad190
  Direction = (0,-1,2e-16)
  Length = 1.2
  Length2 = 10
  Placement = pos=(0,0,0) rot=(1,0,0;1.5708rad)
  Profile = -> Sketch195
  ReferenceAxis = -> Sketch195 [N_Axis]
  Type = 0
FEATURE [Sketcher::SketchObject] Sketch196
  FullyConstrained = true
  MapMode = 5
  Placement = pos=(0,-8,3.5e-15) rot=(-1,0,0;1.5708rad)
  Support = -> [Pad191]
  sketch-geometry (20):
    g0: ArcOfCircle CenterX=-7.15 CenterY=7.15 CenterZ=0 NormalX=0 NormalY=0 NormalZ=1 AngleXU=0 Radius=2 StartAngle=1.5708 EndAngle=3.14159
    g1: LineSegment StartX=-7.15 StartY=9.15 StartZ=0 EndX=7.15 EndY=9.15 EndZ=0
    g2: ArcOfCircle CenterX=7.15 CenterY=7.15 CenterZ=0 NormalX=0 NormalY=0 NormalZ=1 AngleXU=0 Radius=2 StartAngle=2e-16 EndAngle=1.5708
    g3: LineSegment StartX=9.15 StartY=7.15 StartZ=0 EndX=9.15 EndY=-7.15 EndZ=0
    g4: ArcOfCircle CenterX=7.15 CenterY=-7.15 CenterZ=0 NormalX=0 NormalY=0 NormalZ=1 AngleXU=0 Radius=2 StartAngle=4.71239 EndAngle=6.28319
    g5: LineSegment StartX=7.15 StartY=-9.15 StartZ=0 EndX=-7.15 EndY=-9.15 EndZ=0
    g6: ArcOfCircle CenterX=-7.15 CenterY=-7.15 CenterZ=0 NormalX=0 NormalY=0 NormalZ=1 AngleXU=0 Radius=2 StartAngle=3.14159 EndAngle=4.71239
    g7: LineSegment StartX=-9.15 StartY=-7.15 StartZ=0 EndX=-9.15 EndY=7.15 EndZ=0
    g8: GeomPoint X=-9.15 Y=9.15 Z=0
    g9: GeomPoint X=9.15 Y=-9.15 Z=0
    g10: ArcOfCircle CenterX=-6.4 CenterY=6.4 CenterZ=0 NormalX=0 NormalY=0 NormalZ=1 AngleXU=0 Radius=1.25 StartAngle=1.5708 EndAngle=3.14159
    g11: LineSegment StartX=-6.4 StartY=7.65 StartZ=0 EndX=6.4 EndY=7.65 EndZ=0
    g12: ArcOfCircle CenterX=6.4 CenterY=6.4 CenterZ=0 NormalX=0 NormalY=0 NormalZ=1 AngleXU=0 Radius=1.25 StartAngle=2e-16 EndAngle=1.5708
    g13: LineSegment StartX=7.65 StartY=6.4 StartZ=0 EndX=7.65 EndY=-6.4 EndZ=0
    g14: ArcOfCircle CenterX=6.4 CenterY=-6.4 CenterZ=0 NormalX=0 NormalY=0 NormalZ=1 AngleXU=0 Radius=1.25 StartAngle=4.71239 EndAngle=6.28319
    g15: LineSegment StartX=6.4 StartY=-7.65 StartZ=0 EndX=-6.4 EndY=-7.65 EndZ=0
    g16: ArcOfCircle CenterX=-6.4 CenterY=-6.4 CenterZ=0 NormalX=0 NormalY=0 NormalZ=1 AngleXU=0 Radius=1.25 StartAngle=3.14159 EndAngle=4.71239
    g17: LineSegment StartX=-7.65 StartY=-6.4 StartZ=0 EndX=-7.65 EndY=6.4 EndZ=0
    g18: GeomPoint X=-7.65 Y=7.65 Z=0
    g19: GeomPoint X=7.65 Y=-7.65 Z=0
  constraints (46):
    c: Tangent(g0,g1) = 1.5708
    c: Tangent(g1,g2) = 1.5708
    c: Tangent(g2,g3) = 1.5708
    c: Tangent(g3,g4) = 1.5708
    c: Tangent(g4,g5) = 1.5708
    c: Tangent(g5,g6) = 1.5708
    c: Tangent(g6,g7) = 1.5708
    c: Tangent(g7,g0) = 1.5708
    c: Horizontal(g1)
    c: Horizontal(g5)
    c: Vertical(g3)
    c: Vertical(g7)
    c: Equal(g0,g2)
    c: Equal(g2,g4)
    c: Equal(g4,g6)
    c: PointOnObject(g8,g1)
    c: PointOnObject(g8,g7)
    c: PointOnObject(g9,g3)
    c: PointOnObject(g9,g5)
    c: DistanceY(g4,g1) = 18.3
    c: DistanceX(g0,g2) = 18.3
    c: Symmetric(g6,g2,g-1)
    c: Diameter(g0) = 4
    c: Tangent(g10,g11) = 1.5708
    c: Tangent(g11,g12) = 1.5708
    c: Tangent(g12,g13) = 1.5708
    c: Tangent(g13,g14) = 1.5708
    c: Tangent(g14,g15) = 1.5708
    c: Tangent(g15,g16) = 1.5708
    c: Tangent(g16,g17) = 1.5708
    c: Tangent(g17,g10) = 1.5708
    c: Horizontal(g11)
    c: Horizontal(g15)
    c: Vertical(g13)
    c: Vertical(g17)
    c: Equal(g10,g12)
    c: Equal(g12,g14)
    c: Equal(g14,g16)
    c: PointOnObject(g18,g11)
    c: PointOnObject(g18,g17)
    c: PointOnObject(g19,g13)
    c: PointOnObject(g19,g15)
    c: Symmetric(g10,g14,g-1)
    c: Diameter(g10) = 2.5
    c: DistanceY(g10,g0) = 1.5
    c: Equal(g11,g13)
FEATURE [PartDesign::Pad] Pad192
  BaseFeature = -> Pad191
  Direction = (0,1,-2e-16)
  Length = 8
  Length2 = 10
  Placement = pos=(0,0,0) rot=(1,0,0;1.5708rad)
  Profile = -> Sketch196
  ReferenceAxis = -> Sketch196 [N_Axis]
  Type = 0
FEATURE [PartDesign::Body] Body053  label="standardKeyCap002"
  Group = -> [Sketch194,Pad190,Sketch195,Pad191,Sketch196,Pad192]
  Origin = -> Origin053
  Placement = pos=(9.65,-9,5) rot=(0,0,1;0rad)
  Tip = -> Pad192
FEATURE [Sketcher::SketchObject] Sketch197
  FullyConstrained = true
  MapMode = 5
  Placement = pos=(0,0,0) rot=(1,0,0;1.5708rad)
  Support = -> [XZ_Plane054]
  sketch-geometry (13):
    g0: Circle CenterX=0 CenterY=0 CenterZ=0 NormalX=0 NormalY=0 NormalZ=1 AngleXU=0 Radius=2.9
    g1: LineSegment StartX=-0.5 StartY=1.75 StartZ=0 EndX=-0.5 EndY=0.5 EndZ=0
    g2: LineSegment StartX=-0.5 StartY=0.5 StartZ=0 EndX=-1.75 EndY=0.5 EndZ=0
    g3: LineSegment StartX=-1.75 StartY=0.5 StartZ=0 EndX=-1.75 EndY=-0.5 EndZ=0
    g4: LineSegment StartX=-1.75 StartY=-0.5 StartZ=0 EndX=-0.5 EndY=-0.5 EndZ=0
    g5: LineSegment StartX=-0.5 StartY=-0.5 StartZ=0 EndX=-0.5 EndY=-1.75 EndZ=0
    g6: LineSegment StartX=-0.5 StartY=-1.75 StartZ=0 EndX=0.5 EndY=-1.75 EndZ=0
    g7: LineSegment StartX=0.5 StartY=-1.75 StartZ=0 EndX=0.5 EndY=-0.5 EndZ=0
    g8: LineSegment StartX=0.5 StartY=-0.5 StartZ=0 EndX=1.75 EndY=-0.5 EndZ=0
    g9: LineSegment StartX=1.75 StartY=-0.5 StartZ=0 EndX=1.75 EndY=0.5 EndZ=0
    g10: LineSegment StartX=1.75 StartY=0.5 StartZ=0 EndX=0.5 EndY=0.5 EndZ=0
    g11: LineSegment StartX=0.5 StartY=0.5 StartZ=0 EndX=0.5 EndY=1.75 EndZ=0
    g12: LineSegment StartX=0.5 StartY=1.75 StartZ=0 EndX=-0.5 EndY=1.75 EndZ=0
  constraints (37):
    c: Coincident(g0,g-1)
    c: Diameter(g0) = 5.8
    c: Coincident(g1,g2)
    c: Coincident(g2,g3)
    c: Vertical(g3)
    c: Coincident(g3,g4)
    c: Horizontal(g4)
    c: Coincident(g4,g5)
    c: Vertical(g5)
    c: Coincident(g5,g6)
    c: Horizontal(g6)
    c: Coincident(g6,g7)
    c: Coincident(g7,g8)
    c: Horizontal(g8)
    c: Coincident(g8,g9)
    c: Vertical(g9)
    c: Coincident(g9,g10)
    c: Coincident(g10,g11)
    c: Coincident(g11,g12)
    c: Coincident(g12,g1)
    c: Horizontal(g12)
    c: Horizontal(g10)
    c: Horizontal(g2)
    c: Vertical(g11)
    c: Vertical(g1)
    c: Vertical(g7)
    c: Vertical(g1,g4)
    c: Vertical(g10,g7)
    c: Horizontal(g1,g10)
    c: Horizontal(g4,g7)
    c: Symmetric(g4,g10,g0)
    c: DistanceY(g6,g11) = 3.5
    c: DistanceY(g9,g9) = 1
    c: Equal(g11,g10)
    c: Equal(g7,g8)
    c: Equal(g2,g1)
    c: Equal(g12,g3)
FEATURE [PartDesign::Pad] Pad193
  Direction = (0,-1,2e-16)
  Length = 8
  Length2 = 10
  Placement = pos=(0,0,0) rot=(1,0,0;1.5708rad)
  Profile = -> Sketch197
  ReferenceAxis = -> Sketch197 [N_Axis]
  Type = 0
FEATURE [Sketcher::SketchObject] Sketch198
  FullyConstrained = true
  MapMode = 5
  Placement = pos=(0,-8,3.5e-15) rot=(1,0,0;1.5708rad)
  Support = -> [Pad193]
  sketch-geometry (10):
    g0: ArcOfCircle CenterX=-7.15 CenterY=7.15 CenterZ=0 NormalX=0 NormalY=0 NormalZ=1 AngleXU=0 Radius=2 StartAngle=1.5708 EndAngle=3.14159
    g1: LineSegment StartX=-7.15 StartY=9.15 StartZ=0 EndX=7.15 EndY=9.15 EndZ=0
    g2: ArcOfCircle CenterX=7.15 CenterY=7.15 CenterZ=0 NormalX=0 NormalY=0 NormalZ=1 AngleXU=0 Radius=2 StartAngle=3e-16 EndAngle=1.5708
    g3: LineSegment StartX=9.15 StartY=7.15 StartZ=0 EndX=9.15 EndY=-7.15 EndZ=0
    g4: ArcOfCircle CenterX=7.15 CenterY=-7.15 CenterZ=0 NormalX=0 NormalY=0 NormalZ=1 AngleXU=0 Radius=2 StartAngle=4.71239 EndAngle=6.28319
    g5: LineSegment StartX=7.15 StartY=-9.15 StartZ=0 EndX=-7.15 EndY=-9.15 EndZ=0
    g6: ArcOfCircle CenterX=-7.15 CenterY=-7.15 CenterZ=0 NormalX=0 NormalY=0 NormalZ=1 AngleXU=0 Radius=2 StartAngle=3.14159 EndAngle=4.71239
    g7: LineSegment StartX=-9.15 StartY=-7.15 StartZ=0 EndX=-9.15 EndY=7.15 EndZ=0
    g8: GeomPoint X=-9.15 Y=9.15 Z=0
    g9: GeomPoint X=9.15 Y=-9.15 Z=0
  constraints (23):
    c: Tangent(g0,g1) = 1.5708
    c: Tangent(g1,g2) = 1.5708
    c: Tangent(g2,g3) = 1.5708
    c: Tangent(g3,g4) = 1.5708
    c: Tangent(g4,g5) = 1.5708
    c: Tangent(g5,g6) = 1.5708
    c: Tangent(g6,g7) = 1.5708
    c: Tangent(g7,g0) = 1.5708
    c: Horizontal(g1)
    c: Horizontal(g5)
    c: Vertical(g3)
    c: Vertical(g7)
    c: Equal(g0,g2)
    c: Equal(g2,g4)
    c: Equal(g4,g6)
    c: PointOnObject(g8,g1)
    c: PointOnObject(g8,g7)
    c: PointOnObject(g9,g3)
    c: PointOnObject(g9,g5)
    c: Symmetric(g6,g2,g-1)
    c: DistanceY(g5,g0) = 18.3
    c: DistanceX(g0,g2) = 18.3
    c: Diameter(g0) = 4
FEATURE [PartDesign::Pad] Pad194
  BaseFeature = -> Pad193
  Direction = (0,-1,2e-16)
  Length = 1.2
  Length2 = 10
  Placement = pos=(0,0,0) rot=(1,0,0;1.5708rad)
  Profile = -> Sketch198
  ReferenceAxis = -> Sketch198 [N_Axis]
  Type = 0
FEATURE [Sketcher::SketchObject] Sketch199
  FullyConstrained = true
  MapMode = 5
  Placement = pos=(0,-8,3.5e-15) rot=(-1,0,0;1.5708rad)
  Support = -> [Pad194]
  sketch-geometry (20):
    g0: ArcOfCircle CenterX=-7.15 CenterY=7.15 CenterZ=0 NormalX=0 NormalY=0 NormalZ=1 AngleXU=0 Radius=2 StartAngle=1.5708 EndAngle=3.14159
    g1: LineSegment StartX=-7.15 StartY=9.15 StartZ=0 EndX=7.15 EndY=9.15 EndZ=0
    g2: ArcOfCircle CenterX=7.15 CenterY=7.15 CenterZ=0 NormalX=0 NormalY=0 NormalZ=1 AngleXU=0 Radius=2 StartAngle=2e-16 EndAngle=1.5708
    g3: LineSegment StartX=9.15 StartY=7.15 StartZ=0 EndX=9.15 EndY=-7.15 EndZ=0
    g4: ArcOfCircle CenterX=7.15 CenterY=-7.15 CenterZ=0 NormalX=0 NormalY=0 NormalZ=1 AngleXU=0 Radius=2 StartAngle=4.71239 EndAngle=6.28319
    g5: LineSegment StartX=7.15 StartY=-9.15 StartZ=0 EndX=-7.15 EndY=-9.15 EndZ=0
    g6: ArcOfCircle CenterX=-7.15 CenterY=-7.15 CenterZ=0 NormalX=0 NormalY=0 NormalZ=1 AngleXU=0 Radius=2 StartAngle=3.14159 EndAngle=4.71239
    g7: LineSegment StartX=-9.15 StartY=-7.15 StartZ=0 EndX=-9.15 EndY=7.15 EndZ=0
    g8: GeomPoint X=-9.15 Y=9.15 Z=0
    g9: GeomPoint X=9.15 Y=-9.15 Z=0
    g10: ArcOfCircle CenterX=-6.4 CenterY=6.4 CenterZ=0 NormalX=0 NormalY=0 NormalZ=1 AngleXU=0 Radius=1.25 StartAngle=1.5708 EndAngle=3.14159
    g11: LineSegment StartX=-6.4 StartY=7.65 StartZ=0 EndX=6.4 EndY=7.65 EndZ=0
    g12: ArcOfCircle CenterX=6.4 CenterY=6.4 CenterZ=0 NormalX=0 NormalY=0 NormalZ=1 AngleXU=0 Radius=1.25 StartAngle=2e-16 EndAngle=1.5708
    g13: LineSegment StartX=7.65 StartY=6.4 StartZ=0 EndX=7.65 EndY=-6.4 EndZ=0
    g14: ArcOfCircle CenterX=6.4 CenterY=-6.4 CenterZ=0 NormalX=0 NormalY=0 NormalZ=1 AngleXU=0 Radius=1.25 StartAngle=4.71239 EndAngle=6.28319
    g15: LineSegment StartX=6.4 StartY=-7.65 StartZ=0 EndX=-6.4 EndY=-7.65 EndZ=0
    g16: ArcOfCircle CenterX=-6.4 CenterY=-6.4 CenterZ=0 NormalX=0 NormalY=0 NormalZ=1 AngleXU=0 Radius=1.25 StartAngle=3.14159 EndAngle=4.71239
    g17: LineSegment StartX=-7.65 StartY=-6.4 StartZ=0 EndX=-7.65 EndY=6.4 EndZ=0
    g18: GeomPoint X=-7.65 Y=7.65 Z=0
    g19: GeomPoint X=7.65 Y=-7.65 Z=0
  constraints (46):
    c: Tangent(g0,g1) = 1.5708
    c: Tangent(g1,g2) = 1.5708
    c: Tangent(g2,g3) = 1.5708
    c: Tangent(g3,g4) = 1.5708
    c: Tangent(g4,g5) = 1.5708
    c: Tangent(g5,g6) = 1.5708
    c: Tangent(g6,g7) = 1.5708
    c: Tangent(g7,g0) = 1.5708
    c: Horizontal(g1)
    c: Horizontal(g5)
    c: Vertical(g3)
    c: Vertical(g7)
    c: Equal(g0,g2)
    c: Equal(g2,g4)
    c: Equal(g4,g6)
    c: PointOnObject(g8,g1)
    c: PointOnObject(g8,g7)
    c: PointOnObject(g9,g3)
    c: PointOnObject(g9,g5)
    c: DistanceY(g4,g1) = 18.3
    c: DistanceX(g0,g2) = 18.3
    c: Symmetric(g6,g2,g-1)
    c: Diameter(g0) = 4
    c: Tangent(g10,g11) = 1.5708
    c: Tangent(g11,g12) = 1.5708
    c: Tangent(g12,g13) = 1.5708
    c: Tangent(g13,g14) = 1.5708
    c: Tangent(g14,g15) = 1.5708
    c: Tangent(g15,g16) = 1.5708
    c: Tangent(g16,g17) = 1.5708
    c: Tangent(g17,g10) = 1.5708
    c: Horizontal(g11)
    c: Horizontal(g15)
    c: Vertical(g13)
    c: Vertical(g17)
    c: Equal(g10,g12)
    c: Equal(g12,g14)
    c: Equal(g14,g16)
    c: PointOnObject(g18,g11)
    c: PointOnObject(g18,g17)
    c: PointOnObject(g19,g13)
    c: PointOnObject(g19,g15)
    c: Symmetric(g10,g14,g-1)
    c: Diameter(g10) = 2.5
    c: DistanceY(g10,g0) = 1.5
    c: Equal(g11,g13)
FEATURE [PartDesign::Pad] Pad195
  BaseFeature = -> Pad194
  Direction = (0,1,-2e-16)
  Length = 8
  Length2 = 10
  Placement = pos=(0,0,0) rot=(1,0,0;1.5708rad)
  Profile = -> Sketch199
  ReferenceAxis = -> Sketch199 [N_Axis]
  Type = 0
FEATURE [PartDesign::Body] Body054  label="standardKeyCap003"
  Group = -> [Sketch197,Pad193,Sketch198,Pad194,Sketch199,Pad195]
  Origin = -> Origin054
  Placement = pos=(9.65,-9,5) rot=(0,0,1;0rad)
  Tip = -> Pad195
FEATURE [Part::FeaturePython] Array013  # Draft array (typed FeaturePython)
  AlwaysSyncPlacement = false
  Angle = 360
  ArrayType = 0
  Axis = (0,0,1)
  Base = -> Body051
  Center = (0,0,0)
  Count = 12
  ExpandArray = false
  Fuse = false
  IntervalAxis = (0,0,0)
  IntervalX = (23.5,0,0)
  IntervalY = (0,100,0)
  IntervalZ = (0,0,40)
  NumberCircles = 3
  NumberPolar = 5
  NumberX = 12
  NumberY = 1
  NumberZ = 1
  Placement = pos=(0,0,-4) rot=(0,1,0;0rad)
  PlacementList = 12 placements: arithmetic series from (9.65,-9,5) step (23.5,0,0) to (268.15,-9,5)
  RadialDistance = 50
  ScaleList = (12) [(1,1,1),(1,1,1),(1,1,1),(1,1,1),(1,1,1),(1,1,1),(1,1,1),(1,1,1),(1,1,1),(1,1,1),(1,1,1),(1,1,1)]
  Symmetry = 1
  TangentialDistance = 25
FEATURE [Part::FeaturePython] Array016  # Draft array (typed FeaturePython)
  AlwaysSyncPlacement = false
  Angle = 360
  ArrayType = 0
  Axis = (0,0,1)
  Base = -> Body052
  Center = (0,0,0)
  Count = 12
  ExpandArray = false
  Fuse = false
  IntervalAxis = (0,0,0)
  IntervalX = (23.5,0,0)
  IntervalY = (0,100,0)
  IntervalZ = (0,0,40)
  NumberCircles = 3
  NumberPolar = 5
  NumberX = 12
  NumberY = 1
  NumberZ = 1
  Placement = pos=(289.55,0,-16.76) rot=(0,1,0;3.14159rad)
  PlacementList = 12 placements: arithmetic series from (9.65,-9,5) step (23.5,0,0) to (268.15,-9,5)
  RadialDistance = 50
  ScaleList = (12) [(1,1,1),(1,1,1),(1,1,1),(1,1,1),(1,1,1),(1,1,1),(1,1,1),(1,1,1),(1,1,1),(1,1,1),(1,1,1),(1,1,1)]
  Symmetry = 1
  TangentialDistance = 25
FEATURE [Part::FeaturePython] Array014  # Draft array (typed FeaturePython)
  AlwaysSyncPlacement = false
  Angle = 360
  ArrayType = 0
  Axis = (0,0,1)
  Base = -> Body053
  Center = (0,0,0)
  Count = 12
  ExpandArray = false
  Fuse = false
  IntervalAxis = (0,0,0)
  IntervalX = (23.5,0,0)
  IntervalY = (0,100,0)
  IntervalZ = (0,0,40)
  NumberCircles = 3
  NumberPolar = 5
  NumberX = 12
  NumberY = 1
  NumberZ = 1
  Placement = pos=(301.3,0,-38.52) rot=(0,1,0;3.14159rad)
  PlacementList = 12 placements: arithmetic series from (9.65,-9,5) step (23.5,0,0) to (268.15,-9,5)
  RadialDistance = 50
  ScaleList = (12) [(1,1,1),(1,1,1),(1,1,1),(1,1,1),(1,1,1),(1,1,1),(1,1,1),(1,1,1),(1,1,1),(1,1,1),(1,1,1),(1,1,1)]
  Symmetry = 1
  TangentialDistance = 25
FEATURE [Part::FeaturePython] Array015  # Draft array (typed FeaturePython)
  AlwaysSyncPlacement = false
  Angle = 360
  ArrayType = 0
  Axis = (0,0,1)
  Base = -> Body054
  Center = (0,0,0)
  Count = 12
  ExpandArray = false
  Fuse = false
  IntervalAxis = (0,0,0)
  IntervalX = (23.5,0,0)
  IntervalY = (0,100,0)
  IntervalZ = (0,0,40)
  NumberCircles = 3
  NumberPolar = 5
  NumberX = 12
  NumberY = 1
  NumberZ = 1
  Placement = pos=(35.25,0,-71.52) rot=(0,1,0;0rad)
  PlacementList = 12 placements: arithmetic series from (9.65,-9,5) step (23.5,0,0) to (268.15,-9,5)
  RadialDistance = 50
  ScaleList = (12) [(1,1,1),(1,1,1),(1,1,1),(1,1,1),(1,1,1),(1,1,1),(1,1,1),(1,1,1),(1,1,1),(1,1,1),(1,1,1),(1,1,1)]
  Symmetry = 1
  TangentialDistance = 25
FEATURE [App::DocumentObjectGroup] Group004  label="keyCapsCaps"
  Group = -> [Array013,Array016,Array014,Array015]
FEATURE [PartDesign::ShapeBinder] CopyCut022
  Placement = pos=(9.65,0,20.5) rot=(-1,0,0;1.5708rad)
  TraceSupport = false
FEATURE [Sketcher::SketchObject] Sketch255
  FullyConstrained = true
  MapMode = 5
  Placement = pos=(0,0,0) rot=(1,0,0;1.5708rad)
  Support = -> [XZ_Plane084]
  sketch-geometry (6):
    g0: LineSegment StartX=-4 StartY=7.5 StartZ=0 EndX=4 EndY=7.5 EndZ=0
    g1: LineSegment StartX=6.5 StartY=-12.5 StartZ=0 EndX=-6.5 EndY=-12.5 EndZ=0
    g2: LineSegment StartX=-6.5 StartY=-12.5 StartZ=0 EndX=-6.5 EndY=2.5 EndZ=0
    g3: LineSegment StartX=-6.5 StartY=2.5 StartZ=0 EndX=-4 EndY=7.5 EndZ=0
    g4: LineSegment StartX=6.5 StartY=-12.5 StartZ=0 EndX=6.5 EndY=2.5 EndZ=0
    g5: LineSegment StartX=6.5 StartY=2.5 StartZ=0 EndX=4 EndY=7.5 EndZ=0
  constraints (18):
    c: Horizontal(g0)
    c: Horizontal(g1)
    c: DistanceY(g1,g0) = 20
    c: DistanceY(g-1,g0) = 7.5
    c: DistanceX(g1,g-1) = 6.5
    c: DistanceX(g1,g1) = 13
    c: DistanceX(g0,g0) = 8
    c: Coincident(g1,g2)
    c: Vertical(g2)
    c: Coincident(g2,g3)
    c: Coincident(g3,g0)
    c: Coincident(g1,g4)
    c: Vertical(g4)
    c: Coincident(g4,g5)
    c: Coincident(g5,g0)
    c: DistanceX(g0,g-1) = 4
    c: Horizontal(g2,g4)
    c: DistanceY(g2,g0) = 5
FEATURE [PartDesign::Pad] Pad242
  Direction = (0,-1,-2e-16)
  Length = 11
  Length2 = 10
  Placement = pos=(0,0,0) rot=(1,0,0;1.5708rad)
  Profile = -> Sketch255
  ReferenceAxis = -> Sketch255 [N_Axis]
  Type = 0
FEATURE [PartDesign::Body] Body084
  Group = -> [Sketch255,Pad242]
  Origin = -> Origin084
  Placement = pos=(8.95,0,6.5) rot=(0,0,1;0rad)
  Tip = -> Pad242
FEATURE [Sketcher::SketchObject] Sketch256
  FullyConstrained = true
  MapMode = 5
  Support = -> [XY_Plane085]
  sketch-geometry (12):
    g0: Circle CenterX=10.8779 CenterY=-4.825 CenterZ=0 NormalX=0 NormalY=0 NormalZ=1 AngleXU=0 Radius=1.45
    g1: Circle CenterX=-10.8779 CenterY=4.825 CenterZ=0 NormalX=0 NormalY=0 NormalZ=1 AngleXU=0 Radius=1.45
    g2: ArcOfCircle CenterX=-12.35 CenterY=6.35 CenterZ=0 NormalX=0 NormalY=0 NormalZ=1 AngleXU=0 Radius=1.75 StartAngle=1.5708 EndAngle=3.14159
    g3: LineSegment StartX=-12.35 StartY=8.1 StartZ=0 EndX=12.35 EndY=8.1 EndZ=0
    g4: ArcOfCircle CenterX=12.35 CenterY=6.35 CenterZ=0 NormalX=0 NormalY=0 NormalZ=1 AngleXU=0 Radius=1.75 StartAngle=1e-16 EndAngle=1.5708
    g5: LineSegment StartX=14.1 StartY=6.35 StartZ=0 EndX=14.1 EndY=-6.35 EndZ=0
    g6: ArcOfCircle CenterX=12.35 CenterY=-6.35 CenterZ=0 NormalX=0 NormalY=0 NormalZ=1 AngleXU=0 Radius=1.75 StartAngle=4.71239 EndAngle=6.28319
    g7: LineSegment StartX=12.35 StartY=-8.1 StartZ=0 EndX=-12.35 EndY=-8.1 EndZ=0
    g8: ArcOfCircle CenterX=-12.35 CenterY=-6.35 CenterZ=0 NormalX=0 NormalY=0 NormalZ=1 AngleXU=0 Radius=1.75 StartAngle=3.14159 EndAngle=4.71239
    g9: LineSegment StartX=-14.1 StartY=-6.35 StartZ=0 EndX=-14.1 EndY=6.35 EndZ=0
    g10: GeomPoint X=-14.1 Y=8.1 Z=0
    g11: GeomPoint X=14.1 Y=-8.1 Z=0
  constraints (28):
    c: Tangent(g2,g3) = 1.5708
    c: Tangent(g3,g4) = 1.5708
    c: Tangent(g4,g5) = 1.5708
    c: Tangent(g5,g6) = 1.5708
    c: Tangent(g6,g7) = 1.5708
    c: Tangent(g7,g8) = 1.5708
    c: Tangent(g8,g9) = 1.5708
    c: Tangent(g9,g2) = 1.5708
    c: Horizontal(g3)
    c: Horizontal(g7)
    c: Vertical(g5)
    c: Vertical(g9)
    c: Equal(g2,g4)
    c: Equal(g4,g6)
    c: Equal(g6,g8)
    c: PointOnObject(g10,g3)
    c: PointOnObject(g10,g9)
    c: PointOnObject(g11,g5)
    c: PointOnObject(g11,g7)
    c: DistanceX(g2,g4) = 28.2
    c: DistanceY(g7,g2) = 16.2
    c: Symmetric(g8,g4,g-1)
    c: Diameter(g2) = 3.5
    c: Symmetric(g0,g1,g-1)
    c: Diameter(g1) = 2.9
    c: Diameter(g0) = 2.9
    c: DistanceY(g0,g1) = 9.65
    c: Distance(g1,g0) = 23.8
FEATURE [PartDesign::Pad] Pad243
  Direction = (0,0,1)
  Length = 10.4
  Length2 = 10
  Profile = -> Sketch256
  ReferenceAxis = -> Sketch256 [N_Axis]
  Type = 0
FEATURE [Sketcher::SketchObject] Sketch257
  FullyConstrained = true
  MapMode = 5
  Placement = pos=(0,8.1,0) rot=(0,0.707107,0.707107;3.14159rad)
  Support = -> [Pad243]
  sketch-geometry (4):
    g0: LineSegment StartX=-10.9 StartY=7.25 StartZ=0 EndX=-8 EndY=7.25 EndZ=0
    g1: LineSegment StartX=-8 StartY=7.25 StartZ=0 EndX=-8 EndY=3.15 EndZ=0
    g2: LineSegment StartX=-8 StartY=3.15 StartZ=0 EndX=-10.9 EndY=3.15 EndZ=0
    g3: LineSegment StartX=-10.9 StartY=3.15 StartZ=0 EndX=-10.9 EndY=7.25 EndZ=0
  constraints (12):
    c: Coincident(g0,g1)
    c: Coincident(g1,g2)
    c: Coincident(g2,g3)
    c: Coincident(g3,g0)
    c: Horizontal(g0)
    c: Horizontal(g2)
    c: Vertical(g1)
    c: Vertical(g3)
    c: DistanceX(g0,g0) = 2.9
    c: DistanceY(g3,g3) = 4.1
    c: DistanceY(g-1,g1) = 3.15
    c: DistanceX(g2,g-1) = 10.9
FEATURE [PartDesign::Pad] Pad244
  BaseFeature = -> Pad243
  Direction = (0,1,-2e-16)
  Length = 3
  Length2 = 10
  Profile = -> Sketch257
  ReferenceAxis = -> Sketch257 [N_Axis]
  Type = 0
FEATURE [Sketcher::SketchObject] Sketch258
  FullyConstrained = true
  MapMode = 5
  Placement = pos=(-14.1,0,0) rot=(0.57735,-0.57735,-0.57735;2.0944rad)
  Support = -> [Pad244]
  sketch-geometry (4):
    g0: LineSegment StartX=3.9 StartY=2 StartZ=0 EndX=4.7 EndY=2 EndZ=0
    g1: LineSegment StartX=4.7 StartY=2 StartZ=0 EndX=4.7 EndY=8.4 EndZ=0
    g2: LineSegment StartX=4.7 StartY=8.4 StartZ=0 EndX=3.9 EndY=8.4 EndZ=0
    g3: LineSegment StartX=3.9 StartY=8.4 StartZ=0 EndX=3.9 EndY=2 EndZ=0
  constraints (12):
    c: Coincident(g0,g1)
    c: Coincident(g1,g2)
    c: Coincident(g2,g3)
    c: Coincident(g3,g0)
    c: Horizontal(g0)
    c: Horizontal(g2)
    c: Vertical(g1)
    c: Vertical(g3)
    c: DistanceX(g2,g2) = 0.8
    c: DistanceY(g3,g3) = 6.4
    c: DistanceY(g-1,g0) = 2
    c: DistanceX(g-1,g0) = 4.7
FEATURE [PartDesign::Pad] Pad245
  BaseFeature = -> Pad244
  Direction = (-1,0,0)
  Length = 10
  Length2 = 10
  Profile = -> Sketch258
  ReferenceAxis = -> Sketch258 [N_Axis]
  Type = 0
FEATURE [Sketcher::SketchObject] Sketch259
  FullyConstrained = true
  MapMode = 5
  Placement = pos=(0,-8.1,0) rot=(1,0,0;1.5708rad)
  Support = -> [Pad245]
  sketch-geometry (8):
    g0: LineSegment StartX=-3.5 StartY=8.45 StartZ=0 EndX=-0.5 EndY=8.45 EndZ=0
    g1: LineSegment StartX=-0.5 StartY=8.45 StartZ=0 EndX=-0.5 EndY=1.95 EndZ=0
    g2: LineSegment StartX=-0.5 StartY=1.95 StartZ=0 EndX=-3.5 EndY=1.95 EndZ=0
    g3: LineSegment StartX=-3.5 StartY=8.45 StartZ=0 EndX=-3.5 EndY=7.7 EndZ=0
    g4: LineSegment StartX=-3.5 StartY=7.7 StartZ=0 EndX=-9.5 EndY=7.7 EndZ=0
    g5: LineSegment StartX=-9.5 StartY=7.7 StartZ=0 EndX=-9.5 EndY=2.7 EndZ=0
    g6: LineSegment StartX=-9.5 StartY=2.7 StartZ=0 EndX=-3.5 EndY=2.7 EndZ=0
    g7: LineSegment StartX=-3.5 StartY=2.7 StartZ=0 EndX=-3.5 EndY=1.95 EndZ=0
  constraints (24):
    c: Coincident(g0,g1)
    c: Coincident(g1,g2)
    c: Horizontal(g0)
    c: Horizontal(g2)
    c: Vertical(g1)
    c: DistanceY(g1,g1) = 6.5
    c: DistanceX(g0,g0) = 3
    c: DistanceY(g-1,g1) = 1.95
    c: DistanceX(g1,g-1) = 0.5
    c: Coincident(g0,g3)
    c: Vertical(g3)
    c: Coincident(g3,g4)
    c: Horizontal(g4)
    c: Coincident(g4,g5)
    c: Vertical(g5)
    c: Coincident(g5,g6)
    c: Horizontal(g6)
    c: Coincident(g6,g7)
    c: Coincident(g7,g2)
    c: Vertical(g7)
    c: DistanceY(g5,g5) = 5
    c: DistanceY(g7,g7) = 0.75
    c: DistanceX(g4,g0) = 9
    c: Vertical(g3,g6)
FEATURE [PartDesign::Pad] Pad246
  BaseFeature = -> Pad245
  Direction = (0,-1,2e-16)
  Length = 3
  Length2 = 10
  Profile = -> Sketch259
  ReferenceAxis = -> Sketch259 [N_Axis]
  Type = 0
FEATURE [PartDesign::Body] Body085  label="switch039"
  Group = -> [Sketch256,Pad243,Sketch257,Pad244,Sketch258,Pad245,Sketch259,Pad246]
  Origin = -> Origin085
  Placement = pos=(14.15,0,0) rot=(0,-1,0;1.5708rad)
  Tip = -> Pad246
FEATURE [Part::Cut] Cut027
  Base = -> Body084
  Placement = pos=(0.7,0,0) rot=(0,0,1;0rad)
  Tool = -> Body085
FEATURE [Sketcher::SketchObject] Sketch260
  FullyConstrained = true
  MapMode = 5
  Support = -> [XY_Plane086]
  sketch-geometry (6):
    g0: LineSegment StartX=5.19 StartY=1.5 StartZ=0 EndX=-5.19 EndY=1.5 EndZ=0
    g1: LineSegment StartX=-4.79 StartY=0 StartZ=0 EndX=4.79 EndY=0 EndZ=0
    g2: LineSegment StartX=-5.19 StartY=1.5 StartZ=0 EndX=-4.79 EndY=0.928741 EndZ=0
    g3: LineSegment StartX=-4.79 StartY=0.928741 StartZ=0 EndX=-4.79 EndY=0 EndZ=0
    g4: LineSegment StartX=5.19 StartY=1.5 StartZ=0 EndX=4.79 EndY=0.928741 EndZ=0
    g5: LineSegment StartX=4.79 StartY=0.928741 StartZ=0 EndX=4.79 EndY=0 EndZ=0
  constraints (17):
    c: Horizontal(g0)
    c: DistanceX(g0,g0) = 10.38
    c: Symmetric(g1,g1,g-1)
    c: DistanceY(g1,g0) = 1.5
    c: Horizontal(g1,g1)
    c: Coincident(g0,g2)
    c: Coincident(g2,g3)
    c: Coincident(g3,g1)
    c: Vertical(g3)
    c: Coincident(g0,g4)
    c: Coincident(g4,g5)
    c: Coincident(g5,g1)
    c: Vertical(g5)
    c: Angle(g2,g0) = 0.959931
    c: Angle(g0,g4) = 0.959931
    c: Horizontal(g2,g4)
    c: DistanceX(g0,g2) = 0.4
FEATURE [PartDesign::Revolution] Revolution010
  Angle = 360
  Axis = (1,0,0)
  Base = (0,0,0)
  Profile = -> Sketch260
  ReferenceAxis = -> X_Axis086
FEATURE [PartDesign::Body] Body086
  Group = -> [Sketch260,Revolution010]
  Origin = -> Origin086
  Placement = pos=(9.65,-4.84,10.9) rot=(0,0,1;0rad)
  Tip = -> Revolution010
FEATURE [Part::Cut] Cut028
  Base = -> Cut027
  Tool = -> Body086
FEATURE [Sketcher::SketchObject] Sketch241
  FullyConstrained = true
  MapMode = 5
  Support = -> [XY_Plane075]
  sketch-geometry (6):
    g0: LineSegment StartX=5.19 StartY=1.5 StartZ=0 EndX=-5.19 EndY=1.5 EndZ=0
    g1: LineSegment StartX=-4.79 StartY=0 StartZ=0 EndX=4.79 EndY=0 EndZ=0
    g2: LineSegment StartX=-5.19 StartY=1.5 StartZ=0 EndX=-4.79 EndY=0.928741 EndZ=0
    g3: LineSegment StartX=-4.79 StartY=0.928741 StartZ=0 EndX=-4.79 EndY=0 EndZ=0
    g4: LineSegment StartX=5.19 StartY=1.5 StartZ=0 EndX=4.79 EndY=0.928741 EndZ=0
    g5: LineSegment StartX=4.79 StartY=0.928741 StartZ=0 EndX=4.79 EndY=0 EndZ=0
  constraints (17):
    c: Horizontal(g0)
    c: DistanceX(g0,g0) = 10.38
    c: Symmetric(g1,g1,g-1)
    c: DistanceY(g1,g0) = 1.5
    c: Horizontal(g1,g1)
    c: Coincident(g0,g2)
    c: Coincident(g2,g3)
    c: Coincident(g3,g1)
    c: Vertical(g3)
    c: Coincident(g0,g4)
    c: Coincident(g4,g5)
    c: Coincident(g5,g1)
    c: Vertical(g5)
    c: Angle(g2,g0) = 0.959931
    c: Angle(g0,g4) = 0.959931
    c: Horizontal(g2,g4)
    c: DistanceX(g0,g2) = 0.4
FEATURE [PartDesign::Revolution] Revolution007
  Angle = 360
  Axis = (1,0,0)
  Base = (0,0,0)
  Profile = -> Sketch241
  ReferenceAxis = -> X_Axis075
FEATURE [PartDesign::Body] Body075
  Group = -> [Sketch241,Revolution007]
  Origin = -> Origin075
  Placement = pos=(9.65,-4.84,10.9) rot=(0,0,1;0rad)
  Tip = -> Revolution007
FEATURE [Sketcher::SketchObject] Sketch236
  FullyConstrained = true
  MapMode = 5
  Placement = pos=(0,0,0) rot=(1,0,0;1.5708rad)
  Support = -> [XZ_Plane073]
  sketch-geometry (6):
    g0: LineSegment StartX=-4 StartY=7.5 StartZ=0 EndX=4 EndY=7.5 EndZ=0
    g1: LineSegment StartX=6.5 StartY=-12.5 StartZ=0 EndX=-6.5 EndY=-12.5 EndZ=0
    g2: LineSegment StartX=-6.5 StartY=-12.5 StartZ=0 EndX=-6.5 EndY=2.5 EndZ=0
    g3: LineSegment StartX=-6.5 StartY=2.5 StartZ=0 EndX=-4 EndY=7.5 EndZ=0
    g4: LineSegment StartX=6.5 StartY=-12.5 StartZ=0 EndX=6.5 EndY=2.5 EndZ=0
    g5: LineSegment StartX=6.5 StartY=2.5 StartZ=0 EndX=4 EndY=7.5 EndZ=0
  constraints (18):
    c: Horizontal(g0)
    c: Horizontal(g1)
    c: DistanceY(g1,g0) = 20
    c: DistanceY(g-1,g0) = 7.5
    c: DistanceX(g1,g-1) = 6.5
    c: DistanceX(g1,g1) = 13
    c: DistanceX(g0,g0) = 8
    c: Coincident(g1,g2)
    c: Vertical(g2)
    c: Coincident(g2,g3)
    c: Coincident(g3,g0)
    c: Coincident(g1,g4)
    c: Vertical(g4)
    c: Coincident(g4,g5)
    c: Coincident(g5,g0)
    c: DistanceX(g0,g-1) = 4
    c: Horizontal(g2,g4)
    c: DistanceY(g2,g0) = 5
FEATURE [PartDesign::Pad] Pad226
  Direction = (0,-1,-2e-16)
  Length = 11
  Length2 = 10
  Placement = pos=(0,0,0) rot=(1,0,0;1.5708rad)
  Profile = -> Sketch236
  ReferenceAxis = -> Sketch236 [N_Axis]
  Type = 0
FEATURE [PartDesign::Body] Body073
  Group = -> [Sketch236,Pad226]
  Origin = -> Origin073
  Placement = pos=(8.95,0,6.5) rot=(0,0,1;0rad)
  Tip = -> Pad226
FEATURE [Sketcher::SketchObject] Sketch237
  FullyConstrained = true
  MapMode = 5
  Support = -> [XY_Plane074]
  sketch-geometry (12):
    g0: Circle CenterX=10.8779 CenterY=-4.825 CenterZ=0 NormalX=0 NormalY=0 NormalZ=1 AngleXU=0 Radius=1.45
    g1: Circle CenterX=-10.8779 CenterY=4.825 CenterZ=0 NormalX=0 NormalY=0 NormalZ=1 AngleXU=0 Radius=1.45
    g2: ArcOfCircle CenterX=-12.35 CenterY=6.35 CenterZ=0 NormalX=0 NormalY=0 NormalZ=1 AngleXU=0 Radius=1.75 StartAngle=1.5708 EndAngle=3.14159
    g3: LineSegment StartX=-12.35 StartY=8.1 StartZ=0 EndX=12.35 EndY=8.1 EndZ=0
    g4: ArcOfCircle CenterX=12.35 CenterY=6.35 CenterZ=0 NormalX=0 NormalY=0 NormalZ=1 AngleXU=0 Radius=1.75 StartAngle=1e-16 EndAngle=1.5708
    g5: LineSegment StartX=14.1 StartY=6.35 StartZ=0 EndX=14.1 EndY=-6.35 EndZ=0
    g6: ArcOfCircle CenterX=12.35 CenterY=-6.35 CenterZ=0 NormalX=0 NormalY=0 NormalZ=1 AngleXU=0 Radius=1.75 StartAngle=4.71239 EndAngle=6.28319
    g7: LineSegment StartX=12.35 StartY=-8.1 StartZ=0 EndX=-12.35 EndY=-8.1 EndZ=0
    g8: ArcOfCircle CenterX=-12.35 CenterY=-6.35 CenterZ=0 NormalX=0 NormalY=0 NormalZ=1 AngleXU=0 Radius=1.75 StartAngle=3.14159 EndAngle=4.71239
    g9: LineSegment StartX=-14.1 StartY=-6.35 StartZ=0 EndX=-14.1 EndY=6.35 EndZ=0
    g10: GeomPoint X=-14.1 Y=8.1 Z=0
    g11: GeomPoint X=14.1 Y=-8.1 Z=0
  constraints (28):
    c: Tangent(g2,g3) = 1.5708
    c: Tangent(g3,g4) = 1.5708
    c: Tangent(g4,g5) = 1.5708
    c: Tangent(g5,g6) = 1.5708
    c: Tangent(g6,g7) = 1.5708
    c: Tangent(g7,g8) = 1.5708
    c: Tangent(g8,g9) = 1.5708
    c: Tangent(g9,g2) = 1.5708
    c: Horizontal(g3)
    c: Horizontal(g7)
    c: Vertical(g5)
    c: Vertical(g9)
    c: Equal(g2,g4)
    c: Equal(g4,g6)
    c: Equal(g6,g8)
    c: PointOnObject(g10,g3)
    c: PointOnObject(g10,g9)
    c: PointOnObject(g11,g5)
    c: PointOnObject(g11,g7)
    c: DistanceX(g2,g4) = 28.2
    c: DistanceY(g7,g2) = 16.2
    c: Symmetric(g8,g4,g-1)
    c: Diameter(g2) = 3.5
    c: Symmetric(g0,g1,g-1)
    c: Diameter(g1) = 2.9
    c: Diameter(g0) = 2.9
    c: DistanceY(g0,g1) = 9.65
    c: Distance(g1,g0) = 23.8
FEATURE [PartDesign::Pad] Pad227
  Direction = (0,0,1)
  Length = 10.4
  Length2 = 10
  Profile = -> Sketch237
  ReferenceAxis = -> Sketch237 [N_Axis]
  Type = 0
FEATURE [Sketcher::SketchObject] Sketch238
  FullyConstrained = true
  MapMode = 5
  Placement = pos=(0,8.1,0) rot=(0,0.707107,0.707107;3.14159rad)
  Support = -> [Pad227]
  sketch-geometry (4):
    g0: LineSegment StartX=-10.9 StartY=7.25 StartZ=0 EndX=-8 EndY=7.25 EndZ=0
    g1: LineSegment StartX=-8 StartY=7.25 StartZ=0 EndX=-8 EndY=3.15 EndZ=0
    g2: LineSegment StartX=-8 StartY=3.15 StartZ=0 EndX=-10.9 EndY=3.15 EndZ=0
    g3: LineSegment StartX=-10.9 StartY=3.15 StartZ=0 EndX=-10.9 EndY=7.25 EndZ=0
  constraints (12):
    c: Coincident(g0,g1)
    c: Coincident(g1,g2)
    c: Coincident(g2,g3)
    c: Coincident(g3,g0)
    c: Horizontal(g0)
    c: Horizontal(g2)
    c: Vertical(g1)
    c: Vertical(g3)
    c: DistanceX(g0,g0) = 2.9
    c: DistanceY(g3,g3) = 4.1
    c: DistanceY(g-1,g1) = 3.15
    c: DistanceX(g2,g-1) = 10.9
FEATURE [PartDesign::Pad] Pad228
  BaseFeature = -> Pad227
  Direction = (0,1,-2e-16)
  Length = 3
  Length2 = 10
  Profile = -> Sketch238
  ReferenceAxis = -> Sketch238 [N_Axis]
  Type = 0
FEATURE [Sketcher::SketchObject] Sketch239
  FullyConstrained = true
  MapMode = 5
  Placement = pos=(-14.1,0,0) rot=(0.57735,-0.57735,-0.57735;2.0944rad)
  Support = -> [Pad228]
  sketch-geometry (4):
    g0: LineSegment StartX=3.9 StartY=2 StartZ=0 EndX=4.7 EndY=2 EndZ=0
    g1: LineSegment StartX=4.7 StartY=2 StartZ=0 EndX=4.7 EndY=8.4 EndZ=0
    g2: LineSegment StartX=4.7 StartY=8.4 StartZ=0 EndX=3.9 EndY=8.4 EndZ=0
    g3: LineSegment StartX=3.9 StartY=8.4 StartZ=0 EndX=3.9 EndY=2 EndZ=0
  constraints (12):
    c: Coincident(g0,g1)
    c: Coincident(g1,g2)
    c: Coincident(g2,g3)
    c: Coincident(g3,g0)
    c: Horizontal(g0)
    c: Horizontal(g2)
    c: Vertical(g1)
    c: Vertical(g3)
    c: DistanceX(g2,g2) = 0.8
    c: DistanceY(g3,g3) = 6.4
    c: DistanceY(g-1,g0) = 2
    c: DistanceX(g-1,g0) = 4.7
FEATURE [PartDesign::Pad] Pad229
  BaseFeature = -> Pad228
  Direction = (-1,0,0)
  Length = 10
  Length2 = 10
  Profile = -> Sketch239
  ReferenceAxis = -> Sketch239 [N_Axis]
  Type = 0
FEATURE [Sketcher::SketchObject] Sketch240
  FullyConstrained = true
  MapMode = 5
  Placement = pos=(0,-8.1,0) rot=(1,0,0;1.5708rad)
  Support = -> [Pad229]
  sketch-geometry (8):
    g0: LineSegment StartX=-3.5 StartY=8.45 StartZ=0 EndX=-0.5 EndY=8.45 EndZ=0
    g1: LineSegment StartX=-0.5 StartY=8.45 StartZ=0 EndX=-0.5 EndY=1.95 EndZ=0
    g2: LineSegment StartX=-0.5 StartY=1.95 StartZ=0 EndX=-3.5 EndY=1.95 EndZ=0
    g3: LineSegment StartX=-3.5 StartY=8.45 StartZ=0 EndX=-3.5 EndY=7.7 EndZ=0
    g4: LineSegment StartX=-3.5 StartY=7.7 StartZ=0 EndX=-9.5 EndY=7.7 EndZ=0
    g5: LineSegment StartX=-9.5 StartY=7.7 StartZ=0 EndX=-9.5 EndY=2.7 EndZ=0
    g6: LineSegment StartX=-9.5 StartY=2.7 StartZ=0 EndX=-3.5 EndY=2.7 EndZ=0
    g7: LineSegment StartX=-3.5 StartY=2.7 StartZ=0 EndX=-3.5 EndY=1.95 EndZ=0
  constraints (24):
    c: Coincident(g0,g1)
    c: Coincident(g1,g2)
    c: Horizontal(g0)
    c: Horizontal(g2)
    c: Vertical(g1)
    c: DistanceY(g1,g1) = 6.5
    c: DistanceX(g0,g0) = 3
    c: DistanceY(g-1,g1) = 1.95
    c: DistanceX(g1,g-1) = 0.5
    c: Coincident(g0,g3)
    c: Vertical(g3)
    c: Coincident(g3,g4)
    c: Horizontal(g4)
    c: Coincident(g4,g5)
    c: Vertical(g5)
    c: Coincident(g5,g6)
    c: Horizontal(g6)
    c: Coincident(g6,g7)
    c: Coincident(g7,g2)
    c: Vertical(g7)
    c: DistanceY(g5,g5) = 5
    c: DistanceY(g7,g7) = 0.75
    c: DistanceX(g4,g0) = 9
    c: Vertical(g3,g6)
FEATURE [PartDesign::Pad] Pad230
  BaseFeature = -> Pad229
  Direction = (0,-1,2e-16)
  Length = 3
  Length2 = 10
  Profile = -> Sketch240
  ReferenceAxis = -> Sketch240 [N_Axis]
  Type = 0
FEATURE [PartDesign::Body] Body074  label="switch036"
  Group = -> [Sketch237,Pad227,Sketch238,Pad228,Sketch239,Pad229,Sketch240,Pad230]
  Origin = -> Origin074
  Placement = pos=(14.15,0,0) rot=(0,-1,0;1.5708rad)
  Tip = -> Pad230
FEATURE [Part::Cut] Cut021
  Base = -> Body073
  Placement = pos=(0.7,0,0) rot=(0,0,1;0rad)
  Tool = -> Body074
FEATURE [Part::Cut] Cut022
  Base = -> Cut021
  Tool = -> Body075
FEATURE [Sketcher::SketchObject] Sketch254
  FullyConstrained = true
  MapMode = 5
  Placement = pos=(0,-11,-4.8e-15) rot=(1,0,0;1.5708rad)
  Support = -> [Cut022]
  sketch-geometry (18):
    g0: Circle CenterX=9.65 CenterY=1 CenterZ=0 NormalX=0 NormalY=0 NormalZ=1 AngleXU=0 Radius=3
    g1: LineSegment StartX=3.15 StartY=5.5 StartZ=0 EndX=16.15 EndY=5.5 EndZ=0
    g2: LineSegment StartX=16.15 StartY=5.5 StartZ=0 EndX=16.15 EndY=-3.5 EndZ=0
    g3: LineSegment StartX=16.15 StartY=-3.5 StartZ=0 EndX=3.15 EndY=-3.5 EndZ=0
    g4: LineSegment StartX=3.15 StartY=-3.5 StartZ=0 EndX=3.15 EndY=5.5 EndZ=0
    g5: LineSegment StartX=9.35 StartY=2.6 StartZ=0 EndX=9.35 EndY=1.3 EndZ=0
    g6: LineSegment StartX=9.35 StartY=1.3 StartZ=0 EndX=8.05 EndY=1.3 EndZ=0
    g7: LineSegment StartX=8.05 StartY=1.3 StartZ=0 EndX=8.05 EndY=0.7 EndZ=0
    g8: LineSegment StartX=8.05 StartY=0.7 StartZ=0 EndX=9.35 EndY=0.7 EndZ=0
    g9: LineSegment StartX=9.35 StartY=0.7 StartZ=0 EndX=9.35 EndY=-0.6 EndZ=0
    g10: LineSegment StartX=9.35 StartY=-0.6 StartZ=0 EndX=9.95 EndY=-0.6 EndZ=0
    g11: LineSegment StartX=9.95 StartY=-0.6 StartZ=0 EndX=9.95 EndY=0.7 EndZ=0
    g12: LineSegment StartX=9.95 StartY=0.7 StartZ=0 EndX=11.25 EndY=0.7 EndZ=0
    g13: LineSegment StartX=11.25 StartY=0.7 StartZ=0 EndX=11.25 EndY=1.3 EndZ=0
    g14: LineSegment StartX=11.25 StartY=1.3 StartZ=0 EndX=9.95 EndY=1.3 EndZ=0
    g15: LineSegment StartX=9.95 StartY=1.3 StartZ=0 EndX=9.95 EndY=2.6 EndZ=0
    g16: LineSegment StartX=9.95 StartY=2.6 StartZ=0 EndX=9.35 EndY=2.6 EndZ=0
    g17: GeomPoint X=9.65 Y=1 Z=0
  constraints (52):
    c: Diameter(g0) = 6
    c: DistanceY(g0,g-1) = -1
    c: DistanceX(g-1,g0) = 9.65
    c: Coincident(g1,g2)
    c: Coincident(g2,g3)
    c: Coincident(g3,g4)
    c: Coincident(g4,g1)
    c: Horizontal(g1)
    c: Horizontal(g3)
    c: Vertical(g2)
    c: Vertical(g4)
    c: DistanceX(g-1,g3) = 3.15
    c: DistanceY(g3,g-1) = 3.5
    c: DistanceX(g3,g3) = 13
    c: DistanceY(g4,g4) = 9
    c: Vertical(g5)
    c: Coincident(g5,g6)
    c: Horizontal(g6)
    c: Coincident(g6,g7)
    c: Vertical(g7)
    c: Coincident(g7,g8)
    c: Coincident(g8,g9)
    c: Vertical(g9)
    c: Coincident(g9,g10)
    c: Horizontal(g10)
    c: Coincident(g10,g11)
    c: Coincident(g11,g12)
    c: Coincident(g12,g13)
    c: Coincident(g13,g14)
    c: Horizontal(g14)
    c: Coincident(g14,g15)
    c: Vertical(g15)
    c: Coincident(g15,g16)
    c: Coincident(g16,g5)
    c: Horizontal(g16)
    c: Horizontal(g12)
    c: Horizontal(g8)
    c: Vertical(g11)
    c: Vertical(g13)
    c: Vertical(g14,g11)
    c: Horizontal(g8,g11)
    c: Horizontal(g5,g14)
    c: Equal(g7,g16)
    c: Equal(g5,g6)
    c: Vertical(g8,g5)
    c: Equal(g6,g14)
    c: Equal(g15,g11)
    c: DistanceY(g13,g13) = 0.6
    c: DistanceX(g14,g14) = 1.3
    c: DistanceY(g-1,g17) = 1
    c: DistanceX(g-1,g17) = 9.65
    c: Symmetric(g8,g14,g0)
FEATURE [PartDesign::Pad] Pad241
  Direction = (0,-1,-2e-16)
  Length = 6
  Length2 = 10
  Profile = -> Sketch254
  ReferenceAxis = -> Sketch254 [N_Axis]
  Type = 0
FEATURE [PartDesign::Body] Body083
  Group = -> [CopyCut022,Sketch254,Pad241]
  Origin = -> Origin083
  Tip = -> Pad241
FEATURE [PartDesign::FeatureBase] Clone
  BaseFeature = -> Body083
FEATURE [PartDesign::Body] Body087
  BaseFeature = -> Body083
  Group = -> [Clone]
  Origin = -> Origin087
  Tip = -> Clone
FEATURE [Part::FeaturePython] Array012  # Draft array (typed FeaturePython)
  AlwaysSyncPlacement = false
  Angle = 360
  ArrayType = 0
  Axis = (0,0,1)
  Base = -> Body087
  Center = (0,0,0)
  Count = 12
  ExpandArray = false
  Fuse = false
  IntervalAxis = (0,0,0)
  IntervalX = (23.5,0,0)
  IntervalY = (0,100,0)
  IntervalZ = (0,0,40)
  NumberCircles = 3
  NumberPolar = 5
  NumberX = 12
  NumberY = 1
  NumberZ = 1
  PlacementList = 12 placements: arithmetic series from (0,0,0) step (23.5,0,0) to (258.5,0,0)
  RadialDistance = 50
  ScaleList = (12) [(1,1,1),(1,1,1),(1,1,1),(1,1,1),(1,1,1),(1,1,1),(1,1,1),(1,1,1),(1,1,1),(1,1,1),(1,1,1),(1,1,1)]
  Symmetry = 1
  TangentialDistance = 25
FEATURE [PartDesign::FeatureBase] Clone001
  BaseFeature = -> Body083
FEATURE [PartDesign::Body] Body088
  BaseFeature = -> Body083
  Group = -> [Clone001]
  Origin = -> Origin088
  Tip = -> Clone001
FEATURE [Part::FeaturePython] Array011  # Draft array (typed FeaturePython)
  AlwaysSyncPlacement = false
  Angle = 360
  ArrayType = 0
  Axis = (0,0,1)
  Base = -> Body088
  Center = (0,0,0)
  Count = 12
  ExpandArray = false
  Fuse = false
  IntervalAxis = (0,0,0)
  IntervalX = (23.5,0,0)
  IntervalY = (0,100,0)
  IntervalZ = (0,0,40)
  NumberCircles = 3
  NumberPolar = 5
  NumberX = 12
  NumberY = 1
  NumberZ = 1
  Placement = pos=(289.55,0,-21.76) rot=(0,1,0;3.14159rad)
  PlacementList = 12 placements: arithmetic series from (0,0,0) step (23.5,0,0) to (258.5,0,0)
  RadialDistance = 50
  ScaleList = (12) [(1,1,1),(1,1,1),(1,1,1),(1,1,1),(1,1,1),(1,1,1),(1,1,1),(1,1,1),(1,1,1),(1,1,1),(1,1,1),(1,1,1)]
  Symmetry = 1
  TangentialDistance = 25
FEATURE [PartDesign::FeatureBase] Clone002
  BaseFeature = -> Body083
FEATURE [PartDesign::Body] Body089
  BaseFeature = -> Body083
  Group = -> [Clone002]
  Origin = -> Origin089
  Tip = -> Clone002
FEATURE [Part::FeaturePython] Array010  # Draft array (typed FeaturePython)
  AlwaysSyncPlacement = false
  Angle = 360
  ArrayType = 0
  Axis = (0,0,1)
  Base = -> Body089
  Center = (0,0,0)
  Count = 12
  ExpandArray = false
  Fuse = false
  IntervalAxis = (0,0,0)
  IntervalX = (23.5,0,0)
  IntervalY = (0,100,0)
  IntervalZ = (0,0,40)
  NumberCircles = 3
  NumberPolar = 5
  NumberX = 12
  NumberY = 1
  NumberZ = 1
  Placement = pos=(23.5,0,-43.5) rot=(0,1,0;0rad)
  PlacementList = 12 placements: arithmetic series from (0,0,0) step (23.5,0,0) to (258.5,0,0)
  RadialDistance = 50
  ScaleList = (12) [(1,1,1),(1,1,1),(1,1,1),(1,1,1),(1,1,1),(1,1,1),(1,1,1),(1,1,1),(1,1,1),(1,1,1),(1,1,1),(1,1,1)]
  Symmetry = 1
  TangentialDistance = 25
FEATURE [PartDesign::FeatureBase] Clone003
  BaseFeature = -> Body083
FEATURE [PartDesign::Body] Body090
  BaseFeature = -> Body083
  Group = -> [Clone003]
  Origin = -> Origin090
  Tip = -> Clone003
FEATURE [Part::FeaturePython] Array009  # Draft array (typed FeaturePython)
  AlwaysSyncPlacement = false
  Angle = 360
  ArrayType = 0
  Axis = (0,0,1)
  Base = -> Body090
  Center = (0,0,0)
  Count = 12
  ExpandArray = false
  Fuse = false
  IntervalAxis = (0,0,0)
  IntervalX = (23.5,0,0)
  IntervalY = (0,100,0)
  IntervalZ = (0,0,40)
  NumberCircles = 3
  NumberPolar = 5
  NumberX = 12
  NumberY = 1
  NumberZ = 1
  Placement = pos=(313.05,0,-65.3) rot=(0,1,0;3.14159rad)
  PlacementList = 12 placements: arithmetic series from (0,0,0) step (23.5,0,0) to (258.5,0,0)
  RadialDistance = 50
  ScaleList = (12) [(1,1,1),(1,1,1),(1,1,1),(1,1,1),(1,1,1),(1,1,1),(1,1,1),(1,1,1),(1,1,1),(1,1,1),(1,1,1),(1,1,1)]
  Symmetry = 1
  TangentialDistance = 25
FEATURE [App::DocumentObjectGroup] Group003  label="keyCaps"
  Group = -> [Group002,Array012,Array011,Array010,Array009]
FEATURE [App::DocumentObjectGroup] Group005  label="additional"
  Group = -> [Cut022,Body083,Cut028]
FEATURE [Sketcher::SketchObject] Sketch261
  FullyConstrained = true
  Placement = pos=(0,0,0) rot=(1,0,0;1.5708rad)
  sketch-geometry (9):
    g0: LineSegment StartX=180.025 StartY=-117 StartZ=0 EndX=180.025 EndY=-80.28 EndZ=0
    g1: LineSegment StartX=180.025 StartY=-80.28 StartZ=0 EndX=168.275 EndY=-80.28 EndZ=0
    g2: LineSegment StartX=168.275 StartY=-80.28 StartZ=0 EndX=168.275 EndY=-50.28 EndZ=0
    g3: LineSegment StartX=168.275 StartY=-50.28 StartZ=0 EndX=156.525 EndY=-50.28 EndZ=0
    g4: LineSegment StartX=156.525 StartY=-50.28 StartZ=0 EndX=156.525 EndY=-28.52 EndZ=0
    g5: LineSegment StartX=156.525 StartY=-28.52 StartZ=0 EndX=144.775 EndY=-28.52 EndZ=0
    g6: LineSegment StartX=144.775 StartY=-28.52 StartZ=0 EndX=144.775 EndY=-6.76 EndZ=0
    g7: LineSegment StartX=144.775 StartY=-6.76 StartZ=0 EndX=138.9 EndY=-6.76 EndZ=0
    g8: LineSegment StartX=138.9 StartY=-6.76 StartZ=0 EndX=138.9 EndY=60.99 EndZ=0
  constraints (28):
    c: Vertical(g0)
    c: Coincident(g0,g1)
    c: Coincident(g1,g2)
    c: Coincident(g2,g3)
    c: Coincident(g3,g4)
    c: Coincident(g4,g5)
    c: Horizontal(g5)
    c: Coincident(g5,g6)
    c: Coincident(g6,g7)
    c: Horizontal(g7)
    c: Coincident(g7,g8)
    c: Vertical(g8)
    c: Horizontal(g1)
    c: Horizontal(g3)
    c: Vertical(g6)
    c: Vertical(g4)
    c: Vertical(g2)
    c: DistanceX(g-1,g8) = 138.9
    c: DistanceX(g7,g7) = 5.875
    c: DistanceX(g5,g5) = 11.75
    c: DistanceX(g3,g3) = 11.75
    c: DistanceX(g1,g1) = 11.75
    c: DistanceY(g6,g6) = 21.76
    c: DistanceY(g4,g4) = 21.76
    c: DistanceY(g-1,g7) = -6.76
    c: DistanceY(g2,g2) = 30
    c: DistanceY(g8,g8) = 67.75
    c: DistanceY(g0,g0) = 36.72
FEATURE [Part::Extrusion] Extrude
  Base = -> Sketch261
  Dir = (0,-1,2e-16)
  DirMode = 2
  FaceMakerClass = Part::FaceMakerBullseye
  LengthFwd = 10
  LengthRev = 0
  Placement = pos=(0,12,0) rot=(0,0,1;0rad)
  Solid = false
  Symmetric = false
FEATURE [Sketcher::SketchObject] Sketch262
  FullyConstrained = true
  MapMode = 5
  Placement = pos=(0,1e-16,0) rot=(1,0,0;1.5708rad)
  Support = -> [Pad068]
  sketch-geometry (19):
    g0: ArcOfCircle CenterX=4 CenterY=53 CenterZ=0 NormalX=0 NormalY=0 NormalZ=1 AngleXU=0 Radius=2 StartAngle=1.5708 EndAngle=3.14159
    g1: LineSegment StartX=4 StartY=55 StartZ=0 EndX=131.9 EndY=55 EndZ=0
    g2: ArcOfCircle CenterX=131.9 CenterY=53 CenterZ=0 NormalX=0 NormalY=0 NormalZ=1 AngleXU=0 Radius=2 StartAngle=1.7e-15 EndAngle=1.5708
    g3: LineSegment StartX=133.9 StartY=53 StartZ=0 EndX=133.9 EndY=22 EndZ=0
    g4: ArcOfCircle CenterX=131.9 CenterY=22 CenterZ=0 NormalX=0 NormalY=0 NormalZ=1 AngleXU=0 Radius=2 StartAngle=4.71239 EndAngle=6.28319
    g5: LineSegment StartX=131.9 StartY=20 StartZ=0 EndX=4 EndY=20 EndZ=0
    g6: ArcOfCircle CenterX=4 CenterY=22 CenterZ=0 NormalX=0 NormalY=0 NormalZ=1 AngleXU=0 Radius=2 StartAngle=3.14159 EndAngle=4.71239
    g7: LineSegment StartX=2 StartY=22 StartZ=0 EndX=2 EndY=53 EndZ=0
    g8: GeomPoint X=2 Y=55 Z=0
    g9: GeomPoint X=133.9 Y=20 Z=0
    g10: ArcOfCircle CenterX=145.9 CenterY=53 CenterZ=0 NormalX=0 NormalY=0 NormalZ=1 AngleXU=0 Radius=2 StartAngle=1.5708 EndAngle=3.14159
    g11: LineSegment StartX=145.9 StartY=55 StartZ=0 EndX=256.066 EndY=55 EndZ=0
    g12: ArcOfCircle CenterX=256.066 CenterY=53 CenterZ=0 NormalX=0 NormalY=0 NormalZ=1 AngleXU=0 Radius=2 StartAngle=0.468796 EndAngle=1.5708
    g13: LineSegment StartX=257.85 StartY=53.9036 StartZ=0 EndX=273.55 EndY=22.9036 EndZ=0
    g14: ArcOfCircle CenterX=271.766 CenterY=22 CenterZ=0 NormalX=0 NormalY=0 NormalZ=1 AngleXU=0 Radius=2 StartAngle=4.71239 EndAngle=6.75198
    g15: LineSegment StartX=271.766 StartY=20 StartZ=0 EndX=145.9 EndY=20 EndZ=0
    g16: ArcOfCircle CenterX=145.9 CenterY=22 CenterZ=0 NormalX=0 NormalY=0 NormalZ=1 AngleXU=0 Radius=2 StartAngle=3.14159 EndAngle=4.71239
    g17: LineSegment StartX=143.9 StartY=22 StartZ=0 EndX=143.9 EndY=53 EndZ=0
    g18: GeomPoint X=275.021 Y=20 Z=0
  constraints (46):
    c: Tangent(g0,g1) = 1.5708
    c: Tangent(g1,g2) = 1.5708
    c: Tangent(g2,g3) = 1.5708
    c: Tangent(g3,g4) = 1.5708
    c: Tangent(g4,g5) = 1.5708
    c: Tangent(g5,g6) = 1.5708
    c: Tangent(g6,g7) = 1.5708
    c: Tangent(g7,g0) = 1.5708
    c: Horizontal(g1)
    c: Horizontal(g5)
    c: Vertical(g3)
    c: Vertical(g7)
    c: Equal(g0,g2)
    c: Equal(g2,g4)
    c: Equal(g4,g6)
    c: PointOnObject(g8,g1)
    c: PointOnObject(g8,g7)
    c: PointOnObject(g9,g3)
    c: PointOnObject(g9,g5)
    c: Tangent(g10,g11) = 1.5708
    c: Tangent(g11,g12) = 1.5708
    c: Tangent(g12,g13) = 1.5708
    c: Tangent(g13,g14) = 1.5708
    c: Tangent(g14,g15) = 1.5708
    c: Tangent(g15,g16) = 1.5708
    c: Tangent(g16,g17) = 1.5708
    c: Tangent(g17,g10) = 1.5708
    c: Horizontal(g11)
    c: Horizontal(g15)
    c: Vertical(g17)
    c: Equal(g10,g12)
    c: Equal(g12,g14)
    c: Equal(g14,g16)
    c: PointOnObject(g18,g13)
    c: PointOnObject(g18,g15)
    c: Diameter(g0) = 4
    c: DistanceY(g-1,g0) = 55
    c: DistanceX(g6,g-1) = -2
    c: DistanceX(g-1,g3) = 133.9
    c: DistanceY(g-1,g5) = 20
    c: Diameter(g10) = 4
    c: DistanceX(g-1,g16) = 143.9
    c: DistanceY(g-1,g15) = 20
    c: DistanceY(g15,g10) = 35
    c: DistanceX(g16,g13) = 129.65
    c: DistanceX(g10,g12) = 113.95
FEATURE [PartDesign::Pocket] Pocket
  BaseFeature = -> Pad068
  Direction = (0,1,-2e-16)
  Length = 1.8
  Length2 = 5
  Placement = pos=(0,0,0) rot=(1,0,0;1.5708rad)
  Profile = -> Sketch262
  ReferenceAxis = -> Sketch262 [N_Axis]
  Type = 0
FEATURE [Sketcher::SketchObject] Sketch263
  FullyConstrained = true
  MapMode = 5
  Placement = pos=(0,1e-16,0) rot=(1,0,0;1.5708rad)
  Support = -> [Pad068]
  sketch-geometry (19):
    g0: ArcOfCircle CenterX=17 CenterY=40 CenterZ=0 NormalX=0 NormalY=0 NormalZ=1 AngleXU=0 Radius=10 StartAngle=1.5708 EndAngle=3.14159
    g1: LineSegment StartX=17 StartY=50 StartZ=0 EndX=118.9 EndY=50 EndZ=0
    g2: ArcOfCircle CenterX=118.9 CenterY=40 CenterZ=0 NormalX=0 NormalY=0 NormalZ=1 AngleXU=0 Radius=10 StartAngle=3e-16 EndAngle=1.5708
    g3: LineSegment StartX=128.9 StartY=40 StartZ=0 EndX=128.9 EndY=30 EndZ=0
    g4: ArcOfCircle CenterX=118.9 CenterY=30 CenterZ=0 NormalX=0 NormalY=0 NormalZ=1 AngleXU=0 Radius=10 StartAngle=4.71239 EndAngle=6.28319
    g5: LineSegment StartX=118.9 StartY=20 StartZ=0 EndX=17 EndY=20 EndZ=0
    g6: ArcOfCircle CenterX=17 CenterY=30 CenterZ=0 NormalX=0 NormalY=0 NormalZ=1 AngleXU=0 Radius=10 StartAngle=3.14159 EndAngle=4.71239
    g7: LineSegment StartX=7 StartY=30 StartZ=0 EndX=7 EndY=40 EndZ=0
    g8: GeomPoint X=7 Y=50 Z=0
    g9: GeomPoint X=128.9 Y=20 Z=0
    g10: ArcOfCircle CenterX=158.9 CenterY=40 CenterZ=0 NormalX=0 NormalY=0 NormalZ=1 AngleXU=0 Radius=10 StartAngle=1.5708 EndAngle=3.14159
    g11: LineSegment StartX=158.9 StartY=50 StartZ=0 EndX=252.9 EndY=50 EndZ=0
    g12: ArcOfCircle CenterX=252.9 CenterY=40 CenterZ=0 NormalX=0 NormalY=0 NormalZ=1 AngleXU=0 Radius=10 StartAngle=0 EndAngle=1.5708
    g13: LineSegment StartX=262.9 StartY=40 StartZ=0 EndX=262.9 EndY=30 EndZ=0
    g14: ArcOfCircle CenterX=252.9 CenterY=30 CenterZ=0 NormalX=0 NormalY=0 NormalZ=1 AngleXU=0 Radius=10 StartAngle=4.71239 EndAngle=6.28319
    g15: LineSegment StartX=252.9 StartY=20 StartZ=0 EndX=158.9 EndY=20 EndZ=0
    g16: ArcOfCircle CenterX=158.9 CenterY=30 CenterZ=0 NormalX=0 NormalY=0 NormalZ=1 AngleXU=0 Radius=10 StartAngle=3.14159 EndAngle=4.71239
    g17: LineSegment StartX=148.9 StartY=30 StartZ=0 EndX=148.9 EndY=40 EndZ=0
    g18: GeomPoint X=262.9 Y=20 Z=0
  constraints (46):
    c: Tangent(g0,g1) = 1.5708
    c: Tangent(g1,g2) = 1.5708
    c: Tangent(g2,g3) = 1.5708
    c: Tangent(g3,g4) = 1.5708
    c: Tangent(g4,g5) = 1.5708
    c: Tangent(g5,g6) = 1.5708
    c: Tangent(g6,g7) = 1.5708
    c: Tangent(g7,g0) = 1.5708
    c: Horizontal(g1)
    c: Horizontal(g5)
    c: Vertical(g3)
    c: Vertical(g7)
    c: Equal(g0,g2)
    c: Equal(g2,g4)
    c: Equal(g4,g6)
    c: PointOnObject(g8,g1)
    c: PointOnObject(g8,g7)
    c: PointOnObject(g9,g3)
    c: PointOnObject(g9,g5)
    c: Tangent(g10,g11) = 1.5708
    c: Tangent(g11,g12) = 1.5708
    c: Tangent(g12,g13) = 1.5708
    c: Tangent(g13,g14) = 1.5708
    c: Tangent(g14,g15) = 1.5708
    c: Tangent(g15,g16) = 1.5708
    c: Tangent(g16,g17) = 1.5708
    c: Tangent(g17,g10) = 1.5708
    c: Horizontal(g11)
    c: Horizontal(g15)
    c: Vertical(g17)
    c: Equal(g10,g12)
    c: Equal(g12,g14)
    c: Equal(g14,g16)
    c: PointOnObject(g18,g13)
    c: PointOnObject(g18,g15)
    c: Diameter(g0) = 20
    c: DistanceY(g-1,g0) = 50
    c: DistanceX(g6,g-1) = -7
    c: DistanceX(g-1,g3) = 128.9
    c: DistanceY(g-1,g5) = 20
    c: Diameter(g10) = 20
    c: DistanceX(g-1,g16) = 148.9
    c: DistanceY(g-1,g15) = 20
    c: DistanceY(g15,g10) = 30
    c: DistanceX(g10,g12) = 114
    c: Vertical(g13)
FEATURE [PartDesign::Pocket] Pocket001
  BaseFeature = -> Pocket
  Direction = (0,1,-2e-16)
  Length = 100
  Length2 = 5
  Placement = pos=(0,0,0) rot=(1,0,0;1.5708rad)
  Profile = -> Sketch263
  ReferenceAxis = -> Sketch263 [N_Axis]
  Type = 0
FEATURE [Part::Feature] Feature  label="clickyKeyboard"
  Placement = pos=(74.35,6.3,127.65) rot=(1,0,0;1.5708rad)
  shape: bbox 129.1 x 11.54 x 34.29 mm, 893 faces, 11 solids (baked)
FEATURE [App::DocumentObjectGroup] Group006  label="pcb's"
  Group = -> [Feature]
FEATURE [Sketcher::SketchObject] Sketch264
  FullyConstrained = true
  MapMode = 5
  Placement = pos=(0,1.8,-8e-16) rot=(1,0,0;1.5708rad)
  Support = -> [Pocket001]
  sketch-geometry (4):
    g0: Circle CenterX=148 CenterY=24.15 CenterZ=0 NormalX=0 NormalY=0 NormalZ=1 AngleXU=0 Radius=1.5
    g1: Circle CenterX=268.015 CenterY=24.15 CenterZ=0 NormalX=0 NormalY=0 NormalZ=1 AngleXU=0 Radius=1.5
    g2: Circle CenterX=130.45 CenterY=24.15 CenterZ=0 NormalX=0 NormalY=0 NormalZ=1 AngleXU=0 Radius=1.5
    g3: Circle CenterX=5.45 CenterY=24.15 CenterZ=0 NormalX=0 NormalY=0 NormalZ=1 AngleXU=0 Radius=1.5
  constraints (12):
    c: DistanceX(g0,g1) = 120.015
    c: Diameter(g0) = 3
    c: Diameter(g1) = 3
    c: Horizontal(g0,g1)
    c: DistanceX(g-1,g0) = 148
    c: DistanceY(g-1,g0) = 24.15
    c: Diameter(g3) = 3
    c: Diameter(g2) = 3
    c: Horizontal(g3,g2)
    c: Horizontal(g0,g2)
    c: DistanceX(g3,g2) = 125
    c: DistanceX(g-1,g3) = 5.45
FEATURE [PartDesign::Pad] Pad247
  BaseFeature = -> Pocket001
  Direction = (0,-1,4e-16)
  Length = 1.8
  Length2 = 10
  Placement = pos=(0,0,0) rot=(1,0,0;1.5708rad)
  Profile = -> Sketch264
  ReferenceAxis = -> Sketch264 [N_Axis]
  Type = 0
FEATURE [PartDesign::Fillet] Fillet010
  Base = -> Pad247 [Edge59,Edge5,Edge1,Edge2,Edge8,Edge60,Edge62,Edge63,Edge61]
  BaseFeature = -> Pad247
  Placement = pos=(0,0,0) rot=(1,0,0;1.5708rad)
  Radius = 10
  SupportTransform = false
  UseAllEdges = false
FEATURE [PartDesign::Fillet] Fillet011
  Base = -> Fillet010 [Edge7,Edge5,Edge1,Edge8,Edge6,Edge10,Edge12,Edge14,Edge16,Edge20,Edge19,Edge15,Edge11]
  BaseFeature = -> Fillet010
  Placement = pos=(0,0,0) rot=(1,0,0;1.5708rad)
  Radius = 2
  SupportTransform = false
  UseAllEdges = false
FEATURE [PartDesign::Body] Body016  label="keyboardBody"
  Group = -> [Sketch068,Pad068,Sketch262,Pocket,Sketch263,Pocket001,Sketch264,Pad247,Fillet010,Fillet011]
  Origin = -> Origin016
  Placement = pos=(0,4.7,0) rot=(0,0,1;0rad)
  Tip = -> Fillet011
FEATURE [Part::Cut] Cut
  Base = -> Body016
  Tool = -> Array008
FEATURE [Part::Cut] Cut001
  Base = -> Cut
  Tool = -> Array007
FEATURE [Part::Cut] Cut002
  Base = -> Cut001
  Tool = -> Array006
FEATURE [Part::Cut] Cut003
  Base = -> Cut002
  Tool = -> Array005
FEATURE [Part::Cut] Cut004
  Base = -> Cut003
  Tool = -> Array004
FEATURE [Part::Cut] Cut005
  Base = -> Cut004
  Tool = -> Body017
FEATURE [Part::Cut] Cut006
  Base = -> Cut005
  Tool = -> Body015
FEATURE [Part::Cut] Cut007  label="keyboardBase"
  Base = -> Cut006
  Tool = -> Body014
FEATURE [Part::FeaturePython] Slice  # WARN: FeaturePython — macro-defined, semantics opaque (R4)
  Base = -> Cut007
  Mode = 1
  Tolerance = 0
  Tools = -> [Extrude]
FEATURE [Part::FeaturePython] Slice_child0  label="Slice.0"  # WARN: FeaturePython — macro-defined, semantics opaque (R4)
  Base = -> Slice
  FilterType = 1
  Invert = false
  OverrideMaxVal = 0
  WindowFrom = 80
  WindowTo = 100
  items = 0
FEATURE [Part::FeaturePython] Slice_child1  label="Slice.1"  # WARN: FeaturePython — macro-defined, semantics opaque (R4)
  Base = -> Slice
  FilterType = 1
  Invert = false
  OverrideMaxVal = 0
  WindowFrom = 80
  WindowTo = 100
  items = 1
FEATURE [App::DocumentObjectGroup] GrExplode_Slice  label="Exploded Slice"
  Group = -> [Slice_child0,Slice_child1]
